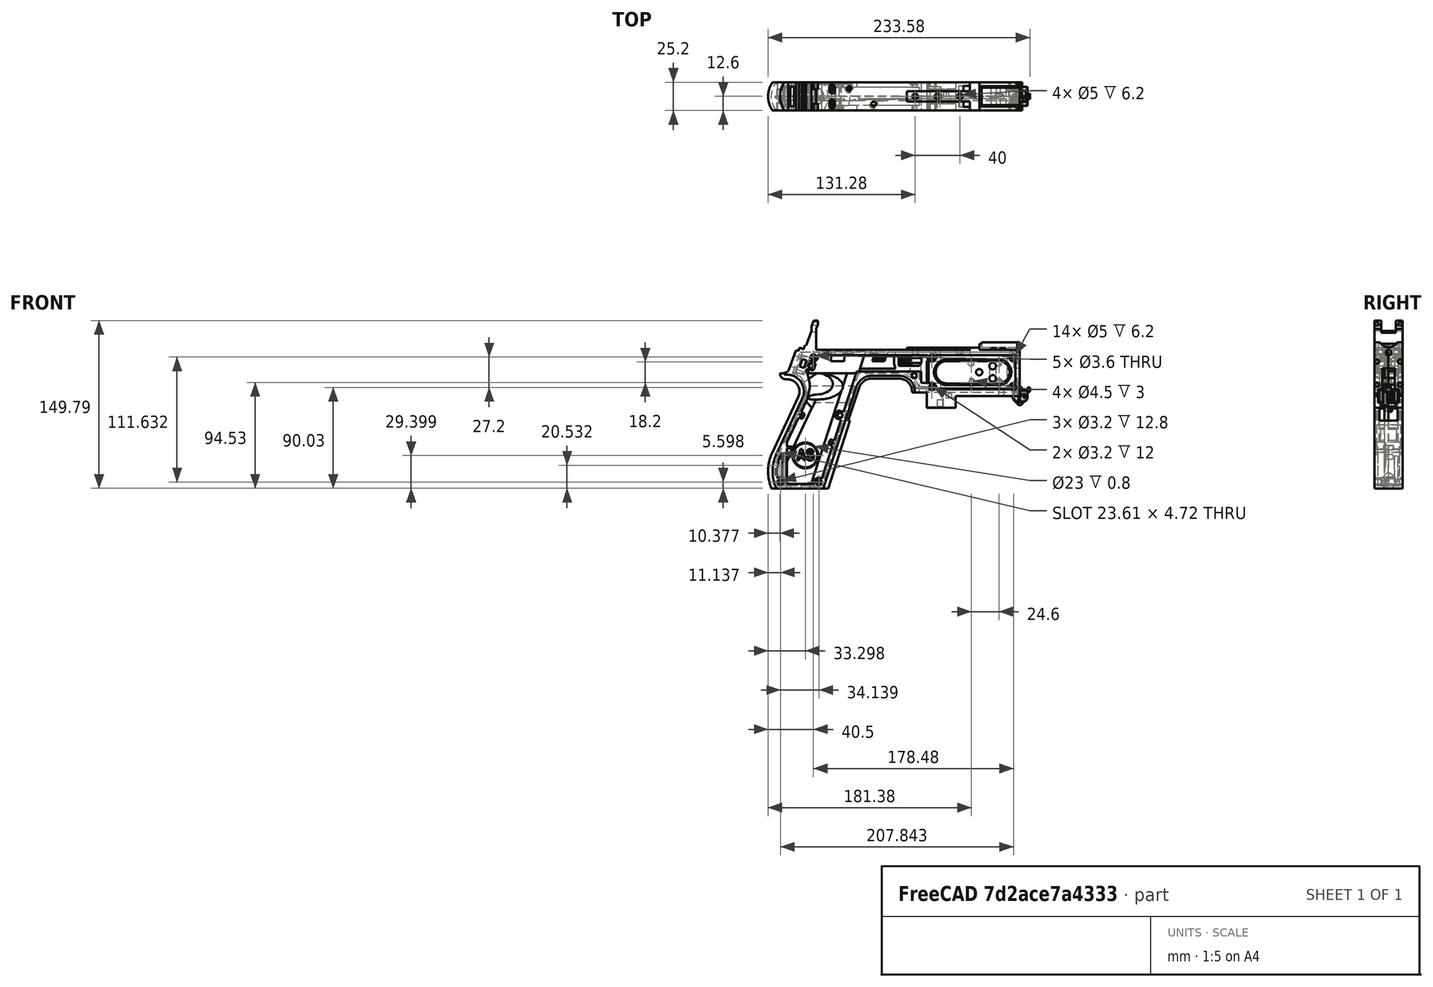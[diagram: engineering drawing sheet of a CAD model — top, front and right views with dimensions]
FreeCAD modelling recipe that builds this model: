
FCSTD DOCUMENT  (FreeCAD 1.0R39319 (Git))
Label: PICON-OF_ver_36
License: All rights reserved
LicenseURL: https://en.wikipedia.org/wiki/All_rights_reserved
objects: Sketcher::SketchObject×106, Part::Extrusion×50, Part::Cut×39, PartDesign::Pad×28, PartDesign::Pocket×18, PartDesign::Chamfer×15, PartDesign::Body×9, PartDesign::Fillet×6, PartDesign::SubtractivePipe×4, Part::Part2DObjectPython×4, PartDesign::SubtractiveLoft×4, PartDesign::Plane×2, PartDesign::SubShapeBinder×2, Part::Sweep×1, PartDesign::ShapeBinder×1, Part::MultiFuse×1, Mesh::Feature×1
note: 546 computed .brp shape members not serialized (recipe doc carries the construction recipe); baked Part::Feature solids carry a one-line shape summary decoded from their .brp

FEATURE [Sketcher::SketchObject] Sketch  label="corpo principale"
  ArcFitTolerance = 1e-06
  AttacherType = Attacher::AttachEngine3D
  AttachmentSupport = -> [XZ_Plane]
  FullyConstrained = true
  MakeInternals = false
  MapMode = 5
  Placement = pos=(0,0,0) rot=(1,0,0;1.5708rad)
  sketch-geometry (65):
    g0: LineSegment StartX=0 StartY=0 StartZ=0 EndX=-57.2 EndY=0 EndZ=0
    g1: LineSegment StartX=-57.2 StartY=0 StartZ=0 EndX=-57.2 EndY=-10.4 EndZ=0
    g2: LineSegment StartX=-57.2 StartY=-10.4 StartZ=0 EndX=-82.8 EndY=-10.4 EndZ=0
    g3: LineSegment StartX=-82.8 StartY=-10.4 StartZ=0 EndX=-82.8 EndY=3.2 EndZ=0
    g4: LineSegment StartX=-82.8 StartY=3.2 StartZ=0 EndX=-93.6 EndY=3.2 EndZ=0
    g5: LineSegment StartX=-93.6 StartY=3.2 StartZ=0 EndX=-93.6 EndY=4 EndZ=0
    g6: LineSegment StartX=-107.6 StartY=18 StartZ=0 EndX=-132.428 EndY=18 EndZ=0
    g7: LineSegment StartX=-145.743 StartY=8.32624 StartZ=0 EndX=-175.232 EndY=-82.4316 EndZ=0
    g8: LineSegment StartX=-175.232 StartY=-82.4316 StartZ=0 EndX=-217.232 EndY=-82.4316 EndZ=0
    g9: LineSegment StartX=-217.232 StartY=-52.1862 StartZ=0 EndX=-193.988 EndY=-2.33927 EndZ=0
    g10: LineSegment StartX=-206.196 StartY=23.0857 StartZ=0 EndX=-199.861 EndY=40.4914 EndZ=0
    g11: LineSegment StartX=-199.861 StartY=40.4914 StartZ=0 EndX=-197.061 EndY=40.4914 EndZ=0
    g12: LineSegment StartX=-197.061 StartY=40.4914 StartZ=0 EndX=-197.061 EndY=42.8914 EndZ=0
    g13: LineSegment StartX=-197.061 StartY=42.8914 StartZ=0 EndX=-194.261 EndY=42.8914 EndZ=0
    g14: LineSegment StartX=-194.261 StartY=42.8914 StartZ=0 EndX=-194.535 EndY=42.1397 EndZ=0
    g15: LineSegment StartX=-194.535 StartY=42.1397 StartZ=0 EndX=-193.031 EndY=41.5924 EndZ=0
    g16: LineSegment StartX=-193.031 StartY=41.5924 StartZ=0 EndX=-191.663 EndY=45.3512 EndZ=0
    g17: LineSegment StartX=-191.663 StartY=45.3512 StartZ=0 EndX=-190.536 EndY=44.9408 EndZ=0
    g18: LineSegment StartX=-190.536 StartY=44.9408 StartZ=0 EndX=-185.747 EndY=58.0965 EndZ=0
    g19: LineSegment StartX=-185.747 StartY=58.0965 StartZ=0 EndX=-185.747 EndY=62.0965 EndZ=0
    g20: LineSegment StartX=-185.747 StartY=62.0965 StartZ=0 EndX=-183.832 EndY=67.3588 EndZ=0
    g21: LineSegment StartX=-183.832 StartY=67.3588 StartZ=0 EndX=-180.232 EndY=67.3588 EndZ=0
    g22: LineSegment StartX=-180.232 StartY=67.3588 StartZ=0 EndX=-180.232 EndY=63.7588 EndZ=0
    g23: LineSegment StartX=-180.232 StartY=63.7588 StartZ=0 EndX=-181.6 EndY=60 EndZ=0
    g24: LineSegment StartX=-181.6 StartY=60 StartZ=0 EndX=-181.6 EndY=41.2 EndZ=0
    g25: LineSegment StartX=-181.6 StartY=41.2 StartZ=0 EndX=-100.8 EndY=41.2 EndZ=0
    g26: LineSegment StartX=-36 StartY=43.2 StartZ=0 EndX=-36 EndY=41.2 EndZ=0
    g27: LineSegment StartX=0 StartY=48 StartZ=0 EndX=0 EndY=0 EndZ=0
    g28: LineSegment StartX=-209.901 StartY=19.85 StartZ=0 EndX=-209.901 EndY=20.1 EndZ=0
    g29: LineSegment StartX=-208.001 StartY=22 StartZ=0 EndX=-207.747 EndY=22 EndZ=0
    g30: LineSegment StartX=-207.583 StartY=19 StartZ=0 EndX=-209.051 EndY=19 EndZ=0
    g31: ArcOfCircle CenterX=-208.001 CenterY=20.1 CenterZ=0 NormalX=0 NormalY=0 NormalZ=1 AngleXU=0 Radius=1.9 StartAngle=1.5708 EndAngle=3.14159
    g32: GeomPoint [constr] X=-209.901 Y=22 Z=0
    g33: ArcOfCircle CenterX=-209.051 CenterY=19.85 CenterZ=0 NormalX=0 NormalY=0 NormalZ=1 AngleXU=0 Radius=0.85 StartAngle=3.14159 EndAngle=4.71239
    g34: GeomPoint [constr] X=-209.901 Y=19 Z=0
    g35: ArcOfCircle CenterX=-207.747 CenterY=23.65 CenterZ=0 NormalX=0 NormalY=0 NormalZ=1 AngleXU=0 Radius=1.65 StartAngle=4.71239 EndAngle=5.93412
    g36: GeomPoint [constr] X=-206.591 Y=22 Z=0
    g37: LineSegment StartX=-4 StartY=6 StartZ=0 EndX=-4 EndY=36.4 EndZ=0
    g38: LineSegment StartX=-4 StartY=36.4 StartZ=0 EndX=-185.2 EndY=36.4 EndZ=0
    g39: LineSegment StartX=-185.2 StartY=36.4 StartZ=0 EndX=-190.441 EndY=22 EndZ=0
    g40: LineSegment StartX=-214.575 StartY=-78.4316 StartZ=0 EndX=-178.142 EndY=-78.4316 EndZ=0
    g41: LineSegment StartX=-178.142 StartY=-78.4316 StartZ=0 EndX=-145.51 EndY=22 EndZ=0
    g42: LineSegment StartX=-145.51 StartY=22 StartZ=0 EndX=-87.91 EndY=22 EndZ=0
    g43: LineSegment StartX=-87.91 StartY=22 StartZ=0 EndX=-87.91 EndY=11.6 EndZ=0
    g44: LineSegment StartX=-87.91 StartY=11.6 StartZ=0 EndX=-80.11 EndY=11.6 EndZ=0
    g45: LineSegment StartX=-80.11 StartY=11.6 StartZ=0 EndX=-80.11 EndY=6 EndZ=0
    g46: LineSegment StartX=-80.11 StartY=6 StartZ=0 EndX=-4 EndY=6 EndZ=0
    g47: LineSegment StartX=-190.363 StartY=-4.02975 StartZ=0 EndX=-213.607 EndY=-53.8767 EndZ=0
    g48: ArcOfCircle CenterX=-132.428 CenterY=4 CenterZ=0 NormalX=0 NormalY=0 NormalZ=1 AngleXU=0 Radius=14 StartAngle=1.5708 EndAngle=2.82743
    g49: GeomPoint [constr] X=-142.6 Y=18 Z=0
    g50: ArcOfCircle CenterX=-107.6 CenterY=4 CenterZ=0 NormalX=0 NormalY=0 NormalZ=1 AngleXU=0 Radius=14 StartAngle=0 EndAngle=1.5708
    g51: GeomPoint [constr] X=-93.6 Y=18 Z=0
    g52: ArcOfCircle CenterX=-184.801 CenterY=-67.3089 CenterZ=0 NormalX=0 NormalY=0 NormalZ=1 AngleXU=0 Radius=35.7833 StartAngle=2.70526 EndAngle=3.57792
    g53: ArcOfCircle CenterX=-207.583 CenterY=4 CenterZ=0 NormalX=0 NormalY=0 NormalZ=1 AngleXU=0 Radius=15 StartAngle=5.84685 EndAngle=7.85398
    g54: LineSegment [constr] StartX=-213.607 StartY=-53.8767 StartZ=0 EndX=-217.232 EndY=-52.1862 EndZ=0
    g55: ArcOfCircle CenterX=-184.801 CenterY=-67.3089 CenterZ=0 NormalX=0 NormalY=0 NormalZ=1 AngleXU=0 Radius=31.7833 StartAngle=2.70526 EndAngle=3.49911
    g56: ArcOfCircle CenterX=-218.095 CenterY=8.90192 CenterZ=0 NormalX=0 NormalY=0 NormalZ=1 AngleXU=0 Radius=30.5989 StartAngle=5.84685 EndAngle=6.72553
    g57: LineSegment StartX=-44.6 StartY=43.2 StartZ=0 EndX=-36 EndY=43.2 EndZ=0
    g58: LineSegment StartX=-100.8 StartY=41.2 StartZ=0 EndX=-44.6 EndY=41.2 EndZ=0
    g59: LineSegment StartX=-44.6 StartY=41.2 StartZ=0 EndX=-44.6 EndY=43.2 EndZ=0
    g60: LineSegment StartX=-2.4 StartY=48 StartZ=0 EndX=0 EndY=48 EndZ=0
    g61: LineSegment StartX=-36 StartY=41.2 StartZ=0 EndX=-2.4 EndY=41.2 EndZ=0
    g62: LineSegment StartX=-2.4 StartY=41.2 StartZ=0 EndX=-2.4 EndY=48 EndZ=0
    g63: LineSegment [constr] StartX=-181.6 StartY=36.4 StartZ=0 EndX=-152.209 EndY=36.4 EndZ=0
    g64: LineSegment [constr] StartX=-181.6 StartY=36.4 StartZ=0 EndX=-130.41 EndY=36.4 EndZ=0
  constraints (183):
    c: Coincident(g-1,g0)
    c: PointOnObject(g0,g-1)
    c: Coincident(g0,g1)
    c: Vertical(g1)
    c: Coincident(g1,g2)
    c: Horizontal(g2)
    c: Coincident(g2,g3)
    c: Vertical(g3)
    c: Coincident(g3,g4)
    c: Coincident(g4,g5)
    c: Vertical(g5)
    c: Horizontal(g6)
    c: Coincident(g7,g8)
    c: Horizontal(g8)
    c: Coincident(g10,g11)
    c: Horizontal(g11)
    c: Coincident(g11,g12)
    c: Vertical(g12)
    c: Coincident(g12,g13)
    c: Horizontal(g13)
    c: Coincident(g13,g14)
    c: Coincident(g14,g15)
    c: Coincident(g15,g16)
    c: Coincident(g16,g17)
    c: Coincident(g17,g18)
    c: Coincident(g18,g19)
    c: Vertical(g19)
    c: Coincident(g19,g20)
    c: Coincident(g20,g21)
    c: Horizontal(g21)
    c: Coincident(g21,g22)
    c: Vertical(g22)
    c: Coincident(g22,g23)
    c: Coincident(g23,g24)
    c: Vertical(g24)
    c: Coincident(g24,g25)
    c: Horizontal(g25)
    c: Coincident(g57,g26)
    c: Vertical(g26)
    c: Coincident(g26,g61)
    c: PointOnObject(g60,g-2)
    c: Coincident(g60,g27)
    c: Coincident(g27,g0)
    c: DistanceY(g27,g27) = 48
    c: DistanceY(g1,g1) = 10.4
    c: DistanceX(g0,g0) = 57.2
    c: DistanceX(g2,g2) = 25.6
    c: Horizontal(g4)
    c: DistanceY(g3,g3) = 13.6
    c: DistanceX(g4,g4) = 10.8
    c: DistanceY(g5,g51) = 14.8
    c: DistanceX(g49,g51) = 49
    c: Distance(g7,g49) = 105.6
    c: DistanceX(g61,g60) = 36
    c: DistanceX(g25,g25) = 80.8
    c: DistanceY(g24,g24) = 18.8
    c: DistanceY(g22,g22) = 3.6
    c: Distance(g23) = 4
    c: Angle(g-1,g23) = 1.22173
    c: DistanceX(g21,g21) = 3.6
    c: Distance(g20) = 5.6
    c: Angle(g-1,g20) = 1.22173
    c: DistanceY(g19,g19) = 4
    c: Distance(g18) = 14
    c: Angle(g-1,g18) = 1.22173
    c: Distance(g17) = 1.2
    c: Distance(g16) = 4
    c: Angle(g16) = 1.22173
    c: Perpendicular(g18,g17)
    c: Distance(g15) = 1.6
    c: Perpendicular(g16,g15)
    c: Distance(g14) = 0.8
    c: DistanceX(g13,g13) = 2.8
    c: Perpendicular(g15,g14)
    c: DistanceY(g12,g12) = 2.4
    c: DistanceX(g11,g11) = 2.8
    c: Distance(g9) = 55
    c: Angle(g9,g-1) = 2.00713
    c: Horizontal(g29)
    c: Vertical(g28)
    c: Horizontal(g30)
    c: PointOnObject(g32,g29)
    c: PointOnObject(g32,g28)
    c: Tangent(g29,g31) = 1.5708
    c: Tangent(g28,g31) = 1.5708
    c: PointOnObject(g34,g28)
    c: PointOnObject(g34,g30)
    c: Tangent(g28,g33) = 1.5708
    c: Tangent(g30,g33) = 1.5708
    c: PointOnObject(g36,g29)
    c: PointOnObject(g36,g10)
    c: Tangent(g29,g35) = -1.5708
    c: Tangent(g10,g35) = -1.5708
    c: Angle(g-1,g10) = 1.22173
    c: Radius(g35) = 1.65
    c: Vertical(g37)
    c: Coincident(g37,g38)
    c: Horizontal(g38)
    c: Coincident(g38,g39)
    c: Horizontal(g40)
    c: Coincident(g40,g41)
    c: Coincident(g41,g42)
    c: Horizontal(g42)
    c: Coincident(g42,g43)
    c: Vertical(g43)
    c: Coincident(g43,g44)
    c: Horizontal(g44)
    c: Coincident(g44,g45)
    c: Vertical(g45)
    c: Coincident(g45,g46)
    c: Coincident(g46,g37)
    c: Horizontal(g46)
    c: DistanceY(g0,g37) = 6
    c: DistanceX(g37,g0) = 4
    c: DistanceY(g37,g25) = 4.8
    c: DistanceX(g38,g38) = 181.2
    c: DistanceX(g42,g42) = 57.6
    c: DistanceY(g49,g41) = 4
    c: DistanceX(g41,g49) = 2.91
    c: DistanceY(g43,g43) = 10.4
    c: DistanceX(g44,g44) = 7.8
    c: DistanceY(g7,g40) = 4
    c: Distance(g47) = 55
    c: Angle(g-1,g39) = 1.22173
    c: PointOnObject(g49,g7)
    c: PointOnObject(g49,g6)
    c: Tangent(g7,g48) = -1.5708
    c: Tangent(g6,g48) = -1.5708
    c: PointOnObject(g51,g5)
    c: PointOnObject(g51,g6)
    c: Tangent(g5,g50) = -1.5708
    c: Tangent(g6,g50) = -1.5708
    c: Radius(g50) = 14
    c: Radius(g48) = 14
    c: DistanceX(g8,g8) = 42
    c: Angle(g7,g-1) = 1.88496
    c: Parallel(g41,g7)
    c: Parallel(g47,g9)
    c: Coincident(g52,g8)
    c: Tangent(g52,g9) = 1.5708
    c: DistanceX(g9,g8) = 0
    c: Tangent(g53,g9) = -1.5708
    c: Tangent(g53,g30) = -1.5708
    c: Diameter(g53) = 30
    c: DistanceY(g53,g0) = -4
    c: Coincident(g54,g47)
    c: Distance(g54) = 4
    c: Coincident(g54,g9)
    c: Coincident(g55,g40)
    c: Tangent(g55,g47) = -1.5708
    c: Coincident(g52,g55)
    c: Coincident(g56,g39)
    c: Tangent(g56,g47) = 1.5708
    c: Horizontal(g57)
    c: DistanceX(g57,g57) = 8.6
    c: Coincident(g58,g25)
    c: Horizontal(g58)
    c: Coincident(g59,g58)
    c: Vertical(g59)
    c: DistanceY(g58,g57) = 2
    c: DistanceX(g58,g58) = 56.2
    c: Coincident(g59,g57)
    c: DistanceY(g41,g36) = 0
    c: DistanceY(g36,g39) = 0
    c: DistanceY(g28,g28) = 0.25
    c: DistanceX(g30,g36) = 2.46
    c: DistanceX(g28,g29) = 1.9
    c: Coincident(g62,g60)
    c: Horizontal(g60)
    c: DistanceX(g62,g27) = 2.4
    c: Coincident(g61,g62)
    c: DistanceY(g26,g26) = 2
    c: Vertical(g62)
    c: DistanceY(g61,g60) = 6.8
    c: Horizontal(g61)
    c: Distance(g63) = 29.391
    c: PointOnObject(g63,g38)
    c: PointOnObject(g63,g38)
    c: Distance(g64) = 51.19
    c: PointOnObject(g64,g38)
    c: PointOnObject(g64,g38)
    c: DistanceX(g24,g63) = 0
    c: DistanceX(g24,g64) = 0
FEATURE [Part::Extrusion] Extrude  label="Extrude corpo principale"
  Base = -> Sketch
  Dir = (0,-1,2e-16)
  DirMode = 2
  FaceMakerClass = Part::FaceMakerBullseye
  FaceMakerMode = 3
  LengthFwd = 25.2
  LengthRev = 12.6
  Solid = true
  Symmetric = true
FEATURE [Sketcher::SketchObject] Sketch002  label="scavo grilletto"
  ArcFitTolerance = 1e-06
  AttachmentSupport = -> [XZ_Plane]
  ExternalGeometry = -> [Sketch]
  FullyConstrained = true
  MakeInternals = false
  MapMode = 5
  Placement = pos=(0,0,0) rot=(1,0,0;1.5708rad)
  sketch-geometry (4):
    g0: LineSegment StartX=-89.51 StartY=22 StartZ=0 EndX=-152.71 EndY=22 EndZ=0
    g1: LineSegment StartX=-152.71 StartY=22 StartZ=0 EndX=-167.006 EndY=-22 EndZ=0
    g2: LineSegment StartX=-167.006 StartY=-22 StartZ=0 EndX=-89.51 EndY=-22 EndZ=0
    g3: LineSegment StartX=-89.51 StartY=-22 StartZ=0 EndX=-89.51 EndY=22 EndZ=0
  constraints (12):
    c: Horizontal(g0)
    c: Coincident(g0,g1)
    c: Coincident(g1,g2)
    c: Horizontal(g2)
    c: Coincident(g2,g3)
    c: Coincident(g3,g0)
    c: Vertical(g3)
    c: Angle(g1,g0) = 1.88496
    c: DistanceY(g3,g3) = 44
    c: DistanceX(g0,g0) = 63.2
    c: DistanceX(g0,g-3) = 1.6
    c: DistanceY(g-3,g0) = 0
FEATURE [Sketcher::SketchObject] Sketch004  label="traiettoria arrotondamento impugnatura anteriore"
  ArcFitTolerance = 1e-06
  AttachmentSupport = -> [XZ_Plane]
  ExternalGeometry = -> [Sketch]
  FullyConstrained = true
  MakeInternals = false
  MapMode = 5
  Placement = pos=(0,0,0) rot=(1,0,0;1.5708rad)
  sketch-geometry (13):
    g0: LineSegment StartX=-175.232 StartY=-82.4316 StartZ=0 EndX=-145.743 EndY=8.32624 EndZ=0
    g1: LineSegment StartX=-93.6 StartY=3.2 StartZ=0 EndX=-93.6 EndY=4 EndZ=0
    g2: LineSegment StartX=-132.428 StartY=18 StartZ=0 EndX=-107.6 EndY=18 EndZ=0
    g3: ArcOfCircle CenterX=-132.428 CenterY=4 CenterZ=0 NormalX=0 NormalY=0 NormalZ=1 AngleXU=0 Radius=14 StartAngle=1.5708 EndAngle=2.82743
    g4: ArcOfCircle CenterX=-107.6 CenterY=4 CenterZ=0 NormalX=0 NormalY=0 NormalZ=1 AngleXU=0 Radius=14 StartAngle=0 EndAngle=1.5708
    g5: LineSegment StartX=-175.232 StartY=-82.4316 StartZ=0 EndX=-217.232 EndY=-82.4316 EndZ=0
    g6: LineSegment StartX=-217.232 StartY=-52.1862 StartZ=0 EndX=-193.988 EndY=-2.33927 EndZ=0
    g7: LineSegment StartX=-209.051 StartY=19 StartZ=0 EndX=-207.583 EndY=19 EndZ=0
    g8: LineSegment StartX=-209.901 StartY=20.1 StartZ=0 EndX=-209.901 EndY=19.85 EndZ=0
    g9: ArcOfCircle CenterX=-184.801 CenterY=-67.3089 CenterZ=0 NormalX=0 NormalY=0 NormalZ=1 AngleXU=0 Radius=35.7833 StartAngle=2.70526 EndAngle=3.57792
    g10: ArcOfCircle CenterX=-207.583 CenterY=4 CenterZ=0 NormalX=0 NormalY=0 NormalZ=1 AngleXU=0 Radius=15 StartAngle=5.84685 EndAngle=7.85398
    g11: ArcOfCircle CenterX=-209.051 CenterY=19.85 CenterZ=0 NormalX=0 NormalY=0 NormalZ=1 AngleXU=0 Radius=0.85 StartAngle=3.14159 EndAngle=4.71239
    g12: ArcOfCircle CenterX=-208.001 CenterY=20.1 CenterZ=0 NormalX=0 NormalY=0 NormalZ=1 AngleXU=0 Radius=1.9 StartAngle=1.5708 EndAngle=3.14159
  constraints (26):
    c: Coincident(g0,g-3)
    c: Coincident(g0,g-6)
    c: Coincident(g1,g-8)
    c: Coincident(g1,g-7)
    c: Coincident(g2,g-5)
    c: Coincident(g2,g-4)
    c: Coincident(g3,g2)
    c: Tangent(g3,g0) = 1.5708
    c: Coincident(g4,g1)
    c: Tangent(g4,g2) = 1.5708
    c: Coincident(g5,g0)
    c: Coincident(g5,g-9)
    c: Coincident(g6,g-12)
    c: Coincident(g6,g-11)
    c: Coincident(g7,g-15)
    c: Coincident(g7,g-14)
    c: Coincident(g8,g-16)
    c: Coincident(g8,g-17)
    c: Tangent(g9,g6) = 1.5708
    c: Coincident(g9,g5)
    c: Coincident(g10,g7)
    c: Tangent(g10,g6) = -1.5708
    c: Tangent(g11,g7) = -1.5708
    c: Coincident(g11,g8)
    c: Tangent(g12,g8) = -1.5708
    c: Coincident(g12,g-17)
FEATURE [PartDesign::Plane] DatumPlane  label="Piano per disegno arrotondamento impugnatura"
  AttachmentSupport = -> [Sketch]
  Length = 68.5841
  MapMode = 7
  Placement = pos=(-145.743,1.8e-15,8.32624) rot=(0.154555,0.154555,0.97582;1.59527rad)
  ResizeMode = 0
  Width = 191.269
FEATURE [Sketcher::SketchObject] Sketch005  label="forma arrotondamento impugnatura anteriore"
  ArcFitTolerance = 1e-06
  AttachmentSupport = -> [DatumPlane]
  FullyConstrained = true
  MakeInternals = false
  MapMode = 5
  Placement = pos=(-145.743,1.8e-15,8.32624) rot=(0.154555,0.154555,0.97582;1.59527rad)
  sketch-geometry (5):
    g0: GeomPoint [constr] X=0 Y=-4 Z=0
    g1: GeomPoint [constr] X=-12.6 Y=7.1e-15 Z=0
    g2: GeomPoint [constr] X=12.6 Y=4.97e-14 Z=0
    g3: LineSegment StartX=-12.6 StartY=7.1e-15 StartZ=0 EndX=12.6 EndY=4.97e-14 EndZ=0
    g4: ArcOfCircle CenterX=-3.88e-14 CenterY=17.845 CenterZ=0 NormalX=0 NormalY=0 NormalZ=1 AngleXU=0 Radius=21.845 StartAngle=4.09759 EndAngle=5.32718
  constraints (11):
    c: DistanceY(g0,g-1) = 4
    c: DistanceX(g-1,g0) = 0
    c: DistanceX(g1,g-1) = 12.6
    c: DistanceX(g-1,g2) = 12.6
    c: DistanceY(g-1,g2) = 0
    c: DistanceY(g-1,g1) = 0
    c: Coincident(g3,g1)
    c: Coincident(g3,g2)
    c: Coincident(g4,g1)
    c: Coincident(g4,g2)
    c: PointOnObject(g0,g4)
FEATURE [Part::Sweep] Sweep  label="Sweep impugnatura"
  Frenet = true
  Sections = -> [Sketch005]
  Solid = true
  Spine = -> Sketch [Edge32,Edge33,Edge34,Edge35,Edge36,Edge37,Edge38,Edge39,Edge40,Edge41,Edge42,Edge43,Edge44]
  Transition = 1
FEATURE [Sketcher::SketchObject] Sketch008  label="buchi e pulizie varie"
  ArcFitTolerance = 1e-06
  AttachmentSupport = -> [XZ_Plane]
  ExternalGeometry = -> [Sketch]
  FullyConstrained = true
  MakeInternals = false
  MapMode = 5
  Placement = pos=(0,0,0) rot=(1,0,0;1.5708rad)
  sketch-geometry (26):
    g0: LineSegment StartX=-96.278 StartY=20.155 StartZ=0 EndX=-92.278 EndY=20.155 EndZ=0
    g1: LineSegment StartX=-92.278 StartY=20.155 StartZ=0 EndX=-92.278 EndY=16.155 EndZ=0
    g2: LineSegment StartX=-92.278 StartY=16.155 StartZ=0 EndX=-96.278 EndY=16.155 EndZ=0
    g3: LineSegment StartX=-96.278 StartY=16.155 StartZ=0 EndX=-96.278 EndY=20.155 EndZ=0
    g4: LineSegment StartX=-222.232 StartY=-82.4316 StartZ=0 EndX=-170.232 EndY=-82.4316 EndZ=0
    g5: LineSegment StartX=-170.232 StartY=-82.4316 StartZ=0 EndX=-170.232 EndY=-86.4316 EndZ=0
    g6: LineSegment StartX=-170.232 StartY=-86.4316 StartZ=0 EndX=-222.232 EndY=-86.4316 EndZ=0
    g7: LineSegment StartX=-222.232 StartY=-86.4316 StartZ=0 EndX=-222.232 EndY=-82.4316 EndZ=0
    g8: LineSegment StartX=-213.901 StartY=20.1 StartZ=0 EndX=-213.901 EndY=26 EndZ=0
    g9: LineSegment StartX=-213.901 StartY=26 StartZ=0 EndX=-206.196 EndY=26 EndZ=0
    g10: LineSegment StartX=-17.4 StartY=42.8 StartZ=0 EndX=-12.4 EndY=42.8 EndZ=0
    g11: LineSegment StartX=-12.4 StartY=42.8 StartZ=0 EndX=-12.4 EndY=41.2 EndZ=0
    g12: LineSegment StartX=-12.4 StartY=41.2 StartZ=0 EndX=-17.4 EndY=41.2 EndZ=0
    g13: LineSegment StartX=-17.4 StartY=41.2 StartZ=0 EndX=-17.4 EndY=42.8 EndZ=0
    g14: LineSegment StartX=-25.9 StartY=42.8 StartZ=0 EndX=-20.9 EndY=42.8 EndZ=0
    g15: LineSegment StartX=-20.9 StartY=42.8 StartZ=0 EndX=-20.9 EndY=41.2 EndZ=0
    g16: LineSegment StartX=-20.9 StartY=41.2 StartZ=0 EndX=-25.9 EndY=41.2 EndZ=0
    g17: LineSegment StartX=-25.9 StartY=41.2 StartZ=0 EndX=-25.9 EndY=42.8 EndZ=0
    g18: GeomPoint [constr] X=-206.196 Y=23.0857 Z=0
    g19: GeomPoint [constr] X=-213.901 Y=20.1 Z=0
    g20: BSplineCurve PolesCount=4 KnotsCount=2 Degree=3 IsPeriodic=0
    g21-g24: Circle [constr] x4 (B-spline internal-alignment scaffolding for g20; pole/knot coordinates omitted)
    g25: LineSegment StartX=-206.196 StartY=26 StartZ=0 EndX=-206.196 EndY=23.0857 EndZ=0
  constraints (73):
    c: Horizontal(g0)
    c: Coincident(g1,g0)
    c: Vertical(g1)
    c: Coincident(g2,g1)
    c: Horizontal(g2)
    c: Coincident(g3,g2)
    c: Coincident(g3,g0)
    c: Vertical(g3)
    c: DistanceX(g0,g-4) = 4.368
    c: DistanceY(g0,g-4) = 1.845
    c: DistanceY(g1,g1) = 4
    c: DistanceX(g2,g2) = 4
    c: Horizontal(g4)
    c: Coincident(g5,g4)
    c: Vertical(g5)
    c: Coincident(g6,g5)
    c: Horizontal(g6)
    c: Coincident(g7,g6)
    c: Coincident(g7,g4)
    c: Vertical(g7)
    c: DistanceY(g7,g7) = 4
    c: DistanceX(g4,g-5) = 5
    c: DistanceX(g-5,g4) = 5
    c: DistanceY(g4,g-5) = 0
    c: Coincident(g9,g8)
    c: Parallel(g9,g-6)
    c: DistanceX(g8,g-8) = 4
    c: Horizontal(g10)
    c: Coincident(g11,g10)
    c: Vertical(g11)
    c: Coincident(g12,g11)
    c: Horizontal(g12)
    c: Coincident(g13,g12)
    c: Coincident(g13,g10)
    c: Vertical(g13)
    c: Horizontal(g14)
    c: Coincident(g15,g14)
    c: Vertical(g15)
    c: Coincident(g16,g15)
    c: Horizontal(g16)
    c: Coincident(g17,g16)
    c: Coincident(g17,g14)
    c: Vertical(g17)
    c: DistanceY(g11,g10) = 1.6
    c: DistanceX(g10,g10) = 5
    c: DistanceY(g15,g14) = 1.6
    c: DistanceX(g14,g14) = 5
    c: DistanceX(g15,g12) = 3.5
    c: DistanceX(g11,g-9) = 10
    c: DistanceY(g-9,g11) = 0
    c: DistanceY(g-9,g15) = 0
    c: Perpendicular(g8,g9)
    c: DistanceY(g-7,g9) = 4
    c: DistanceY(g8,g-8) = 0
    c: InternalAlignment(g18,g20)
    c: InternalAlignment(g19,g20)
    c: InternalAlignment(g21,g20)
    c: Weight(g21) = 1
    c: InternalAlignment(g22,g20)
    c: Equal(g22,g21)
    c: InternalAlignment(g23,g20)
    c: Equal(g23,g21)
    c: InternalAlignment(g24,g20)
    c: Equal(g24,g21)
    c: Coincident(g18,g-12)
    c: Coincident(g19,g8)
    c: Coincident(g25,g9)
    c: Coincident(g25,g20)
    c: Vertical(g25)
    c: DistanceY(g20,g23) = 0
    c: DistanceY(g22,g18) = 2.26
    c: DistanceX(g22,g18) = 0.93
    c: DistanceX(g20,g23) = 2.9
FEATURE [Part::Extrusion] Extrude004  label="Extrude Buchi e pulizie varie"
  Base = -> Sketch008
  Dir = (0,-1,2e-16)
  DirMode = 2
  FaceMakerClass = Part::FaceMakerBullseye
  FaceMakerMode = 3
  LengthFwd = 25.2
  LengthRev = 0
  Solid = true
  Symmetric = true
FEATURE [Sketcher::SketchObject] Sketch009  label="rinforzi"
  ArcFitTolerance = 1e-06
  AttachmentSupport = -> [XZ_Plane]
  ExternalGeometry = -> [Sketch]
  FullyConstrained = true
  MakeInternals = false
  MapMode = 5
  Placement = pos=(0,0,0) rot=(1,0,0;1.5708rad)
  sketch-geometry (9):
    g0: LineSegment StartX=-87.91 StartY=22 StartZ=0 EndX=-87.91 EndY=36.4 EndZ=0
    g1: LineSegment StartX=-87.91 StartY=36.4 StartZ=0 EndX=-97.91 EndY=36.4 EndZ=0
    g2: LineSegment StartX=-97.91 StartY=36.4 StartZ=0 EndX=-97.91 EndY=22 EndZ=0
    g3: LineSegment StartX=-97.91 StartY=22 StartZ=0 EndX=-87.91 EndY=22 EndZ=0
    g4: LineSegment StartX=-149.713 StartY=9.06563 StartZ=0 EndX=-154.586 EndY=-5.93437 EndZ=0
    g5: LineSegment StartX=-154.586 StartY=-5.93437 StartZ=0 EndX=-191.863 EndY=-5.93437 EndZ=0
    g6: LineSegment StartX=-191.863 StartY=-5.93437 StartZ=0 EndX=-191.863 EndY=9.06563 EndZ=0
    g7: LineSegment StartX=-191.863 StartY=9.06563 StartZ=0 EndX=-149.713 EndY=9.06563 EndZ=0
    g8: LineSegment [constr] StartX=-145.51 StartY=22 StartZ=0 EndX=-149.713 EndY=9.06563 EndZ=0
  constraints (25):
    c: Vertical(g0)
    c: Coincident(g1,g0)
    c: Horizontal(g1)
    c: Coincident(g2,g1)
    c: Vertical(g2)
    c: Coincident(g3,g2)
    c: Coincident(g3,g0)
    c: Horizontal(g3)
    c: Coincident(g0,g-4)
    c: DistanceX(g3,g3) = 10
    c: DistanceY(g0,g-3) = 0
    c: Coincident(g5,g4)
    c: Horizontal(g5)
    c: Coincident(g6,g5)
    c: Vertical(g6)
    c: Coincident(g7,g6)
    c: Coincident(g7,g4)
    c: Horizontal(g7)
    c: Distance(g8) = 13.6
    c: Parallel(g-6,g8)
    c: Coincident(g-6,g8)
    c: Parallel(g4,g-6)
    c: DistanceY(g4,g4) = 15
    c: Coincident(g4,g8)
    c: DistanceX(g-5,g5) = -1.5
FEATURE [Part::Extrusion] Extrude001  label="Extrude scavo grilletto"
  Base = -> Sketch002
  Dir = (0,-1,2e-16)
  DirMode = 2
  FaceMakerClass = Part::FaceMakerBullseye
  FaceMakerMode = 3
  LengthFwd = 16
  LengthRev = 0
  Solid = true
  Symmetric = true
FEATURE [Part::Extrusion] Extrude005  label="Extrude Rinforzi"
  Base = -> Sketch009
  Dir = (0,-1,2e-16)
  DirMode = 2
  FaceMakerClass = Part::FaceMakerBullseye
  FaceMakerMode = 3
  LengthFwd = 2
  LengthRev = 0
  Placement = pos=(0,12.6,0) rot=(0,0,1;0rad)
  Solid = true
  Symmetric = false
FEATURE [PartDesign::ShapeBinder] CopyCut
  TraceSupport = false
FEATURE [PartDesign::Plane] DatumPlane001
  AttachmentSupport = -> [CopyCut]
  Length = 60
  MapMode = 5
  Placement = pos=(0,12.6,0) rot=(0,0.707107,0.707107;3.14159rad)
  ResizeMode = 0
  Width = 60
FEATURE [Sketcher::SketchObject] Sketch010  label="buco neopixel"
  ArcFitTolerance = 1e-06
  AttachmentSupport = -> [XZ_Plane]
  ExternalGeometry = -> [Sketch]
  FullyConstrained = true
  MakeInternals = false
  MapMode = 5
  Placement = pos=(0,0,0) rot=(1,0,0;1.5708rad)
  sketch-geometry (5):
    g0: LineSegment [constr] StartX=-199.861 StartY=40.4914 StartZ=0 EndX=-201.368 EndY=36.3521 EndZ=0
    g1: LineSegment StartX=-201.368 StartY=36.3521 StartZ=0 EndX=-204.932 EndY=26.5605 EndZ=0
    g2: LineSegment StartX=-201.368 StartY=36.3521 StartZ=0 EndX=-180.2 EndY=28.6477 EndZ=0
    g3: LineSegment StartX=-180.2 StartY=28.6477 StartZ=0 EndX=-183.764 EndY=18.8561 EndZ=0
    g4: LineSegment StartX=-183.764 StartY=18.8561 StartZ=0 EndX=-204.932 EndY=26.5605 EndZ=0
  constraints (14):
    c: Parallel(g0,g-3)
    c: Distance(g0) = 4.405
    c: Coincident(g0,g-3)
    c: Coincident(g2,g1)
    c: Coincident(g3,g2)
    c: Coincident(g4,g3)
    c: Coincident(g4,g1)
    c: Parallel(g1,g-3)
    c: Distance(g1) = 10.42
    c: Coincident(g1,g0)
    c: Parallel(g2,g4)
    c: Perpendicular(g1,g2)
    c: DistanceX(g-4,g2) = 5
    c: Parallel(g3,g1)
FEATURE [Part::Extrusion] Extrude006  label="Extrude buco neopixel"
  Base = -> Sketch010
  Dir = (0,-1,2e-16)
  DirMode = 2
  FaceMakerClass = Part::FaceMakerBullseye
  FaceMakerMode = 3
  LengthFwd = 17.2
  LengthRev = 0
  Solid = true
  Symmetric = true
FEATURE [Sketcher::SketchObject] Sketch011  label="fermo grilletto"
  ArcFitTolerance = 1e-06
  AttachmentSupport = -> [XZ_Plane]
  ExternalGeometry = -> [Sketch]
  FullyConstrained = true
  MakeInternals = false
  MapMode = 5
  Placement = pos=(0,0,0) rot=(1,0,0;1.5708rad)
  sketch-geometry (18):
    g0: LineSegment [constr] StartX=-145.51 StartY=22 StartZ=0 EndX=-157.347 EndY=-14.4293 EndZ=0
    g1: LineSegment [constr] StartX=-157.347 StartY=-14.4293 StartZ=0 EndX=-157.841 EndY=-15.951 EndZ=0
    g2: LineSegment StartX=-161.151 StartY=-13.1932 StartZ=0 EndX=-155.825 EndY=-14.9237 EndZ=0
    g3: LineSegment StartX=-163.167 StartY=-14.2205 StartZ=0 EndX=-164.403 EndY=-18.0247 EndZ=0
    g4: LineSegment StartX=-163.376 StartY=-20.0408 StartZ=0 EndX=-158.05 EndY=-21.7713 EndZ=0
    g5: LineSegment StartX=-158.05 StartY=-21.7713 StartZ=0 EndX=-155.825 EndY=-14.9237 EndZ=0
    g6: LineSegment StartX=-161.645 StartY=-14.7149 StartZ=0 EndX=-157.841 EndY=-15.951 EndZ=0
    g7: LineSegment StartX=-157.841 StartY=-15.951 StartZ=0 EndX=-159.077 EndY=-19.7552 EndZ=0
    g8: LineSegment StartX=-159.077 StartY=-19.7552 StartZ=0 EndX=-162.881 EndY=-18.5191 EndZ=0
    g9: LineSegment StartX=-162.881 StartY=-18.5191 StartZ=0 EndX=-161.645 EndY=-14.7149 EndZ=0
    g10: LineSegment [constr] StartX=-161.645 StartY=-14.7149 StartZ=0 EndX=-161.151 EndY=-13.1932 EndZ=0
    g11: LineSegment [constr] StartX=-159.077 StartY=-19.7552 StartZ=0 EndX=-157.555 EndY=-20.2496 EndZ=0
    g12: LineSegment [constr] StartX=-159.077 StartY=-19.7552 StartZ=0 EndX=-159.572 EndY=-21.2769 EndZ=0
    g13: LineSegment [constr] StartX=-161.645 StartY=-14.7149 StartZ=0 EndX=-163.167 EndY=-14.2205 EndZ=0
    g14: ArcOfCircle CenterX=-161.645 CenterY=-14.7149 CenterZ=0 NormalX=0 NormalY=0 NormalZ=1 AngleXU=0 Radius=1.6 StartAngle=1.25664 EndAngle=2.82743
    g15: GeomPoint [constr] X=-162.673 Y=-12.6988 Z=0
    g16: ArcOfCircle CenterX=-162.881 CenterY=-18.5191 CenterZ=0 NormalX=0 NormalY=0 NormalZ=1 AngleXU=0 Radius=1.6 StartAngle=2.82743 EndAngle=4.39823
    g17: GeomPoint [constr] X=-164.897 Y=-19.5464 Z=0
  constraints (48):
    c: Parallel(g0,g-3)
    c: Distance(g0) = 38.304
    c: Coincident(g0,g-3)
    c: Parallel(g1,g-3)
    c: Distance(g1) = 1.6
    c: Coincident(g1,g0)
    c: Coincident(g5,g4)
    c: Coincident(g5,g2)
    c: Coincident(g7,g6)
    c: Coincident(g8,g7)
    c: Coincident(g9,g8)
    c: Coincident(g9,g6)
    c: Parallel(g7,g-3)
    c: Parallel(g9,g7)
    c: Perpendicular(g6,g7)
    c: Parallel(g6,g8)
    c: Distance(g6) = 4
    c: Distance(g9) = 4
    c: Parallel(g5,g7)
    c: Parallel(g9,g3)
    c: Parallel(g2,g6)
    c: Parallel(g4,g8)
    c: Parallel(g13,g6)
    c: Parallel(g10,g9)
    c: Parallel(g11,g8)
    c: Parallel(g12,g7)
    c: Distance(g10) = 1.6
    c: Distance(g13) = 1.6
    c: Distance(g12) = 1.6
    c: Distance(g11) = 1.6
    c: Coincident(g10,g6)
    c: Coincident(g13,g6)
    c: Coincident(g12,g7)
    c: Coincident(g11,g7)
    c: Distance(g10,g15) = 1.6
    c: Distance(g15,g13) = 1.6
    c: Distance(g4,g12) = 1.6
    c: Distance(g4,g11) = 1.6
    c: PointOnObject(g15,g2)
    c: Tangent(g3,g14) = -1.5708
    c: Tangent(g2,g14) = 1.5708
    c: PointOnObject(g17,g4)
    c: PointOnObject(g17,g3)
    c: Tangent(g4,g16) = -1.5708
    c: Tangent(g3,g16) = -1.5708
    c: Equal(g16,g14)
    c: Coincident(g16,g8)
    c: Coincident(g6,g1)
FEATURE [Part::Extrusion] Extrude007  label="Extrude fermo grilletto"
  Base = -> Sketch011
  Dir = (0,-1,2e-16)
  DirMode = 2
  FaceMakerClass = Part::FaceMakerBullseye
  FaceMakerMode = 3
  LengthFwd = 25.2
  LengthRev = 0
  Solid = true
  Symmetric = true
FEATURE [Sketcher::SketchObject] Sketch012  label="buco oled"
  ArcFitTolerance = 1e-06
  AttachmentSupport = -> [XZ_Plane]
  ExternalGeometry = -> [Sketch]
  FullyConstrained = true
  MakeInternals = false
  MapMode = 5
  Placement = pos=(0,0,0) rot=(1,0,0;1.5708rad)
  sketch-geometry (4):
    g0: LineSegment StartX=-185.747 StartY=58.0965 StartZ=0 EndX=-180.232 EndY=56.0891 EndZ=0
    g1: LineSegment StartX=-185.747 StartY=58.0965 StartZ=0 EndX=-185.747 EndY=67.3588 EndZ=0
    g2: LineSegment StartX=-185.747 StartY=67.3588 StartZ=0 EndX=-180.232 EndY=67.3588 EndZ=0
    g3: LineSegment StartX=-180.232 StartY=67.3588 StartZ=0 EndX=-180.232 EndY=56.0891 EndZ=0
  constraints (10):
    c: Coincident(g1,g0)
    c: Coincident(g2,g1)
    c: Coincident(g3,g2)
    c: Coincident(g3,g0)
    c: Parallel(g1,g-5)
    c: Perpendicular(g-3,g0)
    c: Parallel(g2,g-6)
    c: Parallel(g3,g-4)
    c: Coincident(g0,g-5)
    c: Coincident(g2,g-6)
FEATURE [Part::Extrusion] Extrude008  label="Extrude buco oled"
  Base = -> Sketch012
  Dir = (0,-1,2e-16)
  DirMode = 2
  FaceMakerClass = Part::FaceMakerBullseye
  FaceMakerMode = 3
  LengthFwd = 12.8
  LengthRev = 0
  Solid = true
  Symmetric = true
FEATURE [Sketcher::SketchObject] Sketch013  label="buco pompa"
  ArcFitTolerance = 1e-06
  AttachmentSupport = -> [XZ_Plane]
  ExternalGeometry = -> [Sketch]
  FullyConstrained = true
  MakeInternals = false
  MapMode = 5
  Placement = pos=(0,0,0) rot=(1,0,0;1.5708rad)
  sketch-geometry (8):
    g0: LineSegment StartX=-82.8 StartY=-10.4 StartZ=0 EndX=-82.8 EndY=-9.6 EndZ=0
    g1: LineSegment StartX=-82.8 StartY=-9.6 StartZ=0 EndX=-67.9 EndY=-9.6 EndZ=0
    g2: LineSegment StartX=-67.9 StartY=-9.6 StartZ=0 EndX=-67.9 EndY=6 EndZ=0
    g3: LineSegment StartX=-67.9 StartY=6 StartZ=0 EndX=-65.9 EndY=6 EndZ=0
    g4: LineSegment StartX=-65.9 StartY=6 StartZ=0 EndX=-65.9 EndY=-1.7 EndZ=0
    g5: LineSegment StartX=-65.9 StartY=-1.7 StartZ=0 EndX=-57.2 EndY=-1.7 EndZ=0
    g6: LineSegment StartX=-57.2 StartY=-1.7 StartZ=0 EndX=-57.2 EndY=-10.4 EndZ=0
    g7: LineSegment StartX=-57.2 StartY=-10.4 StartZ=0 EndX=-82.8 EndY=-10.4 EndZ=0
  constraints (22):
    c: Vertical(g0)
    c: Coincident(g1,g0)
    c: Horizontal(g1)
    c: Coincident(g2,g1)
    c: Vertical(g2)
    c: Coincident(g3,g2)
    c: Horizontal(g3)
    c: Coincident(g4,g3)
    c: Vertical(g4)
    c: Coincident(g5,g4)
    c: Horizontal(g5)
    c: Coincident(g6,g5)
    c: Vertical(g6)
    c: Coincident(g7,g6)
    c: Coincident(g7,g0)
    c: DistanceY(g0,g0) = 0.8
    c: DistanceY(g6,g6) = 8.7
    c: DistanceX(g1,g1) = 14.9
    c: DistanceX(g3,g3) = 2
    c: Coincident(g0,g-4)
    c: DistanceY(g2,g-6) = 0
    c: Coincident(g6,g-5)
FEATURE [Part::Extrusion] Extrude009  label="Extrude buco pompa"
  Base = -> Sketch013
  Dir = (0,-1,2e-16)
  DirMode = 2
  FaceMakerClass = Part::FaceMakerBullseye
  FaceMakerMode = 3
  LengthFwd = 13.2
  LengthRev = 0
  Solid = true
  Symmetric = true
FEATURE [Sketcher::SketchObject] Sketch014  label="buco frontale"
  ArcFitTolerance = 1e-06
  AttachmentSupport = -> [XZ_Plane]
  ExternalGeometry = -> [Sketch]
  FullyConstrained = true
  MakeInternals = false
  MapMode = 5
  Placement = pos=(0,0,0) rot=(1,0,0;1.5708rad)
  sketch-geometry (10):
    g0: LineSegment StartX=0 StartY=0 StartZ=0 EndX=0 EndY=24.671 EndZ=0
    g1: LineSegment StartX=0 StartY=24.671 StartZ=0 EndX=-4 EndY=24.671 EndZ=0
    g2: LineSegment StartX=-4 StartY=24.671 StartZ=0 EndX=-4 EndY=16 EndZ=0
    g3: LineSegment StartX=-4 StartY=16 StartZ=0 EndX=-2.4 EndY=16 EndZ=0
    g4: LineSegment StartX=-2.4 StartY=16 StartZ=0 EndX=-2.4 EndY=10 EndZ=0
    g5: LineSegment StartX=-2.4 StartY=10 StartZ=0 EndX=-12 EndY=10 EndZ=0
    g6: LineSegment StartX=-12 StartY=10 StartZ=0 EndX=-12 EndY=6 EndZ=0
    g7: LineSegment StartX=-12 StartY=6 StartZ=0 EndX=-2.4 EndY=6 EndZ=0
    g8: LineSegment StartX=-2.4 StartY=6 StartZ=0 EndX=-2.4 EndY=0 EndZ=0
    g9: LineSegment StartX=-2.4 StartY=0 StartZ=0 EndX=0 EndY=0 EndZ=0
  constraints (29):
    c: Vertical(g0)
    c: Coincident(g1,g0)
    c: Horizontal(g1)
    c: Coincident(g2,g1)
    c: Vertical(g2)
    c: Coincident(g3,g2)
    c: Horizontal(g3)
    c: Coincident(g4,g3)
    c: Vertical(g4)
    c: Coincident(g5,g4)
    c: Horizontal(g5)
    c: Coincident(g6,g5)
    c: Vertical(g6)
    c: Coincident(g7,g6)
    c: Coincident(g8,g7)
    c: Vertical(g8)
    c: Coincident(g9,g8)
    c: Coincident(g9,g0)
    c: Horizontal(g9)
    c: DistanceY(g0,g0) = 24.671
    c: Horizontal(g7)
    c: DistanceY(g6,g6) = 4
    c: DistanceY(g4,g4) = 6
    c: DistanceX(g9,g9) = 2.4
    c: Coincident(g0,g-1)
    c: DistanceY(g-3,g7) = 0
    c: DistanceX(g8,g4) = 0
    c: DistanceX(g-3,g1) = 0
    c: DistanceX(g6,g-3) = 8
FEATURE [Part::Extrusion] Extrude010  label="Extrude buco frontale"
  Base = -> Sketch014
  Dir = (0,-1,2e-16)
  DirMode = 2
  FaceMakerClass = Part::FaceMakerBullseye
  FaceMakerMode = 3
  LengthFwd = 11.2
  LengthRev = 0
  Solid = true
  Symmetric = true
FEATURE [Sketcher::SketchObject] Sketch015  label="guida rail"
  ArcFitTolerance = 1e-06
  AttachmentSupport = -> [XZ_Plane]
  ExternalGeometry = -> [Sketch]
  FullyConstrained = true
  MakeInternals = false
  MapMode = 5
  Placement = pos=(0,0,0) rot=(1,0,0;1.5708rad)
  sketch-geometry (4):
    g0: LineSegment StartX=-100.8 StartY=43.2 StartZ=0 EndX=-44.6 EndY=43.2 EndZ=0
    g1: LineSegment StartX=-44.6 StartY=43.2 StartZ=0 EndX=-44.6 EndY=41.2 EndZ=0
    g2: LineSegment StartX=-44.6 StartY=41.2 StartZ=0 EndX=-100.8 EndY=41.2 EndZ=0
    g3: LineSegment StartX=-100.8 StartY=41.2 StartZ=0 EndX=-100.8 EndY=43.2 EndZ=0
  constraints (9):
    c: Horizontal(g0)
    c: Coincident(g1,g0)
    c: Coincident(g2,g1)
    c: Coincident(g3,g2)
    c: Coincident(g3,g0)
    c: Vertical(g3)
    c: Coincident(g2,g-3)
    c: Coincident(g1,g-3)
    c: Coincident(g0,g-4)
FEATURE [Part::Extrusion] Extrude011  label="Extrude guida rail"
  Base = -> Sketch015
  Dir = (0,-1,2e-16)
  DirMode = 2
  FaceMakerClass = Part::FaceMakerBullseye
  FaceMakerMode = 3
  LengthFwd = 9
  LengthRev = 0
  Solid = true
  Symmetric = true
FEATURE [Sketcher::SketchObject] Sketch016  label="guide per coperture laterali"
  ArcFitTolerance = 1e-06
  AttachmentSupport = -> [XZ_Plane]
  ExternalGeometry = -> [Sketch]
  FullyConstrained = true
  MakeInternals = false
  MapMode = 5
  Placement = pos=(0,0,0) rot=(1,0,0;1.5708rad)
  sketch-geometry (14):
    g0: Circle CenterX=-5.6 CenterY=7.6 CenterZ=0 NormalX=0 NormalY=0 NormalZ=1 AngleXU=0 Radius=1.6
    g1: Circle CenterX=-5.6 CenterY=7.6 CenterZ=0 NormalX=0 NormalY=0 NormalZ=1 AngleXU=0 Radius=4
    g2: Circle CenterX=-5.6 CenterY=34.8 CenterZ=0 NormalX=0 NormalY=0 NormalZ=1 AngleXU=0 Radius=1.6
    g3: Circle CenterX=-5.6 CenterY=34.8 CenterZ=0 NormalX=0 NormalY=0 NormalZ=1 AngleXU=0 Radius=4
    g4: Circle CenterX=-184.08 CenterY=34.8 CenterZ=0 NormalX=0 NormalY=0 NormalZ=1 AngleXU=0 Radius=1.6
    g5: Circle CenterX=-184.08 CenterY=34.8 CenterZ=0 NormalX=0 NormalY=0 NormalZ=1 AngleXU=0 Radius=4
    g6: Circle CenterX=-179.305 CenterY=-76.8316 CenterZ=0 NormalX=0 NormalY=0 NormalZ=1 AngleXU=0 Radius=1.6
    g7: Circle CenterX=-179.305 CenterY=-76.8316 CenterZ=0 NormalX=0 NormalY=0 NormalZ=1 AngleXU=0 Radius=4
    g8: Circle CenterX=-213.443 CenterY=-76.8316 CenterZ=0 NormalX=0 NormalY=0 NormalZ=1 AngleXU=0 Radius=1.6
    g9: Circle CenterX=-213.443 CenterY=-76.8316 CenterZ=0 NormalX=0 NormalY=0 NormalZ=1 AngleXU=0 Radius=4
    g10: Circle CenterX=-78.51 CenterY=7.6 CenterZ=0 NormalX=0 NormalY=0 NormalZ=1 AngleXU=0 Radius=1.6
    g11: Circle CenterX=-78.51 CenterY=7.6 CenterZ=0 NormalX=0 NormalY=0 NormalZ=1 AngleXU=0 Radius=4
    g12: Circle CenterX=-78.51 CenterY=34.8 CenterZ=0 NormalX=0 NormalY=0 NormalZ=1 AngleXU=0 Radius=1.6
    g13: Circle CenterX=-78.51 CenterY=34.8 CenterZ=0 NormalX=0 NormalY=0 NormalZ=1 AngleXU=0 Radius=4
  constraints (35):
    c: Diameter(g0) = 3.2
    c: Diameter(g1) = 8
    c: Coincident(g0,g1)
    c: Diameter(g2) = 3.2
    c: Diameter(g3) = 8
    c: Coincident(g3,g2)
    c: Tangent(g2,g-7)
    c: Diameter(g4) = 3.2
    c: Diameter(g5) = 8
    c: Coincident(g5,g4)
    c: Tangent(g4,g-7)
    c: Tangent(g4,g-8)
    c: Diameter(g6) = 3.2
    c: Diameter(g7) = 8
    c: Coincident(g7,g6)
    c: Tangent(g6,g-9)
    c: Tangent(g6,g-10)
    c: Diameter(g8) = 3.2
    c: Diameter(g9) = 8
    c: Coincident(g9,g8)
    c: Tangent(g8,g-10)
    c: Tangent(g8,g-11)
    c: Diameter(g10) = 3.2
    c: Diameter(g11) = 8
    c: Diameter(g12) = 3.2
    c: Diameter(g13) = 8
    c: Coincident(g12,g13)
    c: Coincident(g10,g11)
    c: Tangent(g12,g-7)
    c: DistanceX(g12,g10) = 0
    c: Tangent(g2,g-6)
    c: Tangent(g0,g-6)
    c: Tangent(g0,g-3)
    c: Tangent(g10,g-3)
    c: Tangent(g10,g-4)
FEATURE [Part::Extrusion] Extrude012  label="extrude guide per coperture laterali"
  Base = -> Sketch016
  Dir = (0,-1,2e-16)
  DirMode = 2
  FaceMakerClass = Part::FaceMakerBullseye
  FaceMakerMode = 3
  LengthFwd = 25.2
  LengthRev = 0
  Solid = true
  Symmetric = true
FEATURE [Sketcher::SketchObject] Sketch017  label="supporto CAM"
  ArcFitTolerance = 1e-06
  AttachmentSupport = -> [XZ_Plane]
  ExternalGeometry = -> [Sketch]
  FullyConstrained = true
  MakeInternals = false
  MapMode = 5
  Placement = pos=(0,0,0) rot=(1,0,0;1.5708rad)
  sketch-geometry (6):
    g0: LineSegment StartX=-2.4 StartY=48 StartZ=0 EndX=-2.4 EndY=41.2 EndZ=0
    g1: LineSegment StartX=-2.4 StartY=48 StartZ=0 EndX=-34 EndY=48 EndZ=0
    g2: LineSegment StartX=-34 StartY=48 StartZ=0 EndX=-34 EndY=46.72 EndZ=0
    g3: LineSegment StartX=-34 StartY=46.72 StartZ=0 EndX=-36 EndY=46.72 EndZ=0
    g4: LineSegment StartX=-36 StartY=46.72 StartZ=0 EndX=-36 EndY=41.2 EndZ=0
    g5: LineSegment StartX=-36 StartY=41.2 StartZ=0 EndX=-2.4 EndY=41.2 EndZ=0
  constraints (15):
    c: Coincident(g1,g0)
    c: Horizontal(g1)
    c: Coincident(g2,g1)
    c: Vertical(g2)
    c: Coincident(g3,g2)
    c: Horizontal(g3)
    c: Coincident(g4,g3)
    c: Coincident(g5,g4)
    c: DistanceX(g1,g0) = 31.6
    c: Coincident(g5,g0)
    c: Vertical(g4)
    c: DistanceY(g2,g1) = 1.28
    c: Coincident(g0,g-3)
    c: Coincident(g0,g-3)
    c: Coincident(g4,g-4)
FEATURE [Part::Extrusion] Extrude013  label="Extrude supporto CAM"
  Base = -> Sketch017
  Dir = (0,-1,2e-16)
  DirMode = 2
  FaceMakerClass = Part::FaceMakerBullseye
  FaceMakerMode = 3
  LengthFwd = 17.8
  LengthRev = 0
  Solid = true
  Symmetric = true
FEATURE [Sketcher::SketchObject] Sketch018  label="Scavo CAM"
  ArcFitTolerance = 1e-06
  AttachmentSupport = -> [YZ_Plane]
  ExternalGeometry = -> [Sketch]
  FullyConstrained = true
  MakeInternals = false
  MapMode = 5
  Placement = pos=(0,0,0) rot=(0.57735,0.57735,0.57735;2.0944rad)
  sketch-geometry (4):
    g0: LineSegment StartX=-7.73 StartY=48 StartZ=0 EndX=7.73 EndY=48 EndZ=0
    g1: LineSegment [constr] StartX=1.07e-14 StartY=48 StartZ=0 EndX=0 EndY=43.5155 EndZ=0
    g2: ArcOfCircle CenterX=9e-15 CenterY=52.42 CenterZ=0 NormalX=0 NormalY=0 NormalZ=1 AngleXU=0 Radius=8.90445 StartAngle=3.66102 EndAngle=5.76376
    g3: Circle [constr] CenterX=9e-15 CenterY=52.42 CenterZ=0 NormalX=0 NormalY=0 NormalZ=1 AngleXU=0 Radius=8.9
  constraints (13):
    c: Horizontal(g0)
    c: DistanceY(g-3,g0) = 0
    c: DistanceX(g0,g0) = 15.46
    c: DistanceX(g0,g-3) = 7.73
    c: DistanceX(g-3) = 0
    c: Coincident(g1,g-3)
    c: PointOnObject(g1,g-2)
    c: Coincident(g2,g0)
    c: Coincident(g2,g0)
    c: PointOnObject(g1,g2)
    c: Diameter(g3) = 17.8
    c: DistanceY(g1,g3) = 4.42
    c: Coincident(g2,g3)
FEATURE [Part::Extrusion] Extrude014  label="Extrude Scavo CAM"
  Base = -> Sketch018
  Dir = (1,0,0)
  DirMode = 2
  FaceMakerClass = Part::FaceMakerBullseye
  FaceMakerMode = 3
  LengthFwd = -34
  LengthRev = 0
  Solid = true
  Symmetric = false
FEATURE [Sketcher::SketchObject] Sketch019  label="scavo rumble"
  ArcFitTolerance = 1e-06
  AttachmentSupport = -> [XZ_Plane]
  ExternalGeometry = -> [Sketch]
  FullyConstrained = true
  MakeInternals = false
  MapMode = 5
  Placement = pos=(0,0,0) rot=(1,0,0;1.5708rad)
  sketch-geometry (6):
    g0: LineSegment StartX=-164.575 StartY=-24.3786 StartZ=0 EndX=-159.439 EndY=-26.0473 EndZ=0
    g1: LineSegment StartX=-159.439 StartY=-26.0473 StartZ=0 EndX=-166.547 EndY=-47.9216 EndZ=0
    g2: LineSegment StartX=-166.547 StartY=-47.9216 StartZ=0 EndX=-171.682 EndY=-46.2529 EndZ=0
    g3: LineSegment StartX=-171.682 StartY=-46.2529 StartZ=0 EndX=-164.575 EndY=-24.3786 EndZ=0
    g4: LineSegment [constr] StartX=-145.51 StartY=22 StartZ=0 EndX=-160.961 EndY=-25.5528 EndZ=0
    g5: LineSegment [constr] StartX=-159.439 StartY=-26.0473 StartZ=0 EndX=-160.961 EndY=-25.5528 EndZ=0
  constraints (17):
    c: Coincident(g1,g0)
    c: Coincident(g2,g1)
    c: Coincident(g3,g2)
    c: Coincident(g3,g0)
    c: Parallel(g3,g-3)
    c: Parallel(g3,g1)
    c: Perpendicular(g3,g0)
    c: Perpendicular(g2,g3)
    c: Distance(g2,g0) = 23
    c: Parallel(g4,g-3)
    c: Distance(g4) = 50
    c: Coincident(g4,g-3)
    c: Parallel(g5,g0)
    c: Distance(g5) = 1.6
    c: Coincident(g5,g0)
    c: Distance(g5,g0) = 3.8
    c: Coincident(g5,g4)
FEATURE [Part::Extrusion] Extrude015  label="scavo rumble001"
  Base = -> Sketch019
  Dir = (0,-1,2e-16)
  DirMode = 2
  FaceMakerClass = Part::FaceMakerBullseye
  FaceMakerMode = 3
  LengthFwd = 21
  LengthRev = 0
  Solid = true
  Symmetric = true
FEATURE [Sketcher::SketchObject] Sketch020  label="fermo rumble"
  ArcFitTolerance = 1e-06
  AttachmentSupport = -> [XZ_Plane]
  ExternalGeometry = -> [Sketch019,Sketch]
  FullyConstrained = true
  MakeInternals = false
  MapMode = 5
  Placement = pos=(0,0,0) rot=(1,0,0;1.5708rad)
  sketch-geometry (16):
    g0: LineSegment [constr] StartX=-166.709 StartY=-43.2425 StartZ=0 EndX=-168.068 EndY=-47.4271 EndZ=0
    g1: LineSegment [constr] StartX=-168.068 StartY=-47.4271 StartZ=0 EndX=-166.547 EndY=-47.9216 EndZ=0
    g2: LineSegment StartX=-168.121 StartY=-40.4703 StartZ=0 EndX=-166.029 EndY=-41.1502 EndZ=0
    g3: LineSegment StartX=-166.029 StartY=-41.1502 StartZ=0 EndX=-166.709 EndY=-43.2425 EndZ=0
    g4: LineSegment StartX=-166.709 StartY=-43.2425 StartZ=0 EndX=-168.801 EndY=-42.5626 EndZ=0
    g5: LineSegment StartX=-168.801 StartY=-42.5626 StartZ=0 EndX=-168.121 EndY=-40.4703 EndZ=0
    g6: LineSegment StartX=-167.627 StartY=-38.9486 StartZ=0 EndX=-164.203 EndY=-40.0611 EndZ=0
    g7: LineSegment StartX=-164.203 StartY=-40.0611 StartZ=0 EndX=-165.81 EndY=-45.0066 EndZ=0
    g8: LineSegment StartX=-165.81 StartY=-45.0066 StartZ=0 EndX=-169.234 EndY=-43.8941 EndZ=0
    g9: LineSegment StartX=-170.261 StartY=-41.878 StartZ=0 EndX=-169.643 EndY=-39.9759 EndZ=0
    g10: LineSegment [constr] StartX=-169.643 StartY=-39.9759 StartZ=0 EndX=-169.148 EndY=-38.4542 EndZ=0
    g11: LineSegment [constr] StartX=-169.148 StartY=-38.4542 StartZ=0 EndX=-167.627 EndY=-38.9486 EndZ=0
    g12: ArcOfCircle CenterX=-168.739 CenterY=-42.3724 CenterZ=0 NormalX=0 NormalY=0 NormalZ=1 AngleXU=0 Radius=1.6 StartAngle=2.82743 EndAngle=4.39823
    g13: GeomPoint [constr] X=-170.755 Y=-43.3997 Z=0
    g14: ArcOfCircle CenterX=-168.121 CenterY=-40.4703 CenterZ=0 NormalX=0 NormalY=0 NormalZ=1 AngleXU=0 Radius=1.6 StartAngle=1.25664 EndAngle=2.82743
    g15: GeomPoint [constr] X=-169.148 Y=-38.4542 Z=0
  constraints (42):
    c: Parallel(g0,g-4)
    c: Distance(g0) = 4.4
    c: Coincident(g1,g0)
    c: Perpendicular(g0,g1)
    c: Distance(g1) = 1.6
    c: Coincident(g1,g-5)
    c: Coincident(g3,g2)
    c: Coincident(g4,g3)
    c: Coincident(g5,g4)
    c: Coincident(g5,g2)
    c: Parallel(g3,g-4)
    c: Parallel(g3,g5)
    c: Perpendicular(g2,g3)
    c: Parallel(g4,g2)
    c: Distance(g2) = 2.2
    c: Distance(g3) = 2.2
    c: Coincident(g7,g6)
    c: Coincident(g8,g7)
    c: Parallel(g7,g-4)
    c: Parallel(g7,g9)
    c: Perpendicular(g6,g7)
    c: Parallel(g6,g8)
    c: Distance(g6,g15) = 5.2
    c: Distance(g7) = 5.2
    c: Coincident(g11,g10)
    c: Parallel(g10,g9)
    c: Parallel(g11,g6)
    c: Distance(g10) = 1.6
    c: Distance(g11) = 1.6
    c: Coincident(g10,g15)
    c: Distance(g11,g2) = 1.6
    c: Distance(g2,g10) = 1.6
    c: PointOnObject(g13,g8)
    c: PointOnObject(g13,g9)
    c: Tangent(g8,g12) = 1.5708
    c: Tangent(g9,g12) = 1.5708
    c: PointOnObject(g15,g9)
    c: Tangent(g6,g14) = 1.5708
    c: Tangent(g9,g14) = 1.5708
    c: Equal(g12,g14)
    c: Coincident(g6,g11)
    c: Coincident(g3,g0)
FEATURE [Part::Extrusion] Extrude016  label="Extrude fermo rumble"
  Base = -> Sketch020
  Dir = (0,-1,2e-16)
  DirMode = 2
  FaceMakerClass = Part::FaceMakerBullseye
  FaceMakerMode = 3
  LengthFwd = 25.2
  LengthRev = 0
  Solid = true
  Symmetric = true
FEATURE [Sketcher::SketchObject] Sketch021  label="perno fermo rumble001"
  ArcFitTolerance = 1e-06
  AttachmentSupport = -> [XZ_Plane001]
  FullyConstrained = true
  MakeInternals = false
  MapMode = 5
  Placement = pos=(0,0,0) rot=(1,0,0;1.5708rad)
  sketch-geometry (16):
    g0: LineSegment StartX=0 StartY=0.45 StartZ=0 EndX=0 EndY=1.55 EndZ=0
    g1: LineSegment StartX=0.45 StartY=2 StartZ=0 EndX=1.55 EndY=2 EndZ=0
    g2: LineSegment StartX=2 StartY=1.55 StartZ=0 EndX=2 EndY=0.45 EndZ=0
    g3: LineSegment StartX=1.55 StartY=0 StartZ=0 EndX=0.45 EndY=0 EndZ=0
    g4: ArcOfCircle [constr] CenterX=0.45 CenterY=1.55 CenterZ=0 NormalX=0 NormalY=0 NormalZ=1 AngleXU=0 Radius=0.45 StartAngle=1.5708 EndAngle=3.14159
    g5: GeomPoint [constr] X=0 Y=2 Z=0
    g6: LineSegment StartX=0.45 StartY=2 StartZ=0 EndX=0 EndY=1.55 EndZ=0
    g7: ArcOfCircle [constr] CenterX=1.55 CenterY=1.55 CenterZ=0 NormalX=0 NormalY=0 NormalZ=1 AngleXU=0 Radius=0.45 StartAngle=0 EndAngle=1.5708
    g8: GeomPoint [constr] X=2 Y=2 Z=0
    g9: LineSegment StartX=2 StartY=1.55 StartZ=0 EndX=1.55 EndY=2 EndZ=0
    g10: ArcOfCircle [constr] CenterX=1.55 CenterY=0.45 CenterZ=0 NormalX=0 NormalY=0 NormalZ=1 AngleXU=0 Radius=0.45 StartAngle=4.71239 EndAngle=6.28319
    g11: GeomPoint [constr] X=2 Y=0 Z=0
    g12: LineSegment StartX=1.55 StartY=0 StartZ=0 EndX=2 EndY=0.45 EndZ=0
    g13: ArcOfCircle [constr] CenterX=0.45 CenterY=0.45 CenterZ=0 NormalX=0 NormalY=0 NormalZ=1 AngleXU=0 Radius=0.45 StartAngle=3.14159 EndAngle=4.71239
    g14: GeomPoint [constr] X=0 Y=0 Z=0
    g15: LineSegment StartX=0 StartY=0.45 StartZ=0 EndX=0.45 EndY=0 EndZ=0
  constraints (35):
    c: Coincident(g14,g-1)
    c: PointOnObject(g5,g-2)
    c: Horizontal(g1)
    c: Vertical(g2)
    c: Horizontal(g3)
    c: DistanceX(g5,g8) = 2
    c: DistanceY(g11,g8) = 2
    c: PointOnObject(g5,g0)
    c: PointOnObject(g5,g1)
    c: Tangent(g0,g4) = 1.5708
    c: Tangent(g1,g4) = 1.5708
    c: Coincident(g6,g0)
    c: Coincident(g6,g1)
    c: PointOnObject(g8,g2)
    c: PointOnObject(g8,g1)
    c: Tangent(g2,g7) = 1.5708
    c: Tangent(g1,g7) = 1.5708
    c: Coincident(g9,g2)
    c: Coincident(g9,g1)
    c: PointOnObject(g11,g2)
    c: PointOnObject(g11,g3)
    c: Tangent(g2,g10) = 1.5708
    c: Tangent(g3,g10) = 1.5708
    c: Coincident(g12,g2)
    c: Coincident(g12,g3)
    c: PointOnObject(g14,g0)
    c: PointOnObject(g14,g3)
    c: Tangent(g0,g13) = 1.5708
    c: Tangent(g3,g13) = 1.5708
    c: Coincident(g15,g0)
    c: Coincident(g15,g3)
    c: Equal(g6,g9)
    c: Equal(g9,g12)
    c: Equal(g12,g15)
    c: DistanceX(g14,g3) = 0.45
FEATURE [Sketcher::SketchObject] Sketch022  label="fori per M3x5(OD)x6(L)"
  ArcFitTolerance = 1e-06
  AttachmentSupport = -> [XZ_Plane]
  ExternalGeometry = -> [Sketch016]
  FullyConstrained = true
  MakeInternals = false
  MapMode = 5
  Placement = pos=(0,0,0) rot=(1,0,0;1.5708rad)
  sketch-geometry (7):
    g0: Circle CenterX=-5.6 CenterY=34.8 CenterZ=0 NormalX=0 NormalY=0 NormalZ=1 AngleXU=0 Radius=2.5
    g1: Circle CenterX=-5.6 CenterY=7.6 CenterZ=0 NormalX=0 NormalY=0 NormalZ=1 AngleXU=0 Radius=2.5
    g2: Circle CenterX=-78.51 CenterY=34.8 CenterZ=0 NormalX=0 NormalY=0 NormalZ=1 AngleXU=0 Radius=2.5
    g3: Circle CenterX=-78.51 CenterY=7.6 CenterZ=0 NormalX=0 NormalY=0 NormalZ=1 AngleXU=0 Radius=2.5
    g4: Circle CenterX=-184.08 CenterY=34.8 CenterZ=0 NormalX=0 NormalY=0 NormalZ=1 AngleXU=0 Radius=2.5
    g5: Circle CenterX=-179.305 CenterY=-76.8316 CenterZ=0 NormalX=0 NormalY=0 NormalZ=1 AngleXU=0 Radius=2.5
    g6: Circle CenterX=-213.443 CenterY=-76.8316 CenterZ=0 NormalX=0 NormalY=0 NormalZ=1 AngleXU=0 Radius=2.5
  constraints (14):
    c: Diameter(g0) = 5
    c: Diameter(g1) = 5
    c: Diameter(g2) = 5
    c: Diameter(g3) = 5
    c: Diameter(g4) = 5
    c: Diameter(g5) = 5
    c: Diameter(g6) = 5
    c: Coincident(g0,g-8)
    c: Coincident(g1,g-9)
    c: Coincident(g2,g-6)
    c: Coincident(g3,g-7)
    c: Coincident(g4,g-5)
    c: Coincident(g5,g-4)
    c: Coincident(g6,g-3)
FEATURE [Part::Extrusion] Extrude018  label="Extrude fori M3x5x6 - dx"
  Base = -> Sketch022
  Dir = (0,-1,2e-16)
  DirMode = 2
  FaceMakerClass = Part::FaceMakerBullseye
  FaceMakerMode = 3
  LengthFwd = 6.2
  LengthRev = 0
  Placement = pos=(0,-9.5,0) rot=(0,0,1;0rad)
  Solid = true
  Symmetric = true
FEATURE [Part::Extrusion] Extrude019  label="Extrude fori M3x5x6 - sx"
  Base = -> Sketch022
  Dir = (0,-1,2e-16)
  DirMode = 2
  FaceMakerClass = Part::FaceMakerBullseye
  FaceMakerMode = 3
  LengthFwd = 6.2
  LengthRev = 0
  Placement = pos=(0,9.5,0) rot=(0,0,1;0rad)
  Solid = true
  Symmetric = true
FEATURE [Sketcher::SketchObject] Sketch023  label="foro anteriore M3x5x6"
  ArcFitTolerance = 1e-06
  AttachmentSupport = -> [YZ_Plane]
  FullyConstrained = true
  MakeInternals = false
  MapMode = 5
  Placement = pos=(0,0,0) rot=(0.57735,0.57735,0.57735;2.0944rad)
  sketch-geometry (2):
    g0: LineSegment [constr] StartX=0 StartY=0 StartZ=0 EndX=0 EndY=38.6 EndZ=0
    g1: Circle CenterX=0 CenterY=38.6 CenterZ=0 NormalX=0 NormalY=0 NormalZ=1 AngleXU=0 Radius=2.5
  constraints (5):
    c: Coincident(g0,g-1)
    c: PointOnObject(g0,g-2)
    c: DistanceY(g0,g0) = 38.6
    c: Diameter(g1) = 5
    c: Coincident(g1,g0)
FEATURE [Part::Extrusion] Extrude020  label="Extrude foro anteriore M3x5x6"
  Base = -> Sketch023
  Dir = (1,0,0)
  DirMode = 2
  FaceMakerClass = Part::FaceMakerBullseye
  FaceMakerMode = 3
  LengthFwd = -6.2
  LengthRev = 0
  Solid = true
  Symmetric = false
FEATURE [Sketcher::SketchObject] Sketch024  label="fori per viti frontale"
  ArcFitTolerance = 1e-06
  AttachmentSupport = -> [YZ_Plane]
  FullyConstrained = true
  MakeInternals = false
  MapMode = 5
  Placement = pos=(0,0,0) rot=(0.57735,0.57735,0.57735;2.0944rad)
  sketch-geometry (9):
    g0: LineSegment [constr] StartX=-10.3 StartY=30.721 StartZ=0 EndX=10.3 EndY=30.721 EndZ=0
    g1: LineSegment [constr] StartX=10.3 StartY=30.721 StartZ=0 EndX=10.3 EndY=10.121 EndZ=0
    g2: LineSegment [constr] StartX=10.3 StartY=10.121 StartZ=0 EndX=-10.3 EndY=10.121 EndZ=0
    g3: LineSegment [constr] StartX=-10.3 StartY=10.121 StartZ=0 EndX=-10.3 EndY=30.721 EndZ=0
    g4: LineSegment [constr] StartX=0 StartY=0 StartZ=0 EndX=0 EndY=10.121 EndZ=0
    g5: Circle CenterX=-10.3 CenterY=30.721 CenterZ=0 NormalX=0 NormalY=0 NormalZ=1 AngleXU=0 Radius=2
    g6: Circle CenterX=10.3 CenterY=30.721 CenterZ=0 NormalX=0 NormalY=0 NormalZ=1 AngleXU=0 Radius=2
    g7: Circle CenterX=-10.3 CenterY=10.121 CenterZ=0 NormalX=0 NormalY=0 NormalZ=1 AngleXU=0 Radius=2
    g8: Circle CenterX=10.3 CenterY=10.121 CenterZ=0 NormalX=0 NormalY=0 NormalZ=1 AngleXU=0 Radius=2
  constraints (22):
    c: Horizontal(g0)
    c: Coincident(g1,g0)
    c: Vertical(g1)
    c: Coincident(g2,g1)
    c: Horizontal(g2)
    c: Coincident(g3,g2)
    c: Coincident(g3,g0)
    c: Vertical(g3)
    c: DistanceX(g0,g0) = 20.6
    c: DistanceY(g3,g3) = 20.6
    c: Coincident(g4,g-1)
    c: PointOnObject(g4,g-2)
    c: DistanceY(g4,g4) = 10.121
    c: Symmetric(g2,g2,g4)
    c: Diameter(g5) = 4
    c: Diameter(g6) = 4
    c: Diameter(g7) = 4
    c: Diameter(g8) = 4
    c: Coincident(g5,g0)
    c: Coincident(g6,g0)
    c: Coincident(g7,g2)
    c: Coincident(g8,g1)
FEATURE [Part::Extrusion] Extrude021  label="Extrude fori per viti frontale"
  Base = -> Sketch024
  Dir = (1,0,0)
  DirMode = 2
  FaceMakerClass = Part::FaceMakerBullseye
  FaceMakerMode = 3
  LengthFwd = -2.4
  LengthRev = 0
  Solid = true
  Symmetric = false
FEATURE [Sketcher::SketchObject] Sketch025  label="foro per filo CAM"
  ArcFitTolerance = 1e-06
  AttachmentSupport = -> [XZ_Plane]
  ExternalGeometry = -> [Sketch]
  FullyConstrained = true
  MakeInternals = false
  MapMode = 5
  Placement = pos=(0,0,0) rot=(1,0,0;1.5708rad)
  sketch-geometry (4):
    g0: LineSegment StartX=-44.6 StartY=41.2 StartZ=0 EndX=-44.6 EndY=36.4 EndZ=0
    g1: LineSegment StartX=-44.6 StartY=36.4 StartZ=0 EndX=-54.6 EndY=36.4 EndZ=0
    g2: LineSegment StartX=-54.6 StartY=36.4 StartZ=0 EndX=-50.4 EndY=41.2 EndZ=0
    g3: LineSegment StartX=-50.4 StartY=41.2 StartZ=0 EndX=-44.6 EndY=41.2 EndZ=0
  constraints (11):
    c: Vertical(g0)
    c: Coincident(g1,g0)
    c: Horizontal(g1)
    c: Coincident(g2,g1)
    c: Coincident(g3,g2)
    c: Coincident(g3,g0)
    c: Horizontal(g3)
    c: Coincident(g0,g-3)
    c: DistanceY(g0,g-4) = 0
    c: DistanceX(g3,g3) = 5.8
    c: DistanceX(g1,g1) = 10
FEATURE [Part::Extrusion] Extrude022  label="Extrude foro per filo CAM dx"
  Base = -> Sketch025
  Dir = (0,-1,2e-16)
  DirMode = 2
  FaceMakerClass = Part::FaceMakerBullseye
  FaceMakerMode = 3
  LengthFwd = 4.9
  LengthRev = 0
  Placement = pos=(0,6.95,0) rot=(0,0,1;0rad)
  Solid = true
  Symmetric = true
FEATURE [Part::Extrusion] Extrude023  label="Extrude foro per filo CAM sx"
  Base = -> Sketch025
  Dir = (0,-1,2e-16)
  DirMode = 2
  FaceMakerClass = Part::FaceMakerBullseye
  FaceMakerMode = 3
  LengthFwd = 4.9
  LengthRev = 0
  Placement = pos=(0,-6.95,0) rot=(0,0,1;0rad)
  Solid = true
  Symmetric = true
FEATURE [Sketcher::SketchObject] Sketch026  label="foro sotto anteriore M3x5x6"
  ArcFitTolerance = 1e-06
  AttachmentSupport = -> [XY_Plane]
  FullyConstrained = true
  MakeInternals = false
  MapMode = 5
  sketch-geometry (2):
    g0: LineSegment [constr] StartX=0 StartY=0 StartZ=0 EndX=-16.5 EndY=0 EndZ=0
    g1: Circle CenterX=-16.5 CenterY=0 CenterZ=0 NormalX=0 NormalY=0 NormalZ=1 AngleXU=0 Radius=2.5
  constraints (5):
    c: Distance(g0) = 16.5
    c: Coincident(g0,g-1)
    c: PointOnObject(g0,g-1)
    c: Diameter(g1) = 5
    c: Coincident(g0,g1)
FEATURE [Sketcher::SketchObject] Sketch027  label="foro sotto posteriore M3x5x6"
  ArcFitTolerance = 1e-06
  AttachmentSupport = -> [XY_Plane]
  ExternalGeometry = -> [Sketch]
  FullyConstrained = true
  MakeInternals = false
  MapMode = 5
  sketch-geometry (2):
    g0: LineSegment [constr] StartX=-82.8 StartY=2e-16 StartZ=0 EndX=-71.3 EndY=2e-16 EndZ=0
    g1: Circle CenterX=-71.3 CenterY=2e-16 CenterZ=0 NormalX=0 NormalY=0 NormalZ=1 AngleXU=0 Radius=2.5
  constraints (5):
    c: Distance(g0) = 11.5
    c: Coincident(g0,g-3)
    c: PointOnObject(g0,g-3)
    c: Diameter(g1) = 5
    c: Coincident(g1,g0)
FEATURE [Sketcher::SketchObject] Sketch029  label="fori sotto impugnatura"
  ArcFitTolerance = 1e-06
  AttachmentSupport = -> [XY_Plane]
  ExternalGeometry = -> [Sketch]
  FullyConstrained = true
  MakeInternals = false
  MapMode = 5
  sketch-geometry (15):
    g0: LineSegment [constr] StartX=-175.232 StartY=-1.83e-14 StartZ=0 EndX=-191.232 EndY=0 EndZ=0
    g1: Circle CenterX=-191.232 CenterY=0 CenterZ=0 NormalX=0 NormalY=0 NormalZ=1 AngleXU=0 Radius=3.95
    g2: LineSegment [constr] StartX=-175.232 StartY=-1.83e-14 StartZ=0 EndX=-204.275 EndY=0 EndZ=0
    g3: LineSegment StartX=-204.275 StartY=3.525 StartZ=0 EndX=-204.275 EndY=-3.525 EndZ=0
    g4: LineSegment StartX=-205.4 StartY=-4.65 StartZ=0 EndX=-206.65 EndY=-4.65 EndZ=0
    g5: LineSegment StartX=-207.775 StartY=-3.525 StartZ=0 EndX=-207.775 EndY=3.525 EndZ=0
    g6: LineSegment StartX=-206.65 StartY=4.65 StartZ=0 EndX=-205.4 EndY=4.65 EndZ=0
    g7: ArcOfCircle CenterX=-206.65 CenterY=3.525 CenterZ=0 NormalX=0 NormalY=0 NormalZ=1 AngleXU=0 Radius=1.125 StartAngle=1.5708 EndAngle=3.14159
    g8: GeomPoint [constr] X=-207.775 Y=4.65 Z=0
    g9: ArcOfCircle CenterX=-205.4 CenterY=3.525 CenterZ=0 NormalX=0 NormalY=0 NormalZ=1 AngleXU=0 Radius=1.125 StartAngle=0 EndAngle=1.5708
    g10: GeomPoint [constr] X=-204.275 Y=4.65 Z=0
    g11: ArcOfCircle CenterX=-205.4 CenterY=-3.525 CenterZ=0 NormalX=0 NormalY=0 NormalZ=1 AngleXU=0 Radius=1.125 StartAngle=4.71239 EndAngle=6.28319
    g12: GeomPoint [constr] X=-204.275 Y=-4.65 Z=0
    g13: ArcOfCircle CenterX=-206.65 CenterY=-3.525 CenterZ=0 NormalX=0 NormalY=0 NormalZ=1 AngleXU=0 Radius=1.125 StartAngle=3.14159 EndAngle=4.71239
    g14: GeomPoint [constr] X=-207.775 Y=-4.65 Z=0
  constraints (35):
    c: Distance(g0) = 16
    c: Coincident(g0,g-3)
    c: PointOnObject(g0,g-1)
    c: Diameter(g1) = 7.9
    c: Coincident(g1,g0)
    c: Coincident(g2,g0)
    c: PointOnObject(g2,g-1)
    c: Vertical(g3)
    c: Horizontal(g4)
    c: Vertical(g5)
    c: Horizontal(g6)
    c: DistanceY(g12,g10) = 9.3
    c: DistanceX(g8,g10) = 3.5
    c: Symmetric(g10,g12,g2)
    c: PointOnObject(g8,g5)
    c: PointOnObject(g8,g6)
    c: Tangent(g5,g7) = 1.5708
    c: Tangent(g6,g7) = 1.5708
    c: PointOnObject(g10,g3)
    c: PointOnObject(g10,g6)
    c: Tangent(g3,g9) = 1.5708
    c: Tangent(g6,g9) = 1.5708
    c: PointOnObject(g12,g3)
    c: PointOnObject(g12,g4)
    c: Tangent(g3,g11) = 1.5708
    c: Tangent(g4,g11) = 1.5708
    c: PointOnObject(g14,g4)
    c: PointOnObject(g14,g5)
    c: Tangent(g4,g13) = 1.5708
    c: Tangent(g5,g13) = 1.5708
    c: Equal(g7,g9)
    c: Equal(g9,g11)
    c: Equal(g11,g13)
    c: DistanceX(g6,g6) = 1.25
    c: DistanceX(g-5,g5) = 6.8
FEATURE [Sketcher::SketchObject] Sketch030  label="fori superiori per solenoide e oled"
  ArcFitTolerance = 1e-06
  AttachmentSupport = -> [XY_Plane]
  ExternalGeometry = -> [Sketch]
  FullyConstrained = true
  MakeInternals = false
  MapMode = 5
  sketch-geometry (33):
    g0: LineSegment [constr] StartX=-181.6 StartY=1.12e-14 StartZ=0 EndX=-169.91 EndY=0 EndZ=0
    g1: LineSegment [constr] StartX=-169.91 StartY=0 StartZ=0 EndX=-169.91 EndY=-2.6 EndZ=0
    g2: LineSegment [constr] StartX=-169.91 StartY=0 StartZ=0 EndX=-169.91 EndY=2.6 EndZ=0
    g3: LineSegment StartX=-169.91 StartY=4.975 StartZ=0 EndX=-169.91 EndY=8.225 EndZ=0
    g4: LineSegment StartX=-167.535 StartY=10.6 StartZ=0 EndX=-167.285 EndY=10.6 EndZ=0
    g5: LineSegment StartX=-164.91 StartY=8.225 StartZ=0 EndX=-164.91 EndY=4.975 EndZ=0
    g6: LineSegment StartX=-167.285 StartY=2.6 StartZ=0 EndX=-167.535 EndY=2.6 EndZ=0
    g7: LineSegment StartX=-169.91 StartY=-4.975 StartZ=0 EndX=-169.91 EndY=-8.225 EndZ=0
    g8: LineSegment StartX=-167.535 StartY=-10.6 StartZ=0 EndX=-167.285 EndY=-10.6 EndZ=0
    g9: LineSegment StartX=-164.91 StartY=-8.225 StartZ=0 EndX=-164.91 EndY=-4.975 EndZ=0
    g10: LineSegment StartX=-167.285 StartY=-2.6 StartZ=0 EndX=-167.535 EndY=-2.6 EndZ=0
    g11: ArcOfCircle CenterX=-167.535 CenterY=8.225 CenterZ=0 NormalX=0 NormalY=0 NormalZ=1 AngleXU=0 Radius=2.375 StartAngle=1.5708 EndAngle=3.14159
    g12: GeomPoint [constr] X=-169.91 Y=10.6 Z=0
    g13: ArcOfCircle CenterX=-167.285 CenterY=8.225 CenterZ=0 NormalX=0 NormalY=0 NormalZ=1 AngleXU=0 Radius=2.375 StartAngle=0 EndAngle=1.5708
    g14: GeomPoint [constr] X=-164.91 Y=10.6 Z=0
    g15: ArcOfCircle CenterX=-167.285 CenterY=4.975 CenterZ=0 NormalX=0 NormalY=0 NormalZ=1 AngleXU=0 Radius=2.375 StartAngle=4.71239 EndAngle=6.28319
    g16: GeomPoint [constr] X=-164.91 Y=2.6 Z=0
    g17: ArcOfCircle CenterX=-167.535 CenterY=4.975 CenterZ=0 NormalX=0 NormalY=0 NormalZ=1 AngleXU=0 Radius=2.375 StartAngle=3.14159 EndAngle=4.71239
    g18: GeomPoint [constr] X=-169.91 Y=2.6 Z=0
    g19: ArcOfCircle CenterX=-167.535 CenterY=-4.975 CenterZ=0 NormalX=0 NormalY=0 NormalZ=1 AngleXU=0 Radius=2.375 StartAngle=1.5708 EndAngle=3.14159
    g20: GeomPoint [constr] X=-169.91 Y=-2.6 Z=0
    g21: ArcOfCircle CenterX=-167.285 CenterY=-4.975 CenterZ=0 NormalX=0 NormalY=0 NormalZ=1 AngleXU=0 Radius=2.375 StartAngle=0 EndAngle=1.5708
    g22: GeomPoint [constr] X=-164.91 Y=-2.6 Z=0
    g23: ArcOfCircle CenterX=-167.285 CenterY=-8.225 CenterZ=0 NormalX=0 NormalY=0 NormalZ=1 AngleXU=0 Radius=2.375 StartAngle=4.71239 EndAngle=6.28319
    g24: GeomPoint [constr] X=-164.91 Y=-10.6 Z=0
    g25: ArcOfCircle CenterX=-167.535 CenterY=-8.225 CenterZ=0 NormalX=0 NormalY=0 NormalZ=1 AngleXU=0 Radius=2.375 StartAngle=3.14159 EndAngle=4.71239
    g26: GeomPoint [constr] X=-169.91 Y=-10.6 Z=0
    g27: LineSegment [constr] StartX=-181.6 StartY=1.12e-14 StartZ=0 EndX=-152.209 EndY=0 EndZ=0
    g28: LineSegment [constr] StartX=-181.6 StartY=1.12e-14 StartZ=0 EndX=-130.41 EndY=0 EndZ=0
    g29: LineSegment [constr] StartX=-152.209 StartY=0 StartZ=0 EndX=-152.209 EndY=6.95 EndZ=0
    g30: LineSegment [constr] StartX=-130.41 StartY=0 StartZ=0 EndX=-130.41 EndY=-6.95 EndZ=0
    g31: Circle CenterX=-152.209 CenterY=6.95 CenterZ=0 NormalX=0 NormalY=0 NormalZ=1 AngleXU=0 Radius=2.1
    g32: Circle CenterX=-130.41 CenterY=-6.95 CenterZ=0 NormalX=0 NormalY=0 NormalZ=1 AngleXU=0 Radius=2.1
  constraints (79):
    c: Distance(g0) = 11.69
    c: PointOnObject(g0,g-1)
    c: Coincident(g-4,g0)
    c: Distance(g1) = 2.6
    c: Coincident(g1,g0)
    c: Vertical(g1)
    c: Distance(g2) = 2.6
    c: Coincident(g2,g0)
    c: Vertical(g2)
    c: Distance(g18,g12) = 8
    c: Coincident(g18,g2)
    c: Vertical(g3)
    c: Distance(g14,g12) = 5
    c: Horizontal(g4)
    c: Distance(g16,g14) = 8
    c: Vertical(g5)
    c: Distance(g26,g20) = 8
    c: Coincident(g20,g1)
    c: Vertical(g7)
    c: Distance(g26,g24) = 5
    c: Horizontal(g8)
    c: Distance(g24,g22) = 8
    c: Vertical(g9)
    c: PointOnObject(g12,g3)
    c: PointOnObject(g12,g4)
    c: Tangent(g3,g11) = 1.5708
    c: Tangent(g4,g11) = 1.5708
    c: PointOnObject(g14,g5)
    c: PointOnObject(g14,g4)
    c: Tangent(g5,g13) = 1.5708
    c: Tangent(g4,g13) = 1.5708
    c: PointOnObject(g16,g5)
    c: PointOnObject(g16,g6)
    c: Tangent(g5,g15) = 1.5708
    c: Tangent(g6,g15) = 1.5708
    c: PointOnObject(g18,g3)
    c: PointOnObject(g18,g6)
    c: Tangent(g3,g17) = 1.5708
    c: Tangent(g6,g17) = 1.5708
    c: Equal(g11,g13)
    c: Equal(g13,g15)
    c: Equal(g15,g17)
    c: DistanceX(g4,g4) = 0.25
    c: PointOnObject(g20,g7)
    c: PointOnObject(g20,g10)
    c: Tangent(g7,g19) = -1.5708
    c: Tangent(g10,g19) = -1.5708
    c: PointOnObject(g22,g9)
    c: PointOnObject(g22,g10)
    c: Tangent(g9,g21) = -1.5708
    c: Tangent(g10,g21) = -1.5708
    c: PointOnObject(g24,g9)
    c: PointOnObject(g24,g8)
    c: Tangent(g9,g23) = -1.5708
    c: Tangent(g8,g23) = -1.5708
    c: PointOnObject(g26,g8)
    c: PointOnObject(g26,g7)
    c: Tangent(g8,g25) = -1.5708
    c: Tangent(g7,g25) = -1.5708
    c: Equal(g19,g21)
    c: Equal(g21,g23)
    c: Equal(g23,g25)
    c: DistanceX(g10,g10) = 0.25
    c: Distance(g27) = 29.391
    c: Coincident(g27,g0)
    c: PointOnObject(g27,g-1)
    c: Distance(g28) = 51.19
    c: Coincident(g28,g0)
    c: PointOnObject(g28,g-1)
    c: Distance(g29) = 6.95
    c: Coincident(g29,g27)
    c: Vertical(g29)
    c: Distance(g30) = 6.95
    c: Coincident(g30,g28)
    c: Vertical(g30)
    c: Diameter(g31) = 4.2
    c: Diameter(g32) = 4.2
    c: Coincident(g32,g30)
    c: Coincident(g31,g29)
FEATURE [Sketcher::SketchObject] Sketch031  label="fori inferiori switch pompa"
  ArcFitTolerance = 1e-06
  AttachmentSupport = -> [XY_Plane]
  ExternalGeometry = -> [Sketch]
  FullyConstrained = true
  MakeInternals = false
  MapMode = 5
  sketch-geometry (4):
    g0: LineSegment [constr] StartX=-57.2 StartY=1.9e-15 StartZ=0 EndX=-62.45 EndY=1.9e-15 EndZ=0
    g1: LineSegment [constr] StartX=-62.45 StartY=3.25 StartZ=0 EndX=-62.45 EndY=-3.25 EndZ=0
    g2: Circle CenterX=-62.45 CenterY=3.25 CenterZ=0 NormalX=0 NormalY=0 NormalZ=1 AngleXU=0 Radius=1.6
    g3: Circle CenterX=-62.45 CenterY=-3.25 CenterZ=0 NormalX=0 NormalY=0 NormalZ=1 AngleXU=0 Radius=1.6
  constraints (10):
    c: Distance(g0) = 5.25
    c: Coincident(g0,g-3)
    c: PointOnObject(g0,g-3)
    c: Vertical(g1)
    c: DistanceY(g1,g1) = 6.5
    c: Symmetric(g1,g1,g0)
    c: Diameter(g2) = 3.2
    c: Diameter(g3) = 3.2
    c: Coincident(g2,g1)
    c: Coincident(g3,g1)
FEATURE [Sketcher::SketchObject] Sketch032  label="spazio per PILA 18650"
  ArcFitTolerance = 1e-06
  AttachmentSupport = -> [XY_Plane]
  ExternalGeometry = -> [Sketch]
  FullyConstrained = true
  MakeInternals = false
  MapMode = 5
  sketch-geometry (2):
    g0: LineSegment [constr] StartX=-178.142 StartY=-1.74e-14 StartZ=0 EndX=-190.142 EndY=-1.83e-14 EndZ=0
    g1: Circle CenterX=-190.142 CenterY=-1.83e-14 CenterZ=0 NormalX=0 NormalY=0 NormalZ=1 AngleXU=0 Radius=9.25
  constraints (5):
    c: Distance(g0) = 12
    c: Coincident(g0,g-3)
    c: PointOnObject(g0,g-4)
    c: Diameter(g1) = 18.5
    c: Coincident(g1,g0)
FEATURE [Part::Extrusion] Extrude030  label="Extrude spazio per PILA 18650"
  Base = -> Sketch032
  Dir = (0,0,1)
  DirLink = -> Sketch [Edge45]
  DirMode = 2
  FaceMakerClass = Part::FaceMakerBullseye
  FaceMakerMode = 3
  LengthFwd = 68
  LengthRev = 0
  Placement = pos=(6,0,-72.7) rot=(0,0,1;0rad)
  Solid = true
  Symmetric = false
FEATURE [Sketcher::SketchObject] Sketch033  label="fermo per scheda micro"
  ArcFitTolerance = 1e-06
  AttachmentSupport = -> [XZ_Plane]
  ExternalGeometry = -> [Sketch]
  FullyConstrained = true
  MakeInternals = false
  MapMode = 5
  Placement = pos=(0,0,0) rot=(1,0,0;1.5708rad)
  sketch-geometry (12):
    g0: LineSegment StartX=-11.6 StartY=6 StartZ=0 EndX=-4 EndY=6 EndZ=0
    g1: LineSegment StartX=-4 StartY=6 StartZ=0 EndX=-4 EndY=36.4 EndZ=0
    g2: LineSegment StartX=-4 StartY=36.4 StartZ=0 EndX=-11.6 EndY=36.4 EndZ=0
    g3: LineSegment StartX=-11.6 StartY=36.4 StartZ=0 EndX=-11.6 EndY=6 EndZ=0
    g4: LineSegment StartX=-80.11 StartY=11.6 StartZ=0 EndX=-70.51 EndY=11.6 EndZ=0
    g5: LineSegment StartX=-70.51 StartY=11.6 StartZ=0 EndX=-70.51 EndY=6 EndZ=0
    g6: LineSegment StartX=-70.51 StartY=6 StartZ=0 EndX=-80.11 EndY=6 EndZ=0
    g7: LineSegment StartX=-80.11 StartY=6 StartZ=0 EndX=-80.11 EndY=11.6 EndZ=0
    g8: LineSegment StartX=-78.51 StartY=36.4 StartZ=0 EndX=-70.51 EndY=36.4 EndZ=0
    g9: LineSegment StartX=-70.51 StartY=36.4 StartZ=0 EndX=-70.51 EndY=30.8 EndZ=0
    g10: LineSegment StartX=-70.51 StartY=30.8 StartZ=0 EndX=-78.51 EndY=30.8 EndZ=0
    g11: LineSegment StartX=-78.51 StartY=30.8 StartZ=0 EndX=-78.51 EndY=36.4 EndZ=0
  constraints (33):
    c: Horizontal(g0)
    c: Coincident(g1,g0)
    c: Coincident(g2,g1)
    c: Horizontal(g2)
    c: Coincident(g3,g2)
    c: Coincident(g3,g0)
    c: Vertical(g3)
    c: DistanceX(g2,g2) = 7.6
    c: Coincident(g1,g-3)
    c: Coincident(g0,g-3)
    c: Horizontal(g4)
    c: Coincident(g5,g4)
    c: Vertical(g5)
    c: Coincident(g6,g5)
    c: Horizontal(g6)
    c: Coincident(g7,g6)
    c: Coincident(g7,g4)
    c: Vertical(g7)
    c: DistanceY(g5,g5) = 5.6
    c: DistanceX(g4,g4) = 9.6
    c: Coincident(g9,g8)
    c: Vertical(g9)
    c: Coincident(g10,g9)
    c: Horizontal(g10)
    c: Coincident(g11,g10)
    c: Coincident(g11,g8)
    c: Vertical(g11)
    c: DistanceY(g9,g9) = 5.6
    c: DistanceX(g10,g10) = 8
    c: Coincident(g4,g-4)
    c: DistanceX(g4,g10) = 1.6
    c: Horizontal(g8)
    c: DistanceY(g8,g1) = 0
FEATURE [Sketcher::SketchObject] Sketch034  label="buchi guida rail"
  ArcFitTolerance = 1e-06
  AttachmentSupport = -> [XY_Plane]
  ExternalGeometry = -> [Sketch]
  FullyConstrained = true
  MakeInternals = false
  MapMode = 5
  sketch-geometry (6):
    g0: LineSegment [constr] StartX=-100.8 StartY=9.1e-15 StartZ=0 EndX=-93.3 EndY=0 EndZ=0
    g1: LineSegment [constr] StartX=-93.3 StartY=0 StartZ=0 EndX=-73.3 EndY=0 EndZ=0
    g2: LineSegment [constr] StartX=-73.3 StartY=0 StartZ=0 EndX=-53.3 EndY=0 EndZ=0
    g3: Circle CenterX=-93.3 CenterY=0 CenterZ=0 NormalX=0 NormalY=0 NormalZ=1 AngleXU=0 Radius=2.5
    g4: Circle CenterX=-73.3 CenterY=0 CenterZ=0 NormalX=0 NormalY=0 NormalZ=1 AngleXU=0 Radius=2.5
    g5: Circle CenterX=-53.3 CenterY=0 CenterZ=0 NormalX=0 NormalY=0 NormalZ=1 AngleXU=0 Radius=2.5
  constraints (15):
    c: Distance(g0) = 7.5
    c: Coincident(g0,g-3)
    c: PointOnObject(g0,g-1)
    c: Distance(g1) = 20
    c: Coincident(g1,g0)
    c: PointOnObject(g1,g-1)
    c: Distance(g2) = 20
    c: Coincident(g2,g1)
    c: PointOnObject(g2,g-1)
    c: Diameter(g3) = 5
    c: Diameter(g4) = 5
    c: Diameter(g5) = 5
    c: Coincident(g3,g0)
    c: Coincident(g4,g1)
    c: Coincident(g5,g2)
FEATURE [Part::Extrusion] Extrude032  label="Extrude buchi guida rail"
  Base = -> Sketch034
  Dir = (0,0,1)
  DirMode = 2
  FaceMakerClass = Part::FaceMakerBullseye
  FaceMakerMode = 3
  LengthFwd = -6.2
  LengthRev = 0
  Placement = pos=(0,0,43.2) rot=(0,0,1;0rad)
  Solid = true
  Symmetric = false
FEATURE [Part::Extrusion] Extrude033  label="Extrude fori superiori per solenoide e oled001"
  Base = -> Sketch030
  Dir = (0,0,1)
  DirMode = 2
  FaceMakerClass = Part::FaceMakerBullseye
  FaceMakerMode = 3
  LengthFwd = -4.8
  LengthRev = 0
  Placement = pos=(0,0,41.2) rot=(0,0,1;0rad)
  Solid = true
  Symmetric = false
FEATURE [Part::Extrusion] Extrude034  label="Extrude fori sotto impugnatura001"
  Base = -> Sketch029
  Dir = (0,0,1)
  DirMode = 2
  FaceMakerClass = Part::FaceMakerBullseye
  FaceMakerMode = 3
  LengthFwd = 5
  LengthRev = 0
  Placement = pos=(0,0,-83) rot=(0,0,1;0rad)
  Solid = true
  Symmetric = false
FEATURE [Part::Extrusion] Extrude035  label="Extrude fori inferiori switch pompa001"
  Base = -> Sketch031
  Dir = (0,0,1)
  DirMode = 2
  FaceMakerClass = Part::FaceMakerBullseye
  FaceMakerMode = 3
  LengthFwd = 4
  LengthRev = 0
  Placement = pos=(0,0,-1.7) rot=(0,0,1;0rad)
  Solid = true
  Symmetric = false
FEATURE [Part::Extrusion] Extrude036  label="Extrude foro sotto posteriore M3x5x007"
  Base = -> Sketch027
  Dir = (0,0,1)
  DirMode = 2
  FaceMakerClass = Part::FaceMakerBullseye
  FaceMakerMode = 3
  LengthFwd = 6.2
  LengthRev = 0
  Placement = pos=(0,0,-9.6) rot=(0,0,1;0rad)
  Solid = true
  Symmetric = false
FEATURE [Part::Extrusion] Extrude037  label="Extrude foro sotto anteriore M3x5x007"
  Base = -> Sketch026
  Dir = (0,0,1)
  DirMode = 2
  FaceMakerClass = Part::FaceMakerBullseye
  FaceMakerMode = 3
  LengthFwd = 6.2
  LengthRev = 0
  Solid = true
  Symmetric = false
FEATURE [Sketcher::SketchObject] Sketch035  label="foro per fissaggio micro"
  ArcFitTolerance = 1e-06
  AttachmentSupport = -> [XZ_Plane]
  ExternalGeometry = -> [Sketch,Sketch033]
  FullyConstrained = true
  MakeInternals = false
  MapMode = 5
  Placement = pos=(0,0,0) rot=(1,0,0;1.5708rad)
  sketch-geometry (3):
    g0: Circle CenterX=-7.8 CenterY=21.2 CenterZ=0 NormalX=0 NormalY=0 NormalZ=1 AngleXU=0 Radius=1.6
    g1: GeomPoint [constr] X=-4 Y=21.2 Z=0
    g2: LineSegment [constr] StartX=-4 StartY=21.2 StartZ=0 EndX=-11.6 EndY=21.2 EndZ=0
  constraints (6):
    c: Diameter(g0) = 3.2
    c: Symmetric(g-3,g-3,g1)
    c: Coincident(g2,g1)
    c: Horizontal(g2)
    c: DistanceX(g-4,g2) = 0
    c: Symmetric(g2,g1,g0)
FEATURE [Part::Extrusion] Extrude038  label="Extrude foro per fissaggio micro"
  Base = -> Sketch035
  Dir = (0,-1,2e-16)
  DirMode = 2
  FaceMakerClass = Part::FaceMakerBullseye
  FaceMakerMode = 3
  LengthFwd = 3
  LengthRev = 0
  Placement = pos=(0,8.6,0) rot=(0,0,1;0rad)
  Solid = true
  Symmetric = false
FEATURE [Sketcher::SketchObject] Sketch036  label="supporto per alimentatore"
  ArcFitTolerance = 1e-06
  AttachmentSupport = -> [XZ_Plane]
  ExternalGeometry = -> [Sketch,Sketch016,Sketch022]
  FullyConstrained = true
  MakeInternals = false
  MapMode = 5
  Placement = pos=(0,0,0) rot=(1,0,0;1.5708rad)
  sketch-geometry (5):
    g0: LineSegment StartX=-211.843 StartY=-50.0944 StartZ=0 EndX=-211.843 EndY=-80.4316 EndZ=0
    g1: LineSegment StartX=-211.843 StartY=-50.0944 StartZ=0 EndX=-207.775 EndY=-41.3701 EndZ=0
    g2: LineSegment [constr] StartX=-209.443 StartY=-50.0944 StartZ=0 EndX=-209.443 EndY=-80.4316 EndZ=0
    g3: LineSegment StartX=-207.775 StartY=-41.3701 StartZ=0 EndX=-207.775 EndY=-80.4316 EndZ=0
    g4: LineSegment StartX=-211.843 StartY=-80.4316 StartZ=0 EndX=-207.775 EndY=-80.4316 EndZ=0
  constraints (15):
    c: Vertical(g0)
    c: Coincident(g1,g0)
    c: Vertical(g2)
    c: Tangent(g2,g-5)
    c: Coincident(g3,g1)
    c: Vertical(g3)
    c: DistanceY(g-3,g3) = -2
    c: Tangent(g1,g-8)
    c: DistanceY(g-3,g0) = -2
    c: Coincident(g4,g0)
    c: Coincident(g4,g3)
    c: Tangent(g0,g-6)
    c: DistanceY(g-3,g2) = -2
    c: DistanceY(g2,g0) = 0
    c: DistanceX(g-3,g3) = 6.8
FEATURE [Part::Extrusion] Extrude039  label="Extrude039 supporto alimentatore"
  Base = -> Sketch036
  Dir = (0,-1,2e-16)
  DirMode = 2
  FaceMakerClass = Part::FaceMakerBullseye
  FaceMakerMode = 3
  LengthFwd = 25.2
  LengthRev = 0
  Solid = true
  Symmetric = true
FEATURE [Sketcher::SketchObject] Sketch037  label="scavo per alimentatore"
  ArcFitTolerance = 1e-06
  AttachmentSupport = -> [XZ_Plane]
  ExternalGeometry = -> [Sketch036]
  FullyConstrained = true
  MakeInternals = false
  MapMode = 5
  Placement = pos=(0,0,0) rot=(1,0,0;1.5708rad)
  sketch-geometry (4):
    g0: LineSegment StartX=-209.575 StartY=-50.4316 StartZ=0 EndX=-209.575 EndY=-80.4316 EndZ=0
    g1: LineSegment StartX=-209.575 StartY=-50.4316 StartZ=0 EndX=-207.775 EndY=-50.4316 EndZ=0
    g2: LineSegment StartX=-207.775 StartY=-50.4316 StartZ=0 EndX=-207.775 EndY=-80.4316 EndZ=0
    g3: LineSegment StartX=-207.775 StartY=-80.4316 StartZ=0 EndX=-209.575 EndY=-80.4316 EndZ=0
  constraints (11):
    c: Vertical(g0)
    c: Coincident(g1,g0)
    c: Horizontal(g1)
    c: Coincident(g2,g1)
    c: Vertical(g2)
    c: Coincident(g3,g2)
    c: Coincident(g3,g0)
    c: Horizontal(g3)
    c: DistanceX(g1,g1) = 1.8
    c: Coincident(g2,g-3)
    c: DistanceY(g2,g2) = 30
FEATURE [Part::Extrusion] Extrude040  label="Extrude040 scavo alimentatore"
  Base = -> Sketch037
  Dir = (0,-1,2e-16)
  DirMode = 2
  FaceMakerClass = Part::FaceMakerBullseye
  FaceMakerMode = 3
  LengthFwd = 19.5
  LengthRev = 0
  Solid = true
  Symmetric = true
FEATURE [Part::Extrusion] Extrude031  label="Extrude fermo per scheda micro"
  Base = -> Sketch033
  Dir = (0,-1,2e-16)
  DirMode = 2
  FaceMakerClass = Part::FaceMakerBullseye
  FaceMakerMode = 3
  LengthFwd = 3
  LengthRev = 0
  Placement = pos=(0,8.6,0) rot=(0,0,1;0rad)
  Solid = true
  Symmetric = false
FEATURE [Sketcher::SketchObject] Sketch038  label="scavo driver solenoide"
  ArcFitTolerance = 1e-06
  AttachmentSupport = -> [XZ_Plane]
  ExternalGeometry = -> [Sketch,Sketch036]
  FullyConstrained = true
  MakeInternals = false
  MapMode = 5
  Placement = pos=(0,0,0) rot=(1,0,0;1.5708rad)
  sketch-geometry (7):
    g0: LineSegment StartX=-193.66 StartY=-11.0994 StartZ=0 EndX=-195.11 EndY=-10.4232 EndZ=0
    g1: LineSegment StartX=-195.11 StartY=-10.4232 StartZ=0 EndX=-209.225 EndY=-40.6939 EndZ=0
    g2: LineSegment StartX=-193.66 StartY=-11.0994 StartZ=0 EndX=-190.216 EndY=-12.7054 EndZ=0
    g3: LineSegment StartX=-190.216 StartY=-12.7054 StartZ=0 EndX=-204.331 EndY=-42.9761 EndZ=0
    g4: LineSegment StartX=-204.331 StartY=-42.9761 StartZ=0 EndX=-207.775 EndY=-41.3701 EndZ=0
    g5: LineSegment [constr] StartX=-209.225 StartY=-40.6939 StartZ=0 EndX=-207.775 EndY=-41.3701 EndZ=0
    g6: LineSegment StartX=-209.225 StartY=-40.6939 StartZ=0 EndX=-207.775 EndY=-41.3701 EndZ=0
  constraints (19):
    c: Coincident(g1,g0)
    c: Coincident(g3,g2)
    c: Coincident(g4,g3)
    c: Distance(g2) = 3.8
    c: Distance(g1) = 33.4
    c: Coincident(g5,g1)
    c: Distance(g5) = 1.6
    c: Coincident(g-4,g5)
    c: Perpendicular(g5,g-3)
    c: Parallel(g1,g-3)
    c: Perpendicular(g1,g0)
    c: Distance(g0) = 1.6
    c: Coincident(g6,g1)
    c: Coincident(g6,g5)
    c: Parallel(g3,g-3)
    c: Perpendicular(g3,g4)
    c: Perpendicular(g2,g3)
    c: Coincident(g2,g0)
    c: Coincident(g4,g5)
FEATURE [Part::Extrusion] Extrude041  label="Extrude scavo driver solenoide"
  Base = -> Sketch038
  Dir = (0,-1,2e-16)
  DirMode = 2
  FaceMakerClass = Part::FaceMakerBullseye
  FaceMakerMode = 3
  LengthFwd = 17
  LengthRev = 0
  Solid = true
  Symmetric = true
FEATURE [Sketcher::SketchObject] Sketch039  label="scavo per cavo usb per micro"
  ArcFitTolerance = 1e-06
  AttachmentSupport = -> [XZ_Plane]
  ExternalGeometry = -> [Sketch,Sketch016]
  FullyConstrained = true
  MakeInternals = false
  MapMode = 5
  Placement = pos=(0,0,0) rot=(1,0,0;1.5708rad)
  sketch-geometry (4):
    g0: LineSegment StartX=-82.51 StartY=36.4 StartZ=0 EndX=-74.51 EndY=36.4 EndZ=0
    g1: LineSegment StartX=-74.51 StartY=36.4 StartZ=0 EndX=-74.51 EndY=30.8 EndZ=0
    g2: LineSegment StartX=-74.51 StartY=30.8 StartZ=0 EndX=-82.51 EndY=30.8 EndZ=0
    g3: LineSegment StartX=-82.51 StartY=30.8 StartZ=0 EndX=-82.51 EndY=36.4 EndZ=0
  constraints (11):
    c: Coincident(g1,g0)
    c: Vertical(g1)
    c: Coincident(g2,g1)
    c: Horizontal(g2)
    c: Coincident(g3,g2)
    c: Coincident(g3,g0)
    c: Vertical(g3)
    c: Tangent(g0,g-3)
    c: Tangent(g2,g-4)
    c: Tangent(g3,g-4)
    c: Tangent(g1,g-4)
FEATURE [Part::Extrusion] Extrude042  label="Extrude scavo per cavo usb per micro"
  Base = -> Sketch039
  Dir = (0,-1,2e-16)
  DirMode = 2
  FaceMakerClass = Part::FaceMakerBullseye
  FaceMakerMode = 3
  LengthFwd = 11.2
  LengthRev = 0
  Solid = true
  Symmetric = true
FEATURE [Sketcher::SketchObject] Sketch040  label="scavo saldature alimentatore connettore 5v"
  ArcFitTolerance = 1e-06
  AttachmentSupport = -> [XZ_Plane]
  ExternalGeometry = -> [Sketch037]
  FullyConstrained = true
  MakeInternals = false
  MapMode = 5
  Placement = pos=(0,0,0) rot=(1,0,0;1.5708rad)
  sketch-geometry (4):
    g0: LineSegment StartX=-211.175 StartY=-52.4316 StartZ=0 EndX=-211.175 EndY=-56.4316 EndZ=0
    g1: LineSegment StartX=-211.175 StartY=-52.4316 StartZ=0 EndX=-209.575 EndY=-52.4316 EndZ=0
    g2: LineSegment StartX=-209.575 StartY=-52.4316 StartZ=0 EndX=-209.575 EndY=-56.4316 EndZ=0
    g3: LineSegment StartX=-209.575 StartY=-56.4316 StartZ=0 EndX=-211.175 EndY=-56.4316 EndZ=0
  constraints (11):
    c: Vertical(g0)
    c: Coincident(g1,g0)
    c: Horizontal(g1)
    c: Coincident(g2,g1)
    c: Coincident(g3,g2)
    c: Coincident(g3,g0)
    c: Horizontal(g3)
    c: DistanceX(g1,g1) = 1.6
    c: DistanceY(g2,g2) = 4
    c: Tangent(g2,g-3)
    c: DistanceY(g1,g-3) = 2
FEATURE [Part::Extrusion] Extrude043  label="Extrude scavo saldature alimentatore connettore 5v"
  Base = -> Sketch040
  Dir = (0,-1,2e-16)
  DirMode = 2
  FaceMakerClass = Part::FaceMakerBullseye
  FaceMakerMode = 3
  LengthFwd = 8
  LengthRev = 0
  Solid = true
  Symmetric = true
FEATURE [Sketcher::SketchObject] Sketch041  label="scavo saldature alimentatore connettore 5v verticali"
  ArcFitTolerance = 1e-06
  AttachmentSupport = -> [XZ_Plane]
  ExternalGeometry = -> [Sketch037]
  FullyConstrained = true
  MakeInternals = false
  MapMode = 5
  Placement = pos=(0,0,0) rot=(1,0,0;1.5708rad)
  sketch-geometry (4):
    g0: LineSegment StartX=-211.175 StartY=-53.6316 StartZ=0 EndX=-209.575 EndY=-53.6316 EndZ=0
    g1: LineSegment StartX=-209.575 StartY=-53.6316 StartZ=0 EndX=-209.575 EndY=-76.6316 EndZ=0
    g2: LineSegment StartX=-209.575 StartY=-76.6316 StartZ=0 EndX=-211.175 EndY=-76.6316 EndZ=0
    g3: LineSegment StartX=-211.175 StartY=-76.6316 StartZ=0 EndX=-211.175 EndY=-53.6316 EndZ=0
  constraints (11):
    c: Horizontal(g0)
    c: Coincident(g1,g0)
    c: Coincident(g2,g1)
    c: Horizontal(g2)
    c: Coincident(g3,g2)
    c: Coincident(g3,g0)
    c: Vertical(g3)
    c: DistanceY(g3,g3) = 23
    c: DistanceX(g0,g0) = 1.6
    c: Tangent(g1,g-3)
    c: DistanceY(g0,g-3) = 3.2
FEATURE [Part::Extrusion] Extrude044  label="Extrude scavo saldature alimentatore connettore 5v verticali"
  Base = -> Sketch041
  Dir = (0,-1,2e-16)
  DirMode = 2
  FaceMakerClass = Part::FaceMakerBullseye
  FaceMakerMode = 3
  LengthFwd = 3.2
  LengthRev = 0
  Placement = pos=(0,8.3,0) rot=(0,0,1;0rad)
  Solid = true
  Symmetric = false
FEATURE [Sketcher::SketchObject] Sketch042  label="fermi per driver solenoide e alimentatore"
  ArcFitTolerance = 1e-06
  AttachmentSupport = -> [XZ_Plane]
  ExternalGeometry = -> [Sketch036,Sketch037,Sketch,Sketch038]
  FullyConstrained = true
  MakeInternals = false
  MapMode = 5
  Placement = pos=(0,0,0) rot=(1,0,0;1.5708rad)
  sketch-geometry (27):
    g0: LineSegment StartX=-195.773 StartY=-15.631 StartZ=0 EndX=-196.702 EndY=-17.6249 EndZ=0
    g1: LineSegment StartX=-196.702 StartY=-17.6249 StartZ=0 EndX=-194.709 EndY=-18.5546 EndZ=0
    g2: LineSegment StartX=-194.709 StartY=-18.5546 StartZ=0 EndX=-193.779 EndY=-16.5607 EndZ=0
    g3: LineSegment StartX=-193.779 StartY=-16.5607 StartZ=0 EndX=-195.773 EndY=-15.631 EndZ=0
    g4: LineSegment StartX=-196.547 StartY=-13.5047 StartZ=0 EndX=-198.829 EndY=-18.3988 EndZ=0
    g5: LineSegment StartX=-198.829 StartY=-18.3988 StartZ=0 EndX=-195.385 EndY=-20.0047 EndZ=0
    g6: LineSegment StartX=-193.258 StartY=-19.2308 StartZ=0 EndX=-192.329 EndY=-17.2369 EndZ=0
    g7: LineSegment StartX=-193.103 StartY=-15.1106 StartZ=0 EndX=-196.547 EndY=-13.5047 EndZ=0
    g8: LineSegment [constr] StartX=-193.935 StartY=-20.6809 StartZ=0 EndX=-193.258 EndY=-19.2308 EndZ=0
    g9: LineSegment [constr] StartX=-193.935 StartY=-20.6809 StartZ=0 EndX=-195.385 EndY=-20.0047 EndZ=0
    g10: ArcOfCircle CenterX=-193.779 CenterY=-16.5607 CenterZ=0 NormalX=0 NormalY=0 NormalZ=1 AngleXU=0 Radius=1.6 StartAngle=5.84685 EndAngle=7.41765
    g11: GeomPoint [constr] X=-191.653 Y=-15.7868 Z=0
    g12: ArcOfCircle CenterX=-194.709 CenterY=-18.5546 CenterZ=0 NormalX=0 NormalY=0 NormalZ=1 AngleXU=0 Radius=1.6 StartAngle=4.27606 EndAngle=5.84685
    g13: GeomPoint [constr] X=-193.935 Y=-20.6809 Z=0
    g14: LineSegment StartX=-207.775 StartY=-46.8316 StartZ=0 EndX=-207.775 EndY=-50.8316 EndZ=0
    g15: LineSegment StartX=-207.775 StartY=-46.8316 StartZ=0 EndX=-203.775 EndY=-46.8316 EndZ=0
    g16: LineSegment StartX=-203.775 StartY=-46.8316 StartZ=0 EndX=-203.775 EndY=-50.8316 EndZ=0
    g17: LineSegment StartX=-207.775 StartY=-50.8316 StartZ=0 EndX=-203.775 EndY=-50.8316 EndZ=0
    g18: LineSegment StartX=-209.375 StartY=-52.4316 StartZ=0 EndX=-203.775 EndY=-52.4316 EndZ=0
    g19: LineSegment StartX=-202.175 StartY=-50.8316 StartZ=0 EndX=-202.175 EndY=-46.8316 EndZ=0
    g20: LineSegment StartX=-203.775 StartY=-45.2316 StartZ=0 EndX=-209.375 EndY=-45.2316 EndZ=0
    g21: LineSegment StartX=-209.375 StartY=-45.2316 StartZ=0 EndX=-209.375 EndY=-52.4316 EndZ=0
    g22: ArcOfCircle CenterX=-203.775 CenterY=-46.8316 CenterZ=0 NormalX=0 NormalY=0 NormalZ=1 AngleXU=0 Radius=1.6 StartAngle=1.8e-15 EndAngle=1.5708
    g23: GeomPoint [constr] X=-202.175 Y=-45.2316 Z=0
    g24: ArcOfCircle CenterX=-203.775 CenterY=-50.8316 CenterZ=0 NormalX=0 NormalY=0 NormalZ=1 AngleXU=0 Radius=1.6 StartAngle=4.71239 EndAngle=6.28319
    g25: GeomPoint [constr] X=-202.175 Y=-52.4316 Z=0
    g26: LineSegment [constr] StartX=-207.775 StartY=-50.4316 StartZ=0 EndX=-207.775 EndY=-50.8316 EndZ=0
  constraints (69):
    c: Coincident(g1,g0)
    c: Coincident(g2,g1)
    c: Coincident(g3,g2)
    c: Coincident(g3,g0)
    c: Parallel(g0,g2)
    c: Perpendicular(g3,g0)
    c: Perpendicular(g1,g0)
    c: Coincident(g5,g4)
    c: Coincident(g7,g4)
    c: Distance(g3) = 2.2
    c: Distance(g2) = 2.2
    c: Parallel(g6,g2)
    c: Parallel(g6,g4)
    c: Perpendicular(g5,g6)
    c: Perpendicular(g7,g6)
    c: Distance(g13,g11) = 5.4
    c: Distance(g5,g13) = 5.4
    c: Coincident(g9,g8)
    c: Distance(g8) = 1.6
    c: Distance(g9) = 1.6
    c: Perpendicular(g9,g8)
    c: Parallel(g8,g6)
    c: Coincident(g8,g13)
    c: Distance(g8,g1) = 1.6
    c: Distance(g9,g1) = 1.6
    c: Tangent(g0,g-5)
    c: Distance(g0,g-6) = 26.2
    c: PointOnObject(g11,g7)
    c: PointOnObject(g11,g6)
    c: Tangent(g7,g10) = -1.5708
    c: Tangent(g6,g10) = -1.5708
    c: PointOnObject(g13,g5)
    c: Tangent(g5,g12) = -1.5708
    c: Tangent(g6,g12) = -1.5708
    c: Equal(g10,g12)
    c: Coincident(g10,g2)
    c: Vertical(g14)
    c: Coincident(g15,g14)
    c: Horizontal(g15)
    c: Coincident(g16,g15)
    c: Vertical(g16)
    c: Coincident(g17,g14)
    c: Coincident(g17,g16)
    c: Horizontal(g17)
    c: Distance(g16) = 4
    c: Distance(g15) = 4
    c: Horizontal(g18)
    c: Vertical(g19)
    c: Horizontal(g20)
    c: Coincident(g21,g20)
    c: Coincident(g21,g18)
    c: Vertical(g21)
    c: Distance(g20,g23) = 7.2
    c: Distance(g25,g23) = 7.2
    c: DistanceY(g18,g14) = 1.6
    c: DistanceX(g18,g14) = 1.6
    c: PointOnObject(g23,g20)
    c: PointOnObject(g23,g19)
    c: Tangent(g20,g22) = -1.5708
    c: Tangent(g19,g22) = -1.5708
    c: PointOnObject(g25,g19)
    c: Tangent(g18,g24) = -1.5708
    c: Tangent(g19,g24) = -1.5708
    c: Equal(g22,g24)
    c: Coincident(g22,g15)
    c: Vertical(g26)
    c: Distance(g26) = 0.4
    c: Coincident(g26,g-4)
    c: Coincident(g14,g26)
FEATURE [Part::Extrusion] Extrude045  label="Extrude fermi per driver solenoide e alimentatore"
  Base = -> Sketch042
  Dir = (0,-1,2e-16)
  DirMode = 2
  FaceMakerClass = Part::FaceMakerBullseye
  FaceMakerMode = 3
  LengthFwd = 25.2
  LengthRev = 0
  Solid = true
  Symmetric = true
FEATURE [Sketcher::SketchObject] Sketch043  label="scavo pulizia fermo alimentatore"
  ArcFitTolerance = 1e-06
  AttachmentSupport = -> [XZ_Plane]
  ExternalGeometry = -> [Sketch042,Sketch036,Sketch037]
  FullyConstrained = true
  MakeInternals = false
  MapMode = 5
  Placement = pos=(0,0,0) rot=(1,0,0;1.5708rad)
  sketch-geometry (6):
    g0: LineSegment StartX=-209.375 StartY=-52.4316 StartZ=0 EndX=-209.375 EndY=-50.4316 EndZ=0
    g1: LineSegment StartX=-209.375 StartY=-50.4316 StartZ=0 EndX=-207.775 EndY=-50.4316 EndZ=0
    g2: LineSegment StartX=-207.775 StartY=-50.4316 StartZ=0 EndX=-207.775 EndY=-45.2316 EndZ=0
    g3: LineSegment StartX=-207.775 StartY=-45.2316 StartZ=0 EndX=-202.175 EndY=-45.2316 EndZ=0
    g4: LineSegment StartX=-202.175 StartY=-45.2316 StartZ=0 EndX=-202.175 EndY=-52.4316 EndZ=0
    g5: LineSegment StartX=-202.175 StartY=-52.4316 StartZ=0 EndX=-209.375 EndY=-52.4316 EndZ=0
  constraints (13):
    c: Vertical(g0)
    c: Coincident(g1,g0)
    c: Coincident(g2,g1)
    c: Coincident(g3,g2)
    c: Coincident(g4,g3)
    c: Coincident(g5,g4)
    c: Coincident(g5,g0)
    c: Horizontal(g5)
    c: Coincident(g0,g-6)
    c: Tangent(g1,g-8)
    c: Tangent(g2,g-4)
    c: Tangent(g3,g-7)
    c: Tangent(g4,g-3)
FEATURE [Part::Extrusion] Extrude046  label="Extrude scavo pulizia fermo alimentatore"
  Base = -> Sketch043
  Dir = (0,-1,2e-16)
  DirMode = 2
  FaceMakerClass = Part::FaceMakerBullseye
  FaceMakerMode = 3
  LengthFwd = 19.5
  LengthRev = 0
  Solid = true
  Symmetric = true
FEATURE [Sketcher::SketchObject] Sketch044  label="buchini per fissaggio oled"
  ArcFitTolerance = 1e-06
  AttachmentSupport = -> [YZ_Plane]
  ExternalGeometry = -> [Sketch]
  FullyConstrained = true
  MakeInternals = false
  MapMode = 5
  Placement = pos=(0,0,0) rot=(0.57735,0.57735,0.57735;2.0944rad)
  sketch-geometry (5):
    g0: LineSegment [constr] StartX=1.5e-14 StartY=67.3588 StartZ=0 EndX=0 EndY=64.3588 EndZ=0
    g1: LineSegment [constr] StartX=0 StartY=64.3588 StartZ=0 EndX=10.4 EndY=64.3588 EndZ=0
    g2: LineSegment [constr] StartX=0 StartY=64.3588 StartZ=0 EndX=-10.4 EndY=64.3588 EndZ=0
    g3: Circle CenterX=10.4 CenterY=64.3588 CenterZ=0 NormalX=0 NormalY=0 NormalZ=1 AngleXU=0 Radius=1.5
    g4: Circle CenterX=-10.4 CenterY=64.3588 CenterZ=0 NormalX=0 NormalY=0 NormalZ=1 AngleXU=0 Radius=1.5
  constraints (13):
    c: Distance(g0) = 3
    c: PointOnObject(g0,g-2)
    c: Coincident(g1,g0)
    c: Horizontal(g1)
    c: Coincident(g2,g0)
    c: Horizontal(g2)
    c: DistanceX(g1,g1) = 10.4
    c: Coincident(g3,g1)
    c: Diameter(g4) = 3
    c: Coincident(g4,g2)
    c: Coincident(g0,g-7)
    c: Equal(g1,g2)
    c: Equal(g4,g3)
FEATURE [Part::Extrusion] Extrude047  label="Extrude buchini per fissaggio oled"
  Base = -> Sketch044
  Dir = (1,0,0)
  DirMode = 2
  FaceMakerClass = Part::FaceMakerBullseye
  FaceMakerMode = 3
  LengthFwd = 10
  LengthRev = 0
  Placement = pos=(-186,0,0) rot=(0,0,1;0rad)
  Solid = true
  Symmetric = false
FEATURE [Sketcher::SketchObject] Sketch046  label="scavo 5x5 neopixel"
  ArcFitTolerance = 1e-06
  AttachmentSupport = -> [YZ_Plane002]
  FullyConstrained = true
  MakeInternals = false
  MapMode = 5
  Placement = pos=(0,0,0) rot=(0.57735,0.57735,0.57735;2.0944rad)
  sketch-geometry (4):
    g0: LineSegment StartX=-2.7 StartY=2.7 StartZ=0 EndX=2.7 EndY=2.7 EndZ=0
    g1: LineSegment StartX=2.7 StartY=2.7 StartZ=0 EndX=2.7 EndY=-2.7 EndZ=0
    g2: LineSegment StartX=2.7 StartY=-2.7 StartZ=0 EndX=-2.7 EndY=-2.7 EndZ=0
    g3: LineSegment StartX=-2.7 StartY=-2.7 StartZ=0 EndX=-2.7 EndY=2.7 EndZ=0
  constraints (11):
    c: Horizontal(g0)
    c: Coincident(g1,g0)
    c: Vertical(g1)
    c: Coincident(g2,g1)
    c: Horizontal(g2)
    c: Coincident(g3,g2)
    c: Coincident(g3,g0)
    c: Vertical(g3)
    c: DistanceX(g0,g0) = 5.4
    c: DistanceY(g1,g1) = 5.4
    c: Symmetric(g0,g1,g-1)
FEATURE [Sketcher::SketchObject] Sketch047  label="scavo 10x10 neopixel corpo"
  ArcFitTolerance = 1e-06
  AttachmentOffset = pos=(0,0,1) rot=(0,0,1;0rad)
  AttachmentSupport = -> [YZ_Plane002]
  FullyConstrained = true
  MakeInternals = false
  MapMode = 5
  Placement = pos=(1,0,0) rot=(0.57735,0.57735,0.57735;2.0944rad)
  sketch-geometry (4):
    g0: LineSegment StartX=-5 StartY=5.1 StartZ=0 EndX=5 EndY=5.1 EndZ=0
    g1: LineSegment StartX=5 StartY=5.1 StartZ=0 EndX=5 EndY=-5.1 EndZ=0
    g2: LineSegment StartX=5 StartY=-5.1 StartZ=0 EndX=-5 EndY=-5.1 EndZ=0
    g3: LineSegment StartX=-5 StartY=-5.1 StartZ=0 EndX=-5 EndY=5.1 EndZ=0
  constraints (11):
    c: Horizontal(g0)
    c: Coincident(g1,g0)
    c: Vertical(g1)
    c: Coincident(g2,g1)
    c: Horizontal(g2)
    c: Coincident(g3,g2)
    c: Coincident(g3,g0)
    c: Vertical(g3)
    c: DistanceX(g0,g0) = 10
    c: DistanceY(g1,g1) = 10.2
    c: Symmetric(g0,g2,g-1)
FEATURE [Sketcher::SketchObject] Sketch048  label="buco per perno blocco neopixel"
  ArcFitTolerance = 1e-06
  AttachmentSupport = -> [XZ_Plane002]
  FullyConstrained = true
  MakeInternals = false
  MapMode = 5
  Placement = pos=(0,0,0) rot=(1,0,0;1.5708rad)
  sketch-geometry (4):
    g0: LineSegment StartX=3 StartY=1.2 StartZ=0 EndX=3 EndY=-1.2 EndZ=0
    g1: LineSegment StartX=3 StartY=-1.2 StartZ=0 EndX=5.4 EndY=-1.2 EndZ=0
    g2: LineSegment StartX=5.4 StartY=-1.2 StartZ=0 EndX=5.4 EndY=1.2 EndZ=0
    g3: LineSegment StartX=5.4 StartY=1.2 StartZ=0 EndX=3 EndY=1.2 EndZ=0
  constraints (11):
    c: Coincident(g1,g0)
    c: Horizontal(g1)
    c: Coincident(g2,g1)
    c: Vertical(g2)
    c: Coincident(g3,g2)
    c: Coincident(g3,g0)
    c: Horizontal(g3)
    c: DistanceX(g1,g1) = 2.4
    c: DistanceY(g2,g2) = 2.4
    c: Symmetric(g0,g0,g-1)
    c: DistanceX(g-1,g0) = 3
FEATURE [Sketcher::SketchObject] Sketch045  label="blocco principale per neopixel"
  ArcFitTolerance = 1e-06
  AttachmentSupport = -> [XZ_Plane002]
  ExternalGeometry = -> [Sketch048]
  FullyConstrained = true
  MakeInternals = false
  MapMode = 5
  Placement = pos=(0,0,0) rot=(1,0,0;1.5708rad)
  sketch-geometry (6):
    g0: LineSegment StartX=0 StartY=5.1 StartZ=0 EndX=0 EndY=-5.1 EndZ=0
    g1: LineSegment StartX=0 StartY=-5.1 StartZ=0 EndX=3 EndY=-5.1 EndZ=0
    g2: LineSegment StartX=7 StartY=-1.1 StartZ=0 EndX=7 EndY=5.1 EndZ=0
    g3: LineSegment StartX=7 StartY=5.1 StartZ=0 EndX=0 EndY=5.1 EndZ=0
    g4: ArcOfCircle CenterX=3 CenterY=-1.1 CenterZ=0 NormalX=0 NormalY=0 NormalZ=1 AngleXU=0 Radius=4 StartAngle=4.71239 EndAngle=6.28319
    g5: GeomPoint [constr] X=7 Y=-5.1 Z=0
  constraints (15):
    c: Vertical(g0)
    c: Coincident(g1,g0)
    c: Horizontal(g1)
    c: Vertical(g2)
    c: Coincident(g3,g2)
    c: Coincident(g3,g0)
    c: Horizontal(g3)
    c: DistanceY(g0,g0) = 10.2
    c: Symmetric(g0,g0,g-1)
    c: DistanceX(g3,g3) = 7
    c: PointOnObject(g5,g2)
    c: PointOnObject(g5,g1)
    c: Tangent(g2,g4) = -1.5708
    c: Tangent(g1,g4) = -1.5708
    c: DistanceX(g-3,g1) = 0
FEATURE [Sketcher::SketchObject] Sketch049  label="rinforzi esterni per corpo neopoixel"
  ArcFitTolerance = 1e-06
  AttachmentSupport = -> [XZ_Plane002]
  ExternalGeometry = -> [Sketch045]
  FullyConstrained = true
  MakeInternals = false
  MapMode = 5
  Placement = pos=(0,0,0) rot=(1,0,0;1.5708rad)
  sketch-geometry (8):
    g0: LineSegment StartX=1 StartY=-4.1 StartZ=0 EndX=2 EndY=-4.1 EndZ=0
    g1: LineSegment StartX=2 StartY=-4.1 StartZ=0 EndX=2 EndY=-5.1 EndZ=0
    g2: LineSegment StartX=2 StartY=-5.1 StartZ=0 EndX=1 EndY=-5.1 EndZ=0
    g3: LineSegment StartX=1 StartY=-5.1 StartZ=0 EndX=1 EndY=-4.1 EndZ=0
    g4: LineSegment StartX=1 StartY=5.1 StartZ=0 EndX=2 EndY=5.1 EndZ=0
    g5: LineSegment StartX=2 StartY=5.1 StartZ=0 EndX=2 EndY=4.1 EndZ=0
    g6: LineSegment StartX=2 StartY=4.1 StartZ=0 EndX=1 EndY=4.1 EndZ=0
    g7: LineSegment StartX=1 StartY=4.1 StartZ=0 EndX=1 EndY=5.1 EndZ=0
  constraints (24):
    c: Horizontal(g0)
    c: Coincident(g1,g0)
    c: Vertical(g1)
    c: Coincident(g2,g1)
    c: Horizontal(g2)
    c: Coincident(g3,g2)
    c: Coincident(g3,g0)
    c: Vertical(g3)
    c: Horizontal(g4)
    c: Coincident(g5,g4)
    c: Vertical(g5)
    c: Coincident(g6,g5)
    c: Horizontal(g6)
    c: Coincident(g7,g6)
    c: Coincident(g7,g4)
    c: Vertical(g7)
    c: DistanceX(g4,g4) = 1
    c: DistanceY(g5,g5) = 1
    c: DistanceX(g0,g0) = 1
    c: DistanceY(g1,g1) = 1
    c: DistanceX(g-3,g4) = 1
    c: DistanceY(g-3,g4) = 0
    c: DistanceX(g-4,g2) = 1
    c: DistanceY(g2,g-4) = 0
FEATURE [Sketcher::SketchObject] Sketch052  label="scavo saldature driver solenoide"
  ArcFitTolerance = 1e-06
  AttachmentSupport = -> [XZ_Plane]
  ExternalGeometry = -> [Sketch038]
  FullyConstrained = true
  MakeInternals = false
  MapMode = 5
  Placement = pos=(0,0,0) rot=(1,0,0;1.5708rad)
  sketch-geometry (4):
    g0: LineSegment StartX=-196.56 StartY=-9.74706 StartZ=0 EndX=-198.25 EndY=-13.3723 EndZ=0
    g1: LineSegment StartX=-198.25 StartY=-13.3723 StartZ=0 EndX=-196.8 EndY=-14.0485 EndZ=0
    g2: LineSegment StartX=-196.8 StartY=-14.0485 StartZ=0 EndX=-195.11 EndY=-10.4232 EndZ=0
    g3: LineSegment StartX=-195.11 StartY=-10.4232 StartZ=0 EndX=-196.56 EndY=-9.74706 EndZ=0
  constraints (11):
    c: Coincident(g1,g0)
    c: Coincident(g2,g1)
    c: Coincident(g3,g2)
    c: Coincident(g3,g0)
    c: Parallel(g2,g0)
    c: Perpendicular(g2,g3)
    c: Perpendicular(g1,g2,g1) = 1.5708
    c: Parallel(g2,g-3)
    c: Distance(g2) = 4
    c: Distance(g3) = 1.6
    c: Coincident(g2,g-3)
FEATURE [Part::Extrusion] Extrude055  label="Extrude scavo saldature driver solenoide"
  Base = -> Sketch052
  Dir = (0,-1,2e-16)
  DirMode = 2
  FaceMakerClass = Part::FaceMakerBullseye
  FaceMakerMode = 3
  LengthFwd = 6
  LengthRev = 0
  Solid = true
  Symmetric = true
FEATURE [Sketcher::SketchObject] Sketch053  label="scavo saldature rumble"
  ArcFitTolerance = 1e-06
  AttachmentSupport = -> [XZ_Plane]
  ExternalGeometry = -> [Sketch019]
  FullyConstrained = true
  MakeInternals = false
  MapMode = 5
  Placement = pos=(0,0,0) rot=(1,0,0;1.5708rad)
  sketch-geometry (4):
    g0: LineSegment StartX=-165.31 StartY=-44.1173 StartZ=0 EndX=-166.547 EndY=-47.9216 EndZ=0
    g1: LineSegment StartX=-166.547 StartY=-47.9216 StartZ=0 EndX=-165.405 EndY=-48.2924 EndZ=0
    g2: LineSegment StartX=-165.405 StartY=-48.2924 StartZ=0 EndX=-164.169 EndY=-44.4881 EndZ=0
    g3: LineSegment StartX=-164.169 StartY=-44.4881 StartZ=0 EndX=-165.31 EndY=-44.1173 EndZ=0
  constraints (11):
    c: Coincident(g1,g0)
    c: Coincident(g2,g1)
    c: Coincident(g3,g2)
    c: Coincident(g3,g0)
    c: Parallel(g0,g2)
    c: Perpendicular(g3,g0)
    c: Perpendicular(g1,g0)
    c: Parallel(g0,g-3)
    c: Distance(g0) = 4
    c: Distance(g1) = 1.2
    c: Coincident(g0,g-3)
FEATURE [Part::Extrusion] Extrude056  label="Extrude scavo saldature rumble"
  Base = -> Sketch053
  Dir = (0,-1,2e-16)
  DirMode = 2
  FaceMakerClass = Part::FaceMakerBullseye
  FaceMakerMode = 3
  LengthFwd = 8.4
  LengthRev = 0
  Solid = true
  Symmetric = true
FEATURE [Sketcher::SketchObject] Sketch054  label="scavo saldature alimentatore connettore USB"
  ArcFitTolerance = 1e-06
  AttachmentSupport = -> [XZ_Plane]
  ExternalGeometry = -> [Sketch037]
  FullyConstrained = true
  MakeInternals = false
  MapMode = 5
  Placement = pos=(0,0,0) rot=(1,0,0;1.5708rad)
  sketch-geometry (4):
    g0: LineSegment StartX=-209.575 StartY=-80.4316 StartZ=0 EndX=-210.375 EndY=-80.4316 EndZ=0
    g1: LineSegment StartX=-210.375 StartY=-80.4316 StartZ=0 EndX=-210.375 EndY=-72.4316 EndZ=0
    g2: LineSegment StartX=-210.375 StartY=-72.4316 StartZ=0 EndX=-209.575 EndY=-72.4316 EndZ=0
    g3: LineSegment StartX=-209.575 StartY=-72.4316 StartZ=0 EndX=-209.575 EndY=-80.4316 EndZ=0
  constraints (11):
    c: Horizontal(g0)
    c: Coincident(g1,g0)
    c: Vertical(g1)
    c: Coincident(g2,g1)
    c: Horizontal(g2)
    c: Coincident(g3,g2)
    c: Coincident(g3,g0)
    c: Vertical(g3)
    c: DistanceX(g0,g0) = 0.8
    c: DistanceY(g3,g3) = 8
    c: Coincident(g0,g-4)
FEATURE [Part::Extrusion] Extrude057  label="Extrude scavo saldature alimentatore connettore USB"
  Base = -> Sketch054
  Dir = (0,-1,2e-16)
  DirMode = 2
  FaceMakerClass = Part::FaceMakerBullseye
  FaceMakerMode = 3
  LengthFwd = 11
  LengthRev = 0
  Solid = true
  Symmetric = true
FEATURE [Sketcher::SketchObject] Sketch055  label="buco interno per micro switch"
  ArcFitTolerance = 1e-06
  AttachmentSupport = -> [XZ_Plane]
  ExternalGeometry = -> [Sketch]
  FullyConstrained = true
  MakeInternals = false
  MapMode = 5
  Placement = pos=(0,0,0) rot=(1,0,0;1.5708rad)
  sketch-geometry (11):
    g0: LineSegment [constr] StartX=-194.483 StartY=34.2854 StartZ=0 EndX=-196.022 EndY=30.0568 EndZ=0
    g1: LineSegment [constr] StartX=-196.022 StartY=30.0568 StartZ=0 EndX=-197.561 EndY=25.8282 EndZ=0
    g2: LineSegment [constr] StartX=-196.022 StartY=30.0568 StartZ=0 EndX=-194.143 EndY=29.3727 EndZ=0
    g3: LineSegment [constr] StartX=-196.022 StartY=30.0568 StartZ=0 EndX=-197.902 EndY=30.7408 EndZ=0
    g4: LineSegment StartX=-196.362 StartY=34.9694 StartZ=0 EndX=-192.604 EndY=33.6014 EndZ=0
    g5: LineSegment StartX=-199.441 StartY=26.5122 StartZ=0 EndX=-195.682 EndY=25.1441 EndZ=0
    g6: LineSegment StartX=-192.604 StartY=33.6014 StartZ=0 EndX=-195.682 EndY=25.1441 EndZ=0
    g7: LineSegment StartX=-196.362 StartY=34.9694 StartZ=0 EndX=-199.441 EndY=26.5122 EndZ=0
    g8: GeomPoint [constr] X=-187.821 Y=29.2 Z=0
    g9: LineSegment [constr] StartX=-188.505 StartY=27.3206 StartZ=0 EndX=-196.022 EndY=30.0568 EndZ=0
    g10: LineSegment [constr] StartX=-187.821 StartY=29.2 StartZ=0 EndX=-188.505 EndY=27.3206 EndZ=0
  constraints (27):
    c: Coincident(g2,g0)
    c: Parallel(g0,g-3)
    c: Tangent(g1,g0) = -1.5708
    c: Perpendicular(g0,g2)
    c: Tangent(g2,g3)
    c: Distance(g0,g1) = 9
    c: Equal(g0,g1)
    c: Distance(g3,g2) = 4
    c: Equal(g2,g3)
    c: Parallel(g3,g4)
    c: Symmetric(g4,g4,g0)
    c: Parallel(g6,g1)
    c: Parallel(g7,g1)
    c: Symmetric(g6,g6,g2)
    c: Symmetric(g5,g5,g1)
    c: Symmetric(g7,g7,g3)
    c: Coincident(g7,g4)
    c: Coincident(g6,g4)
    c: Coincident(g5,g6)
    c: Symmetric(g-3,g-3,g8)
    c: Perpendicular(g-3,g9)
    c: Distance(g9) = 8
    c: Coincident(g3,g9)
    c: Coincident(g10,g8)
    c: Parallel(g10,g-3)
    c: Distance(g10) = 2
    c: Coincident(g10,g9)
FEATURE [Sketcher::SketchObject] Sketch056  label="buco esterno per micro switch"
  ArcFitTolerance = 1e-06
  AttachmentSupport = -> [XZ_Plane]
  ExternalGeometry = -> [Sketch055]
  FullyConstrained = true
  MakeInternals = false
  MapMode = 5
  Placement = pos=(0,0,0) rot=(1,0,0;1.5708rad)
  sketch-geometry (17):
    g0: GeomPoint [constr] X=-194.143 Y=29.3727 Z=0
    g1: GeomPoint [constr] X=-194.483 Y=34.2854 Z=0
    g2: GeomPoint [constr] X=-197.902 Y=30.7408 Z=0
    g3: GeomPoint [constr] X=-197.561 Y=25.8282 Z=0
    g4: GeomPoint [constr] X=-196.022 Y=30.0568 Z=0
    g5: LineSegment [constr] StartX=-194.483 StartY=34.2854 StartZ=0 EndX=-196.022 EndY=30.0568 EndZ=0
    g6: LineSegment [constr] StartX=-196.022 StartY=30.0568 StartZ=0 EndX=-197.561 EndY=25.8282 EndZ=0
    g7: LineSegment [constr] StartX=-197.902 StartY=30.7408 StartZ=0 EndX=-196.022 EndY=30.0568 EndZ=0
    g8: LineSegment [constr] StartX=-196.022 StartY=30.0568 StartZ=0 EndX=-194.143 EndY=29.3727 EndZ=0
    g9: LineSegment [constr] StartX=-195.338 StartY=31.9362 StartZ=0 EndX=-196.022 EndY=30.0568 EndZ=0
    g10: LineSegment [constr] StartX=-196.022 StartY=30.0568 StartZ=0 EndX=-196.706 EndY=28.1774 EndZ=0
    g11: LineSegment [constr] StartX=-196.022 StartY=30.0568 StartZ=0 EndX=-196.821 EndY=30.3475 EndZ=0
    g12: LineSegment [constr] StartX=-196.022 StartY=30.0568 StartZ=0 EndX=-195.223 EndY=29.7661 EndZ=0
    g13: LineSegment StartX=-194.539 StartY=31.6454 StartZ=0 EndX=-195.907 EndY=27.8867 EndZ=0
    g14: LineSegment StartX=-196.137 StartY=32.2269 StartZ=0 EndX=-197.505 EndY=28.4681 EndZ=0
    g15: LineSegment StartX=-196.137 StartY=32.2269 StartZ=0 EndX=-194.539 EndY=31.6454 EndZ=0
    g16: LineSegment StartX=-197.505 StartY=28.4681 StartZ=0 EndX=-195.907 EndY=27.8867 EndZ=0
  constraints (34):
    c: Symmetric(g-5,g-5,g1)
    c: Symmetric(g-5,g-6,g0)
    c: Symmetric(g-6,g-6,g3)
    c: Symmetric(g-5,g-6,g2)
    c: Coincident(g5,g1)
    c: Coincident(g5,g4)
    c: Coincident(g6,g4)
    c: Coincident(g6,g3)
    c: Equal(g5,g6)
    c: Coincident(g7,g2)
    c: Coincident(g7,g4)
    c: Coincident(g8,g4)
    c: Coincident(g8,g0)
    c: Equal(g7,g8)
    c: Coincident(g11,g9)
    c: Coincident(g12,g9)
    c: Tangent(g10,g9) = -1.5708
    c: Perpendicular(g11,g9)
    c: Parallel(g9,g-4)
    c: Equal(g9,g10)
    c: Parallel(g12,g11)
    c: Equal(g11,g12)
    c: Distance(g11,g12) = 1.7
    c: Distance(g9,g10) = 4
    c: Symmetric(g13,g13,g12)
    c: Parallel(g13,g9)
    c: Symmetric(g14,g14,g11)
    c: Symmetric(g15,g15,g9)
    c: Parallel(g15,g11)
    c: Symmetric(g16,g16,g10)
    c: Coincident(g16,g14)
    c: Coincident(g15,g14)
    c: Coincident(g13,g15)
    c: Coincident(g9,g4)
FEATURE [Sketcher::SketchObject] Sketch057  label="buco interno per SWITCH"
  ArcFitTolerance = 1e-06
  AttachmentSupport = -> [XZ_Plane]
  ExternalGeometry = -> [Sketch]
  FullyConstrained = true
  MakeInternals = false
  MapMode = 5
  Placement = pos=(0,0,0) rot=(1,0,0;1.5708rad)
  sketch-geometry (10):
    g0: GeomPoint [constr] X=-187.821 Y=29.2 Z=0
    g1: LineSegment [constr] StartX=-188.505 StartY=27.3206 StartZ=0 EndX=-193.203 EndY=29.0307 EndZ=0
    g2: LineSegment [constr] StartX=-190.809 StartY=35.6086 StartZ=0 EndX=-195.597 EndY=22.4529 EndZ=0
    g3: GeomPoint [constr] X=-193.203 Y=29.0307 Z=0
    g4: LineSegment [constr] StartX=-196.492 StartY=30.2278 StartZ=0 EndX=-189.914 EndY=27.8336 EndZ=0
    g5: LineSegment StartX=-194.098 StartY=36.8056 StartZ=0 EndX=-187.52 EndY=34.4115 EndZ=0
    g6: LineSegment StartX=-194.098 StartY=36.8056 StartZ=0 EndX=-198.886 EndY=23.6499 EndZ=0
    g7: LineSegment StartX=-187.52 StartY=34.4115 StartZ=0 EndX=-192.308 EndY=21.2558 EndZ=0
    g8: LineSegment StartX=-198.886 StartY=23.6499 StartZ=0 EndX=-192.308 EndY=21.2558 EndZ=0
    g9: LineSegment [constr] StartX=-187.821 StartY=29.2 StartZ=0 EndX=-188.505 EndY=27.3206 EndZ=0
  constraints (23):
    c: Symmetric(g-3,g-3,g0)
    c: Perpendicular(g1,g-3)
    c: Parallel(g2,g-3)
    c: Symmetric(g2,g2,g3)
    c: Perpendicular(g2,g4)
    c: Symmetric(g4,g4,g3)
    c: Distance(g2) = 14
    c: Distance(g4) = 7
    c: Distance(g1) = 5
    c: Parallel(g5,g4)
    c: Parallel(g7,g2)
    c: Symmetric(g5,g5,g2)
    c: Symmetric(g6,g6,g4)
    c: Symmetric(g7,g7,g4)
    c: Symmetric(g8,g8,g2)
    c: Coincident(g6,g5)
    c: Coincident(g7,g5)
    c: Coincident(g8,g7)
    c: Coincident(g3,g1)
    c: Coincident(g9,g0)
    c: Parallel(g9,g-3)
    c: Distance(g9) = 2
    c: Coincident(g1,g9)
FEATURE [Sketcher::SketchObject] Sketch058  label="buco esterno per SWITCH"
  ArcFitTolerance = 1e-06
  AttachmentSupport = -> [XZ_Plane]
  ExternalGeometry = -> [Sketch057]
  FullyConstrained = true
  MakeInternals = false
  MapMode = 5
  Placement = pos=(0,0,0) rot=(1,0,0;1.5708rad)
  sketch-geometry (12):
    g0: GeomPoint [constr] X=-190.809 Y=35.6086 Z=0
    g1: GeomPoint [constr] X=-196.492 Y=30.2278 Z=0
    g2: GeomPoint [constr] X=-189.914 Y=27.8336 Z=0
    g3: GeomPoint [constr] X=-195.597 Y=22.4529 Z=0
    g4: GeomPoint [constr] X=-193.203 Y=29.0307 Z=0
    g5: LineSegment [constr] StartX=-192.006 StartY=32.3196 StartZ=0 EndX=-194.4 EndY=25.7418 EndZ=0
    g6: GeomPoint [constr] X=-193.203 Y=29.0307 Z=0
    g7: LineSegment [constr] StartX=-195.082 StartY=29.7148 StartZ=0 EndX=-191.324 EndY=28.3467 EndZ=0
    g8: LineSegment StartX=-193.885 StartY=33.0037 StartZ=0 EndX=-190.127 EndY=31.6356 EndZ=0
    g9: LineSegment StartX=-190.127 StartY=31.6356 StartZ=0 EndX=-192.521 EndY=25.0578 EndZ=0
    g10: LineSegment StartX=-196.28 StartY=26.4258 StartZ=0 EndX=-192.521 EndY=25.0578 EndZ=0
    g11: LineSegment StartX=-193.885 StartY=33.0037 StartZ=0 EndX=-196.28 EndY=26.4258 EndZ=0
  constraints (21):
    c: Symmetric(g-6,g-6,g3)
    c: Symmetric(g-4,g-6,g2)
    c: Symmetric(g-5,g-4,g0)
    c: Symmetric(g-5,g-6,g1)
    c: Symmetric(g1,g2,g4)
    c: Parallel(g5,g-4)
    c: Symmetric(g5,g5,g6)
    c: Perpendicular(g7,g5)
    c: Symmetric(g7,g7,g6)
    c: Distance(g5) = 7
    c: Distance(g7) = 4
    c: Parallel(g8,g7)
    c: Parallel(g11,g5)
    c: Symmetric(g8,g8,g5)
    c: Symmetric(g9,g9,g7)
    c: Symmetric(g10,g10,g5)
    c: Symmetric(g11,g11,g7)
    c: Coincident(g11,g8)
    c: Coincident(g9,g8)
    c: Coincident(g9,g10)
    c: Coincident(g6,g4)
FEATURE [Part::Extrusion] Extrude060  label="Extrude buco interno per SWITCH destro"
  Base = -> Sketch057
  Dir = (0,-1,2e-16)
  DirMode = 2
  FaceMakerClass = Part::FaceMakerBullseye
  FaceMakerMode = 3
  LengthFwd = 13.2
  LengthRev = 0
  Placement = pos=(0,2.6,0) rot=(0,0,1;0rad)
  Solid = true
  Symmetric = false
FEATURE [Part::Extrusion] Extrude061  label="Extrude buco esterno per SWITCH destro"
  Base = -> Sketch058
  Dir = (0,-1,2e-16)
  DirMode = 2
  FaceMakerClass = Part::FaceMakerBullseye
  FaceMakerMode = 3
  LengthFwd = 2
  LengthRev = 0
  Placement = pos=(0,-10.6,0) rot=(0,0,1;0rad)
  Solid = true
  Symmetric = false
FEATURE [Sketcher::SketchObject] Sketch059  label="buco per spazio introduzione SWITCH"
  ArcFitTolerance = 1e-06
  AttachmentSupport = -> [XZ_Plane]
  ExternalGeometry = -> [Sketch057,Sketch010]
  FullyConstrained = true
  MakeInternals = false
  MapMode = 5
  Placement = pos=(0,0,0) rot=(1,0,0;1.5708rad)
  sketch-geometry (8):
    g0: LineSegment [constr] StartX=-201.368 StartY=36.3521 StartZ=0 EndX=-195.094 EndY=34.0687 EndZ=0
    g1: LineSegment [constr] StartX=-194.098 StartY=36.8056 StartZ=0 EndX=-195.094 EndY=34.0687 EndZ=0
    g2: LineSegment StartX=-198.658 StartY=24.2771 StartZ=0 EndX=-199.654 EndY=21.5401 EndZ=0
    g3: LineSegment StartX=-199.654 StartY=21.5401 StartZ=0 EndX=-181.196 EndY=14.822 EndZ=0
    g4: LineSegment StartX=-181.196 StartY=14.822 StartZ=0 EndX=-180.2 EndY=17.559 EndZ=0
    g5: LineSegment StartX=-180.2 StartY=17.559 StartZ=0 EndX=-198.658 EndY=24.2771 EndZ=0
    g6: LineSegment [constr] StartX=-204.932 StartY=26.5605 StartZ=0 EndX=-198.658 EndY=24.2771 EndZ=0
    g7: LineSegment [constr] StartX=-198.658 StartY=24.2771 StartZ=0 EndX=-199.654 EndY=21.5401 EndZ=0
  constraints (20):
    c: Parallel(g1,g-3)
    c: Parallel(g0,g-4)
    c: Coincident(g0,g-4)
    c: Coincident(g1,g-3)
    c: Coincident(g0,g1)
    c: Coincident(g3,g2)
    c: Coincident(g4,g3)
    c: Coincident(g5,g4)
    c: Coincident(g5,g2)
    c: Parallel(g5,g-5)
    c: Parallel(g3,g-5)
    c: Parallel(g4,g-6)
    c: DistanceX(g-6,g4) = 0
    c: Coincident(g6,g-5)
    c: Equal(g6,g0)
    c: Coincident(g7,g6)
    c: Equal(g7,g1)
    c: Tangent(g7,g-3)
    c: Coincident(g2,g6)
    c: Coincident(g2,g7)
FEATURE [Part::Extrusion] Extrude062  label="Extrude buco per spazio introduzione SWITCH"
  Base = -> Sketch059
  Dir = (0,-1,2e-16)
  DirMode = 2
  FaceMakerClass = Part::FaceMakerBullseye
  FaceMakerMode = 3
  LengthFwd = 13.2
  LengthRev = 0
  Solid = true
  Symmetric = true
FEATURE [Part::Extrusion] Extrude063  label="Extrude buco interno per SWITCH sinistro"
  Base = -> Sketch057
  Dir = (0,-1,2e-16)
  DirMode = 2
  FaceMakerClass = Part::FaceMakerBullseye
  FaceMakerMode = 3
  LengthFwd = 13.2
  LengthRev = 0
  Placement = pos=(0,10.6,0) rot=(0,0,1;0rad)
  Solid = true
  Symmetric = false
FEATURE [Part::Extrusion] Extrude064  label="Extrude buco esterno per SWITCH sinistro"
  Base = -> Sketch058
  Dir = (0,-1,2e-16)
  DirMode = 2
  FaceMakerClass = Part::FaceMakerBullseye
  FaceMakerMode = 3
  LengthFwd = 2
  LengthRev = 0
  Placement = pos=(0,12.6,0) rot=(0,0,1;0rad)
  Solid = true
  Symmetric = false
FEATURE [Sketcher::SketchObject] Sketch061  label="struttura esterna blocco switch"
  ArcFitTolerance = 1e-06
  AttachmentSupport = -> [XZ_Plane003]
  FullyConstrained = true
  MakeInternals = false
  MapMode = 5
  Placement = pos=(0,0,0) rot=(1,0,0;1.5708rad)
  sketch-geometry (5):
    g0: LineSegment StartX=-1 StartY=-5.1 StartZ=0 EndX=1 EndY=-5.1 EndZ=0
    g1: LineSegment StartX=1 StartY=-5.1 StartZ=0 EndX=1 EndY=5.1 EndZ=0
    g2: LineSegment StartX=1 StartY=5.1 StartZ=0 EndX=-1 EndY=5.1 EndZ=0
    g3: LineSegment StartX=-1 StartY=5.1 StartZ=0 EndX=-1 EndY=-5.1 EndZ=0
    g4: GeomPoint [constr] X=0 Y=0 Z=0
  constraints (12):
    c: Coincident(g0,g1)
    c: Coincident(g1,g2)
    c: Coincident(g2,g3)
    c: Coincident(g3,g0)
    c: Horizontal(g0)
    c: Horizontal(g2)
    c: Vertical(g1)
    c: Vertical(g3)
    c: Symmetric(g2,g0,g4)
    c: Distance(g1,g3) = 2
    c: Distance(g0,g2) = 10.2
    c: Coincident(g4,g-1)
FEATURE [Sketcher::SketchObject] Sketch062  label="struttura interna blocco switch"
  ArcFitTolerance = 1e-06
  AttachmentSupport = -> [XZ_Plane003]
  ExternalGeometry = -> [Sketch061]
  FullyConstrained = true
  MakeInternals = false
  MapMode = 5
  Placement = pos=(0,0,0) rot=(1,0,0;1.5708rad)
  sketch-geometry (5):
    g0: LineSegment StartX=-1 StartY=3.1 StartZ=0 EndX=-1 EndY=-3.1 EndZ=0
    g1: LineSegment StartX=-1 StartY=-3.1 StartZ=0 EndX=1 EndY=-3.1 EndZ=0
    g2: LineSegment StartX=1 StartY=-3.1 StartZ=0 EndX=1 EndY=3.1 EndZ=0
    g3: LineSegment StartX=1 StartY=3.1 StartZ=0 EndX=-1 EndY=3.1 EndZ=0
    g4: GeomPoint [constr] X=0 Y=0 Z=0
  constraints (12):
    c: Coincident(g0,g1)
    c: Coincident(g1,g2)
    c: Coincident(g2,g3)
    c: Coincident(g3,g0)
    c: Vertical(g0)
    c: Vertical(g2)
    c: Horizontal(g1)
    c: Horizontal(g3)
    c: Symmetric(g2,g0,g4)
    c: Coincident(g4,g-1)
    c: Distance(g0) = 6.2
    c: Equal(g3,g-3)
FEATURE [Sketcher::SketchObject] Sketch063  label="blocchi tra switch"
  ArcFitTolerance = 1e-06
  AttachmentSupport = -> [XZ_Plane003]
  ExternalGeometry = -> [Sketch061,Sketch062]
  FullyConstrained = true
  MakeInternals = false
  MapMode = 5
  Placement = pos=(0,0,0) rot=(1,0,0;1.5708rad)
  sketch-geometry (8):
    g0: LineSegment StartX=-3 StartY=5.1 StartZ=0 EndX=-1 EndY=5.1 EndZ=0
    g1: LineSegment StartX=-1 StartY=5.1 StartZ=0 EndX=-1 EndY=3.1 EndZ=0
    g2: LineSegment StartX=-1 StartY=3.1 StartZ=0 EndX=-3 EndY=3.1 EndZ=0
    g3: LineSegment StartX=-3 StartY=3.1 StartZ=0 EndX=-3 EndY=5.1 EndZ=0
    g4: LineSegment StartX=-3 StartY=-3.1 StartZ=0 EndX=-1 EndY=-3.1 EndZ=0
    g5: LineSegment StartX=-1 StartY=-3.1 StartZ=0 EndX=-1 EndY=-5.1 EndZ=0
    g6: LineSegment StartX=-1 StartY=-5.1 StartZ=0 EndX=-3 EndY=-5.1 EndZ=0
    g7: LineSegment StartX=-3 StartY=-5.1 StartZ=0 EndX=-3 EndY=-3.1 EndZ=0
  constraints (20):
    c: Horizontal(g0)
    c: Coincident(g1,g0)
    c: Coincident(g2,g1)
    c: Horizontal(g2)
    c: Coincident(g3,g2)
    c: Coincident(g3,g0)
    c: Vertical(g3)
    c: Horizontal(g4)
    c: Coincident(g5,g4)
    c: Coincident(g6,g5)
    c: Horizontal(g6)
    c: Coincident(g7,g6)
    c: Coincident(g7,g4)
    c: Vertical(g7)
    c: Coincident(g0,g-4)
    c: Coincident(g1,g-5)
    c: Coincident(g4,g-6)
    c: Coincident(g5,g-7)
    c: Distance(g0) = 2
    c: Distance(g4) = 2
FEATURE [Sketcher::SketchObject] Sketch066  label="piano per rampino"
  ArcFitTolerance = 1e-06
  AttachmentSupport = -> [XZ_Plane002]
  ExternalGeometry = -> [Sketch045]
  FullyConstrained = true
  MakeInternals = false
  MapMode = 5
  Placement = pos=(0,0,0) rot=(1,0,0;1.5708rad)
  sketch-geometry (4):
    g0: LineSegment StartX=5.4 StartY=5.1 StartZ=0 EndX=5.4 EndY=3.9 EndZ=0
    g1: LineSegment StartX=5.4 StartY=3.9 StartZ=0 EndX=7 EndY=3.9 EndZ=0
    g2: LineSegment StartX=7 StartY=3.9 StartZ=0 EndX=7 EndY=5.1 EndZ=0
    g3: LineSegment StartX=7 StartY=5.1 StartZ=0 EndX=5.4 EndY=5.1 EndZ=0
  constraints (11):
    c: Coincident(g0,g1)
    c: Coincident(g1,g2)
    c: Coincident(g2,g3)
    c: Coincident(g3,g0)
    c: Vertical(g0)
    c: Vertical(g2)
    c: Horizontal(g1)
    c: Horizontal(g3)
    c: Distance(g0,g2) = 1.6
    c: Distance(g1,g3) = 1.2
    c: Coincident(g2,g-3)
FEATURE [Sketcher::SketchObject] Sketch064  label="rampini_per_serraggio_struttura"
  ArcFitTolerance = 1e-06
  AttachmentSupport = -> [XZ_Plane002]
  ExternalGeometry = -> [Sketch066,Sketch045]
  FullyConstrained = true
  MakeInternals = false
  MapMode = 5
  Placement = pos=(0,0,0) rot=(1,0,0;1.5708rad)
  sketch-geometry (7):
    g0: LineSegment StartX=7 StartY=5.1 StartZ=0 EndX=7 EndY=3.9 EndZ=0
    g1: LineSegment StartX=7 StartY=3.9 StartZ=0 EndX=9 EndY=3.9 EndZ=0
    g2: LineSegment StartX=7 StartY=5.1 StartZ=0 EndX=7 EndY=5.1 EndZ=0
    g3: LineSegment StartX=7 StartY=5.1 StartZ=0 EndX=7 EndY=7.5 EndZ=0
    g4: LineSegment StartX=9 StartY=5.1 StartZ=0 EndX=9 EndY=3.9 EndZ=0
    g5: LineSegment StartX=7 StartY=7.5 StartZ=0 EndX=9 EndY=7.5 EndZ=0
    g6: LineSegment StartX=9 StartY=7.5 StartZ=0 EndX=9 EndY=5.1 EndZ=0
  constraints (20):
    c: Vertical(g0)
    c: Coincident(g1,g0)
    c: Horizontal(g1)
    c: Coincident(g2,g0)
    c: Horizontal(g2)
    c: Coincident(g3,g2)
    c: Vertical(g3)
    c: Coincident(g5,g3)
    c: Coincident(g4,g6)
    c: Coincident(g4,g1)
    c: Vertical(g4)
    c: Coincident(g0,g-3)
    c: DistanceY(g-4,g3) = 2.4
    c: DistanceX(g1,g1) = 2
    c: DistanceY(g2,g6) = 0
    c: DistanceX(g2,g2) = 0
    c: DistanceY(g0,g0) = 1.2
    c: Coincident(g5,g6)
    c: Horizontal(g5)
    c: Vertical(g6)
FEATURE [Sketcher::SketchObject] Sketch067  label="perno per blocco switch"
  ArcFitTolerance = 1e-06
  AttachmentSupport = -> [XZ_Plane]
  ExternalGeometry = -> [Sketch,Sketch010]
  FullyConstrained = true
  MakeInternals = false
  MapMode = 5
  Placement = pos=(0,0,0) rot=(1,0,0;1.5708rad)
  sketch-geometry (14):
    g0: LineSegment StartX=-191.073 StartY=24.9429 StartZ=0 EndX=-185.81 EndY=23.0276 EndZ=0
    g1: LineSegment StartX=-183.76 StartY=23.9839 StartZ=0 EndX=-182.392 EndY=27.7427 EndZ=0
    g2: LineSegment StartX=-183.348 StartY=29.7934 StartZ=0 EndX=-188.61 EndY=31.7087 EndZ=0
    g3: LineSegment StartX=-188.61 StartY=31.7087 StartZ=0 EndX=-191.073 EndY=24.9429 EndZ=0
    g4: GeomPoint [constr] X=-186.459 Y=27.0946 Z=0
    g5: LineSegment StartX=-189.022 StartY=25.8992 StartZ=0 EndX=-185.263 EndY=24.5311 EndZ=0
    g6: LineSegment StartX=-185.263 StartY=24.5311 StartZ=0 EndX=-183.895 EndY=28.2899 EndZ=0
    g7: LineSegment StartX=-183.895 StartY=28.2899 StartZ=0 EndX=-187.654 EndY=29.658 EndZ=0
    g8: LineSegment StartX=-187.654 StartY=29.658 StartZ=0 EndX=-189.022 EndY=25.8992 EndZ=0
    g9: GeomPoint [constr] X=-186.459 Y=27.0946 Z=0
    g10: ArcOfCircle CenterX=-185.263 CenterY=24.5311 CenterZ=0 NormalX=0 NormalY=0 NormalZ=1 AngleXU=0 Radius=1.6 StartAngle=4.36332 EndAngle=5.93412
    g11: GeomPoint [constr] X=-184.307 Y=22.4804 Z=0
    g12: ArcOfCircle CenterX=-183.895 CenterY=28.2899 CenterZ=0 NormalX=0 NormalY=0 NormalZ=1 AngleXU=0 Radius=1.6 StartAngle=5.93412 EndAngle=7.50492
    g13: GeomPoint [constr] X=-181.844 Y=29.2462 Z=0
  constraints (30):
    c: Coincident(g2,g3)
    c: Coincident(g3,g0)
    c: Symmetric(g13,g0,g4)
    c: Distance(g11,g3) = 7.2
    c: Distance(g0,g2) = 7.2
    c: Parallel(g3,g1)
    c: Parallel(g2,g0)
    c: Perpendicular(g2,g3)
    c: Coincident(g5,g6)
    c: Coincident(g6,g7)
    c: Coincident(g7,g8)
    c: Coincident(g8,g5)
    c: Symmetric(g7,g5,g9)
    c: Distance(g6,g8) = 4
    c: Distance(g5,g7) = 4
    c: Coincident(g9,g4)
    c: Parallel(g8,g6)
    c: Parallel(g7,g5)
    c: Perpendicular(g7,g8)
    c: Tangent(g8,g-3)
    c: Tangent(g2,g-4)
    c: PointOnObject(g11,g1)
    c: PointOnObject(g11,g0)
    c: Tangent(g1,g10) = -1.5708
    c: Tangent(g0,g10) = -1.5708
    c: PointOnObject(g13,g1)
    c: Tangent(g1,g12) = -1.5708
    c: Tangent(g2,g12) = -1.5708
    c: Equal(g10,g12)
    c: Coincident(g10,g5)
FEATURE [Part::Extrusion] Extrude072  label="Extrude perno per blocco switch"
  Base = -> Sketch067
  Dir = (0,-1,2e-16)
  DirMode = 2
  FaceMakerClass = Part::FaceMakerBullseye
  FaceMakerMode = 3
  LengthFwd = 25.2
  LengthRev = 0
  Solid = true
  Symmetric = true
FEATURE [Part::MultiFuse] Fusion
  Refine = true
  Shapes = -> [Extrude,Sweep,Extrude007,Extrude011,Extrude005,Extrude012,Extrude013,Extrude016,Extrude031,Extrude039,Extrude045,Extrude072]
FEATURE [Part::Cut] Cut
  Base = -> Fusion
  Refine = true
  Tool = -> Extrude001
FEATURE [Part::Cut] Cut001
  Base = -> Cut
  Refine = true
  Tool = -> Extrude004
FEATURE [Part::Cut] Cut002
  Base = -> Cut001
  Refine = true
  Tool = -> Extrude006
FEATURE [Part::Cut] Cut003
  Base = -> Cut002
  Refine = true
  Tool = -> Extrude008
FEATURE [Part::Cut] Cut004
  Base = -> Cut003
  Refine = true
  Tool = -> Extrude009
FEATURE [Part::Cut] Cut005
  Base = -> Cut004
  Refine = true
  Tool = -> Extrude010
FEATURE [Part::Cut] Cut006
  Base = -> Cut005
  Refine = true
  Tool = -> Extrude014
FEATURE [Part::Cut] Cut007
  Base = -> Cut006
  Refine = true
  Tool = -> Extrude015
FEATURE [Part::Cut] Cut008
  Base = -> Cut007
  Refine = true
  Tool = -> Extrude018
FEATURE [Part::Cut] Cut009
  Base = -> Cut008
  Refine = true
  Tool = -> Extrude019
FEATURE [Part::Cut] Cut010
  Base = -> Cut009
  Refine = true
  Tool = -> Extrude020
FEATURE [Part::Cut] Cut011
  Base = -> Cut010
  Refine = true
  Tool = -> Extrude021
FEATURE [Part::Cut] Cut012
  Base = -> Cut011
  Refine = true
  Tool = -> Extrude022
FEATURE [Part::Cut] Cut013
  Base = -> Cut012
  Refine = true
  Tool = -> Extrude023
FEATURE [Part::Cut] Cut014
  Base = -> Cut013
  Refine = true
  Tool = -> Extrude032
FEATURE [Part::Cut] Cut015
  Base = -> Cut014
  Refine = true
  Tool = -> Extrude033
FEATURE [Part::Cut] Cut016
  Base = -> Cut015
  Refine = true
  Tool = -> Extrude034
FEATURE [Part::Cut] Cut017
  Base = -> Cut016
  Refine = true
  Tool = -> Extrude035
FEATURE [Part::Cut] Cut018
  Base = -> Cut017
  Refine = true
  Tool = -> Extrude036
FEATURE [Part::Cut] Cut019
  Base = -> Cut018
  Refine = true
  Tool = -> Extrude037
FEATURE [Part::Cut] Cut020
  Base = -> Cut019
  Refine = true
  Tool = -> Extrude030
FEATURE [Part::Cut] Cut022
  Base = -> Cut020
  Refine = true
  Tool = -> Extrude038
FEATURE [Part::Cut] Cut023
  Base = -> Cut022
  Refine = true
  Tool = -> Extrude041
FEATURE [Part::Cut] Cut024
  Base = -> Cut023
  Refine = true
  Tool = -> Extrude040
FEATURE [Part::Cut] Cut025
  Base = -> Cut024
  Refine = true
  Tool = -> Extrude042
FEATURE [Part::Cut] Cut026
  Base = -> Cut025
  Refine = true
  Tool = -> Extrude043
FEATURE [Part::Cut] Cut027
  Base = -> Cut026
  Refine = true
  Tool = -> Extrude044
FEATURE [Part::Cut] Cut028
  Base = -> Cut027
  Refine = true
  Tool = -> Extrude046
FEATURE [Part::Cut] Cut029
  Base = -> Cut028
  Refine = true
  Tool = -> Extrude047
FEATURE [Part::Cut] Cut033
  Base = -> Cut029
  Refine = true
  Tool = -> Extrude055
FEATURE [Part::Cut] Cut034
  Base = -> Cut033
  Refine = true
  Tool = -> Extrude056
FEATURE [Part::Cut] Cut035
  Base = -> Cut034
  Refine = true
  Tool = -> Extrude057
FEATURE [Part::Cut] Cut037
  Base = -> Cut035
  Refine = true
  Tool = -> Extrude060
FEATURE [Part::Cut] Cut038
  Base = -> Cut037
  Refine = true
  Tool = -> Extrude061
FEATURE [Part::Cut] Cut039
  Base = -> Cut038
  Refine = true
  Tool = -> Extrude063
FEATURE [Part::Cut] Cut040
  Base = -> Cut039
  Refine = true
  Tool = -> Extrude064
FEATURE [Part::Cut] Cut041
  Base = -> Cut040
  Refine = true
  Tool = -> Extrude062
FEATURE [Sketcher::SketchObject] Sketch068  label="base con smusso sopra neopixel"
  ArcFitTolerance = 1e-06
  AttachmentSupport = -> [YZ_Plane002]
  FullyConstrained = true
  MakeInternals = false
  MapMode = 5
  Placement = pos=(0,0,0) rot=(0.57735,0.57735,0.57735;2.0944rad)
  sketch-geometry (5):
    g0: LineSegment StartX=-9.5 StartY=-6.1 StartZ=0 EndX=9.5 EndY=-6.1 EndZ=0
    g1: LineSegment StartX=9.5 StartY=-6.1 StartZ=0 EndX=9.5 EndY=6.1 EndZ=0
    g2: LineSegment StartX=9.5 StartY=6.1 StartZ=0 EndX=-9.5 EndY=6.1 EndZ=0
    g3: LineSegment StartX=-9.5 StartY=6.1 StartZ=0 EndX=-9.5 EndY=-6.1 EndZ=0
    g4: GeomPoint [constr] X=0 Y=0 Z=0
  constraints (12):
    c: Coincident(g0,g1)
    c: Coincident(g1,g2)
    c: Coincident(g2,g3)
    c: Coincident(g3,g0)
    c: Horizontal(g0)
    c: Horizontal(g2)
    c: Vertical(g1)
    c: Vertical(g3)
    c: Symmetric(g2,g0,g4)
    c: Distance(g1,g3) = 19
    c: Distance(g0,g2) = 12.2
    c: Coincident(g4,g-1)
FEATURE [Sketcher::SketchObject] Sketch069  label="cilindro minore"
  ArcFitTolerance = 1e-06
  AttachmentSupport = -> [XZ_Plane004]
  FullyConstrained = true
  MakeInternals = false
  MapMode = 5
  Placement = pos=(0,0,0) rot=(1,0,0;1.5708rad)
  sketch-geometry (1):
    g0: Circle CenterX=0 CenterY=0 CenterZ=0 NormalX=0 NormalY=0 NormalZ=1 AngleXU=0 Radius=5.8
  constraints (2):
    c: Diameter(g0) = 11.6
    c: Coincident(g0,g-1)
FEATURE [Sketcher::SketchObject] Sketch070  label="cilindro maggiore"
  ArcFitTolerance = 1e-06
  AttachmentSupport = -> [XZ_Plane004]
  ExternalGeometry = -> [Sketch069]
  FullyConstrained = true
  MakeInternals = false
  MapMode = 5
  Placement = pos=(0,0,0) rot=(1,0,0;1.5708rad)
  sketch-geometry (1):
    g0: Circle CenterX=0 CenterY=0 CenterZ=0 NormalX=0 NormalY=0 NormalZ=1 AngleXU=0 Radius=6.5
  constraints (2):
    c: Coincident(g0,g-1)
    c: Diameter(g0) = 13
FEATURE [Sketcher::SketchObject] Sketch071  label="buco interno"
  ArcFitTolerance = 1e-06
  AttachmentSupport = -> [XZ_Plane004]
  ExternalGeometry = -> [Sketch069]
  FullyConstrained = true
  MakeInternals = false
  MapMode = 5
  Placement = pos=(0,0,0) rot=(1,0,0;1.5708rad)
  sketch-geometry (1):
    g0: Circle CenterX=0 CenterY=0 CenterZ=0 NormalX=0 NormalY=0 NormalZ=1 AngleXU=0 Radius=5
  constraints (2):
    c: Coincident(g0,g-1)
    c: Diameter(g0) = 10
FEATURE [PartDesign::Pad] Pad
  Direction = (0,-1,2e-16)
  Length = 1.2
  Length2 = 10
  Placement = pos=(0,0,0) rot=(1,0,0;1.5708rad)
  Profile = -> Sketch070
  ReferenceAxis = -> Sketch070 [N_Axis]
  Refine = true
  Suppressed = false
  Type = 0
FEATURE [PartDesign::Pad] Pad001
  BaseFeature = -> Pad
  Direction = (0,-1,2e-16)
  Length = 5.6
  Length2 = 10
  Placement = pos=(0,0,0) rot=(1,0,0;1.5708rad)
  Profile = -> Sketch069
  ReferenceAxis = -> Sketch069 [N_Axis]
  Refine = true
  Suppressed = false
  Type = 0
FEATURE [PartDesign::Pocket] Pocket
  BaseFeature = -> Pad001
  Direction = (0,1,-2e-16)
  Length = 7
  Length2 = 5
  Midplane = true
  Placement = pos=(0,0,0) rot=(1,0,0;1.5708rad)
  Profile = -> Sketch071
  ReferenceAxis = -> Sketch071 [N_Axis]
  Refine = true
  Suppressed = false
  Type = 0
FEATURE [PartDesign::Fillet] Fillet
  Base = -> Pocket [Face7]
  BaseFeature = -> Pocket
  Placement = pos=(0,0,0) rot=(1,0,0;1.5708rad)
  Radius = 1
  Refine = true
  SupportTransform = false
  Suppressed = false
  UseAllEdges = false
FEATURE [PartDesign::Body] Body004  label="pulsanti lato sinistro"
  AllowCompound = false
  Group = -> [Sketch069,Sketch070,Sketch071,Pad,Pad001,Pocket,Fillet]
  Origin = -> Origin004
  Tip = -> Fillet
FEATURE [Sketcher::SketchObject] Sketch072  label="buco per saldature e diodo driver solenoide"
  ArcFitTolerance = 1e-06
  AttachmentSupport = -> [XZ_Plane]
  ExternalGeometry = -> [Sketch038]
  FullyConstrained = true
  MakeInternals = false
  MapMode = 5
  Placement = pos=(0,0,0) rot=(1,0,0;1.5708rad)
  sketch-geometry (4):
    g0: LineSegment StartX=-209.225 StartY=-40.6939 StartZ=0 EndX=-204.154 EndY=-29.8182 EndZ=0
    g1: LineSegment StartX=-204.154 StartY=-29.8182 StartZ=0 EndX=-206.51 EndY=-28.7194 EndZ=0
    g2: LineSegment StartX=-206.51 StartY=-28.7194 StartZ=0 EndX=-211.582 EndY=-39.5951 EndZ=0
    g3: LineSegment StartX=-211.582 StartY=-39.5951 StartZ=0 EndX=-209.225 EndY=-40.6939 EndZ=0
  constraints (11):
    c: Coincident(g1,g0)
    c: Coincident(g2,g1)
    c: Coincident(g3,g2)
    c: Coincident(g3,g0)
    c: Parallel(g-3,g0)
    c: Parallel(g0,g2)
    c: Perpendicular(g0,g3)
    c: Perpendicular(g1,g0)
    c: Distance(g3) = 2.6
    c: Distance(g2) = 12
    c: Coincident(g0,g-3)
FEATURE [Part::Extrusion] Extrude074  label="Extrude buco per saldature e diodo driver solenoide"
  Base = -> Sketch072
  Dir = (0,-1,2e-16)
  DirMode = 2
  FaceMakerClass = Part::FaceMakerBullseye
  FaceMakerMode = 3
  LengthFwd = 14.6
  LengthRev = 0
  Solid = true
  Symmetric = true
FEATURE [Part::Cut] Cut042
  Base = -> Cut041
  Refine = true
  Tool = -> Extrude074
FEATURE [Sketcher::SketchObject] Sketch073  label="fori slargati blocco solenoide"
  ArcFitTolerance = 1e-06
  AttachmentSupport = -> [XY_Plane]
  ExternalGeometry = -> [Sketch030]
  FullyConstrained = true
  MakeInternals = false
  MapMode = 5
  sketch-geometry (2):
    g0: Circle CenterX=-152.209 CenterY=6.95 CenterZ=0 NormalX=0 NormalY=0 NormalZ=1 AngleXU=0 Radius=3.7
    g1: Circle CenterX=-130.41 CenterY=-6.95 CenterZ=0 NormalX=0 NormalY=0 NormalZ=1 AngleXU=0 Radius=3.7
  constraints (4):
    c: Diameter(g0) = 7.4
    c: Coincident(g0,g-3)
    c: Diameter(g1) = 7.4
    c: Coincident(g1,g-4)
FEATURE [Part::Extrusion] Extrude075  label="Extrude fori slargati blocco solenoide"
  Base = -> Sketch073
  Dir = (0,0,1)
  DirMode = 2
  FaceMakerClass = Part::FaceMakerBullseye
  FaceMakerMode = 3
  LengthFwd = 1.5
  LengthRev = 0
  Placement = pos=(0,0,36.4) rot=(0,0,1;0rad)
  Solid = true
  Symmetric = false
FEATURE [Part::Cut] Cut043
  Base = -> Cut042
  Refine = true
  Tool = -> Extrude075
FEATURE [Sketcher::SketchObject] Sketch074  label="lato sx pistola"
  ArcFitTolerance = 1e-06
  AttachmentSupport = -> [XZ_Plane]
  ExternalGeometry = -> [Sketch016,Sketch,Sketch058]
  FullyConstrained = true
  MakeInternals = false
  MapMode = 5
  Placement = pos=(0,0,0) rot=(1,0,0;1.5708rad)
  sketch-geometry (37):
    g0: LineSegment StartX=-82.8 StartY=3.2 StartZ=0 EndX=0 EndY=3.2 EndZ=0
    g1: LineSegment StartX=-82.8 StartY=3.2 StartZ=0 EndX=-82.8 EndY=6.2 EndZ=0
    g2: LineSegment [constr] StartX=-107.6 StartY=18 StartZ=0 EndX=-107.6 EndY=20 EndZ=0
    g3: LineSegment [constr] StartX=-132.428 StartY=18 StartZ=0 EndX=-132.428 EndY=20 EndZ=0
    g4: LineSegment StartX=-132.428 StartY=20 StartZ=0 EndX=-107.6 EndY=20 EndZ=0
    g5: ArcOfCircle CenterX=-107.6 CenterY=4 CenterZ=0 NormalX=0 NormalY=0 NormalZ=1 AngleXU=0 Radius=16 StartAngle=0.137937 EndAngle=1.5708
    g6: LineSegment StartX=-82.8 StartY=6.2 StartZ=0 EndX=-91.752 EndY=6.2 EndZ=0
    g7: LineSegment [constr] StartX=-145.743 StartY=8.32624 StartZ=0 EndX=-147.645 EndY=8.94427 EndZ=0
    g8: ArcOfCircle CenterX=-132.428 CenterY=4 CenterZ=0 NormalX=0 NormalY=0 NormalZ=1 AngleXU=0 Radius=16 StartAngle=1.5708 EndAngle=2.82743
    g9: LineSegment StartX=-215.932 StartY=-80.4316 StartZ=0 EndX=-176.685 EndY=-80.4316 EndZ=0
    g10: LineSegment StartX=-147.645 StartY=8.94427 StartZ=0 EndX=-176.685 EndY=-80.4316 EndZ=0
    g11: LineSegment [constr] StartX=-193.988 StartY=-2.33927 StartZ=0 EndX=-192.176 EndY=-3.18451 EndZ=0
    g12: LineSegment [constr] StartX=-217.232 StartY=-52.1862 StartZ=0 EndX=-215.42 EndY=-53.0314 EndZ=0
    g13: LineSegment StartX=-192.176 StartY=-3.18451 StartZ=0 EndX=-215.42 EndY=-53.0314 EndZ=0
    g14: ArcOfCircle CenterX=-184.801 CenterY=-67.3089 CenterZ=0 NormalX=0 NormalY=0 NormalZ=1 AngleXU=0 Radius=33.7833 StartAngle=2.70526 EndAngle=3.54053
    g15: ArcOfCircle CenterX=-207.583 CenterY=4 CenterZ=0 NormalX=0 NormalY=0 NormalZ=1 AngleXU=0 Radius=17 StartAngle=5.84685 EndAngle=7.56663
    g16: LineSegment StartX=-202.765 StartY=20.303 StartZ=0 EndX=-195.887 EndY=39.2 EndZ=0
    g17: LineSegment [constr] StartX=-193.885 StartY=33.0037 StartZ=0 EndX=-197.644 EndY=34.3718 EndZ=0
    g18: LineSegment StartX=-195.887 StartY=39.2 StartZ=0 EndX=0 EndY=39.2 EndZ=0
    g19: LineSegment StartX=0 StartY=3.2 StartZ=0 EndX=0 EndY=39.2 EndZ=0
    g20: LineSegment StartX=-189.939 StartY=31.5672 StartZ=0 EndX=-192.333 EndY=24.9893 EndZ=0
    g21: LineSegment StartX=-196.467 StartY=26.4942 StartZ=0 EndX=-194.073 EndY=33.0721 EndZ=0
    g22: Circle CenterX=-213.443 CenterY=-76.8316 CenterZ=0 NormalX=0 NormalY=0 NormalZ=1 AngleXU=0 Radius=1.8
    g23: Circle CenterX=-179.305 CenterY=-76.8316 CenterZ=0 NormalX=0 NormalY=0 NormalZ=1 AngleXU=0 Radius=1.8
    g24: Circle CenterX=-184.08 CenterY=34.8 CenterZ=0 NormalX=0 NormalY=0 NormalZ=1 AngleXU=0 Radius=1.8
    g25: Circle CenterX=-78.51 CenterY=34.8 CenterZ=0 NormalX=0 NormalY=0 NormalZ=1 AngleXU=0 Radius=1.8
    g26: Circle CenterX=-78.51 CenterY=7.6 CenterZ=0 NormalX=0 NormalY=0 NormalZ=1 AngleXU=0 Radius=1.8
    g27: Circle CenterX=-5.6 CenterY=34.8 CenterZ=0 NormalX=0 NormalY=0 NormalZ=1 AngleXU=0 Radius=1.8
    g28: Circle CenterX=-5.6 CenterY=7.6 CenterZ=0 NormalX=0 NormalY=0 NormalZ=1 AngleXU=0 Radius=1.8
    g29: LineSegment StartX=-190.127 StartY=31.6356 StartZ=0 EndX=-189.939 EndY=31.5672 EndZ=0
    g30: LineSegment StartX=-194.073 StartY=33.0721 StartZ=0 EndX=-193.885 EndY=33.0037 EndZ=0
    g31: LineSegment StartX=-193.885 StartY=33.0037 StartZ=0 EndX=-190.127 EndY=31.6356 EndZ=0
    g32: LineSegment StartX=-196.467 StartY=26.4942 StartZ=0 EndX=-192.333 EndY=24.9893 EndZ=0
    g33: Circle CenterX=-19 CenterY=21.2 CenterZ=0 NormalX=0 NormalY=0 NormalZ=1 AngleXU=0 Radius=6.3
    g34: Circle CenterX=-42 CenterY=21.2 CenterZ=0 NormalX=0 NormalY=0 NormalZ=1 AngleXU=0 Radius=6.3
    g35: Circle CenterX=-65 CenterY=21.2 CenterZ=0 NormalX=0 NormalY=0 NormalZ=1 AngleXU=0 Radius=6.3
    g36: LineSegment [constr] StartX=-4 StartY=21.2 StartZ=0 EndX=-65 EndY=21.2 EndZ=0
  constraints (96):
    c: Coincident(g0,g-41)
    c: Horizontal(g0)
    c: PointOnObject(g0,g-39)
    c: Coincident(g1,g0)
    c: Vertical(g1)
    c: DistanceY(g1,g1) = 3
    c: Coincident(g2,g-17)
    c: Vertical(g2)
    c: Coincident(g3,g-16)
    c: Vertical(g3)
    c: DistanceY(g2,g2) = 2
    c: DistanceY(g3,g3) = 2
    c: Coincident(g4,g3)
    c: Coincident(g4,g2)
    c: Coincident(g5,g-17)
    c: Coincident(g5,g2)
    c: Coincident(g6,g1)
    c: Horizontal(g6)
    c: Coincident(g6,g5)
    c: Coincident(g7,g-15)
    c: Coincident(g8,g7)
    c: Coincident(g8,g3)
    c: Coincident(g8,g-15)
    c: Horizontal(g9)
    c: DistanceY(g-13,g9) = 2
    c: Coincident(g10,g7)
    c: Parallel(g10,g-14)
    c: Coincident(g9,g10)
    c: Distance(g11) = 2
    c: Coincident(g11,g-11)
    c: Perpendicular(g-11,g11)
    c: Distance(g12) = 2
    c: Coincident(g12,g-12)
    c: Perpendicular(g-11,g12)
    c: Coincident(g13,g11)
    c: Coincident(g13,g12)
    c: Coincident(g14,g-32)
    c: Coincident(g14,g12)
    c: Coincident(g14,g9)
    c: Coincident(g15,g-10)
    c: Coincident(g15,g11)
    c: Parallel(g16,g-22)
    c: Distance(g17) = 4
    c: PointOnObject(g17,g16)
    c: Coincident(g15,g16)
    c: Horizontal(g18)
    c: Coincident(g18,g16)
    c: Coincident(g19,g0)
    c: PointOnObject(g19,g-39)
    c: DistanceY(g19,g-36) = 2
    c: Coincident(g18,g19)
    c: Diameter(g22) = 3.6
    c: Coincident(g22,g-9)
    c: Diameter(g23) = 3.6
    c: Coincident(g23,g-8)
    c: Diameter(g24) = 3.6
    c: Diameter(g25) = 3.6
    c: Diameter(g26) = 3.6
    c: Diameter(g27) = 3.6
    c: Diameter(g28) = 3.6
    c: Coincident(g27,g-4)
    c: Coincident(g28,g-3)
    c: Coincident(g25,g-6)
    c: Coincident(g26,g-5)
    c: Coincident(g24,g-7)
    c: Parallel(g20,g-21)
    c: Equal(g20,g-21)
    c: Parallel(g21,g-19)
    c: Equal(g21,g-19)
    c: Distance(g29) = 0.2
    c: Distance(g30) = 0.2
    c: Parallel(g29,g-20)
    c: Parallel(g31,g-20)
    c: Equal(g31,g-20)
    c: Coincident(g30,g31)
    c: Coincident(g31,g29)
    c: Coincident(g29,g-21)
    c: Parallel(g30,g31)
    c: Coincident(g17,g30)
    c: Coincident(g20,g29)
    c: Coincident(g21,g30)
    c: Perpendicular(g16,g17)
    c: Coincident(g32,g21)
    c: Coincident(g32,g20)
    c: Perpendicular(g10,g7)
    c: Diameter(g33) = 12.6
    c: Diameter(g34) = 12.6
    c: Diameter(g35) = 12.6
    c: Horizontal(g36)
    c: PointOnObject(g33,g36)
    c: PointOnObject(g34,g36)
    c: DistanceX(g34,g33) = 23
    c: DistanceX(g35,g34) = 23
    c: DistanceX(g33,g36) = 15
    c: Symmetric(g-24,g-24,g36)
    c: Coincident(g36,g35)
FEATURE [Sketcher::SketchObject] Sketch075  label="lato dx pistola"
  ArcFitTolerance = 1e-06
  AttachmentSupport = -> [XZ_Plane]
  ExternalGeometry = -> [Sketch016,Sketch,Sketch058,Sketch074]
  FullyConstrained = true
  MakeInternals = false
  MapMode = 5
  Placement = pos=(0,0,0) rot=(1,0,0;1.5708rad)
  sketch-geometry (61):
    g0: LineSegment StartX=-82.8 StartY=3.2 StartZ=0 EndX=0 EndY=3.2 EndZ=0
    g1: LineSegment StartX=-82.8 StartY=3.2 StartZ=0 EndX=-82.8 EndY=6.2 EndZ=0
    g2: LineSegment [constr] StartX=-107.6 StartY=18 StartZ=0 EndX=-107.6 EndY=20 EndZ=0
    g3: LineSegment [constr] StartX=-132.428 StartY=18 StartZ=0 EndX=-132.428 EndY=20 EndZ=0
    g4: LineSegment StartX=-132.428 StartY=20 StartZ=0 EndX=-107.6 EndY=20 EndZ=0
    g5: ArcOfCircle CenterX=-107.6 CenterY=4 CenterZ=0 NormalX=0 NormalY=0 NormalZ=1 AngleXU=0 Radius=16 StartAngle=0.137937 EndAngle=1.5708
    g6: LineSegment StartX=-82.8 StartY=6.2 StartZ=0 EndX=-91.752 EndY=6.2 EndZ=0
    g7: LineSegment [constr] StartX=-145.743 StartY=8.32624 StartZ=0 EndX=-147.645 EndY=8.94427 EndZ=0
    g8: ArcOfCircle CenterX=-132.428 CenterY=4 CenterZ=0 NormalX=0 NormalY=0 NormalZ=1 AngleXU=0 Radius=16 StartAngle=1.5708 EndAngle=2.82743
    g9: LineSegment StartX=-215.932 StartY=-80.4316 StartZ=0 EndX=-176.685 EndY=-80.4316 EndZ=0
    g10: LineSegment StartX=-147.645 StartY=8.94427 StartZ=0 EndX=-176.685 EndY=-80.4316 EndZ=0
    g11: LineSegment [constr] StartX=-193.988 StartY=-2.33927 StartZ=0 EndX=-192.176 EndY=-3.18451 EndZ=0
    g12: LineSegment [constr] StartX=-217.232 StartY=-52.1862 StartZ=0 EndX=-215.42 EndY=-53.0314 EndZ=0
    g13: LineSegment StartX=-192.176 StartY=-3.18451 StartZ=0 EndX=-215.42 EndY=-53.0314 EndZ=0
    g14: ArcOfCircle CenterX=-184.801 CenterY=-67.3089 CenterZ=0 NormalX=0 NormalY=0 NormalZ=1 AngleXU=0 Radius=33.7833 StartAngle=2.70526 EndAngle=3.54053
    g15: ArcOfCircle CenterX=-207.583 CenterY=4 CenterZ=0 NormalX=0 NormalY=0 NormalZ=1 AngleXU=0 Radius=17 StartAngle=5.84685 EndAngle=7.56663
    g16: LineSegment StartX=-202.765 StartY=20.303 StartZ=0 EndX=-195.887 EndY=39.2 EndZ=0
    g17: LineSegment [constr] StartX=-193.885 StartY=33.0037 StartZ=0 EndX=-197.644 EndY=34.3718 EndZ=0
    g18: LineSegment StartX=-195.887 StartY=39.2 StartZ=0 EndX=0 EndY=39.2 EndZ=0
    g19: LineSegment StartX=0 StartY=3.2 StartZ=0 EndX=0 EndY=39.2 EndZ=0
    g20: LineSegment StartX=-189.939 StartY=31.5672 StartZ=0 EndX=-192.333 EndY=24.9893 EndZ=0
    g21: LineSegment StartX=-196.467 StartY=26.4942 StartZ=0 EndX=-194.073 EndY=33.0721 EndZ=0
    g22: Circle CenterX=-213.443 CenterY=-76.8316 CenterZ=0 NormalX=0 NormalY=0 NormalZ=1 AngleXU=0 Radius=1.8
    g23: Circle CenterX=-179.305 CenterY=-76.8316 CenterZ=0 NormalX=0 NormalY=0 NormalZ=1 AngleXU=0 Radius=1.8
    g24: Circle CenterX=-184.08 CenterY=34.8 CenterZ=0 NormalX=0 NormalY=0 NormalZ=1 AngleXU=0 Radius=1.8
    g25: Circle CenterX=-78.51 CenterY=34.8 CenterZ=0 NormalX=0 NormalY=0 NormalZ=1 AngleXU=0 Radius=1.8
    g26: Circle CenterX=-78.51 CenterY=7.6 CenterZ=0 NormalX=0 NormalY=0 NormalZ=1 AngleXU=0 Radius=1.8
    g27: Circle CenterX=-5.6 CenterY=34.8 CenterZ=0 NormalX=0 NormalY=0 NormalZ=1 AngleXU=0 Radius=1.8
    g28: Circle CenterX=-5.6 CenterY=7.6 CenterZ=0 NormalX=0 NormalY=0 NormalZ=1 AngleXU=0 Radius=1.8
    g29: LineSegment StartX=-190.127 StartY=31.6356 StartZ=0 EndX=-189.939 EndY=31.5672 EndZ=0
    g30: LineSegment StartX=-194.073 StartY=33.0721 StartZ=0 EndX=-193.885 EndY=33.0037 EndZ=0
    g31: LineSegment StartX=-193.885 StartY=33.0037 StartZ=0 EndX=-190.127 EndY=31.6356 EndZ=0
    g32: LineSegment StartX=-196.467 StartY=26.4942 StartZ=0 EndX=-192.333 EndY=24.9893 EndZ=0
    g33: LineSegment [constr] StartX=-4 StartY=21.2 StartZ=0 EndX=-87.91 EndY=21.2 EndZ=0
    g34: GeomPoint [constr] X=-4 Y=21.2 Z=0
    g35: LineSegment [constr] StartX=-15.2 StartY=33.7 StartZ=0 EndX=-15.2 EndY=8.7 EndZ=0
    g36: LineSegment [constr] StartX=-15.2 StartY=33.7 StartZ=0 EndX=-56.2 EndY=33.7 EndZ=0
    g37: LineSegment [constr] StartX=-15.2 StartY=8.7 StartZ=0 EndX=-56.2 EndY=8.7 EndZ=0
    g38: LineSegment [constr] StartX=-56.2 StartY=33.7 StartZ=0 EndX=-56.2 EndY=8.7 EndZ=0
    g39: Circle CenterX=-18.6 CenterY=30.3 CenterZ=0 NormalX=0 NormalY=0 NormalZ=1 AngleXU=0 Radius=3.4
    g40: Circle CenterX=-18.6 CenterY=12.1 CenterZ=0 NormalX=0 NormalY=0 NormalZ=1 AngleXU=0 Radius=3.4
    g41: Circle CenterX=-43.2 CenterY=30.3 CenterZ=0 NormalX=0 NormalY=0 NormalZ=1 AngleXU=0 Radius=3.4
    g42: Circle CenterX=-43.2 CenterY=12.1 CenterZ=0 NormalX=0 NormalY=0 NormalZ=1 AngleXU=0 Radius=3.4
    g43: LineSegment [constr] StartX=-4 StartY=21.2 StartZ=0 EndX=-15.2 EndY=21.2 EndZ=0
    g44: LineSegment [constr] StartX=-15.2 StartY=21.2 StartZ=0 EndX=-36.2 EndY=21.2 EndZ=0
    g45: LineSegment [constr] StartX=-41.5 StartY=16.2 StartZ=0 EndX=-30.9 EndY=16.2 EndZ=0
    g46: LineSegment [constr] StartX=-30.9 StartY=16.2 StartZ=0 EndX=-30.9 EndY=26.2 EndZ=0
    g47: LineSegment [constr] StartX=-30.9 StartY=26.2 StartZ=0 EndX=-41.5 EndY=26.2 EndZ=0
    g48: LineSegment [constr] StartX=-41.5 StartY=26.2 StartZ=0 EndX=-41.5 EndY=16.2 EndZ=0
    g49: GeomPoint [constr] X=-36.2 Y=21.2 Z=0
    g50: Circle CenterX=-36.2 CenterY=21.2 CenterZ=0 NormalX=0 NormalY=0 NormalZ=1 AngleXU=0 Radius=2.8
    g51: LineSegment [constr] StartX=-24.2 StartY=26.7 StartZ=0 EndX=-24.2 EndY=15.7 EndZ=0
    g52: Circle CenterX=-24.2 CenterY=26.7 CenterZ=0 NormalX=0 NormalY=0 NormalZ=1 AngleXU=0 Radius=3
    g53: Circle CenterX=-24.2 CenterY=15.7 CenterZ=0 NormalX=0 NormalY=0 NormalZ=1 AngleXU=0 Radius=3
    g54: GeomPoint X=-18.6 Y=30.3 Z=0
    g55: GeomPoint X=-18.6 Y=12.1 Z=0
    g56: GeomPoint X=-43.2 Y=12.1 Z=0
    g57: GeomPoint X=-43.2 Y=30.3 Z=0
    g58: Circle CenterX=-65 CenterY=21.2 CenterZ=0 NormalX=0 NormalY=0 NormalZ=1 AngleXU=0 Radius=1.5
    g59: Circle CenterX=-42 CenterY=21.2 CenterZ=0 NormalX=0 NormalY=0 NormalZ=1 AngleXU=0 Radius=1.5
    g60: Circle CenterX=-19 CenterY=21.2 CenterZ=0 NormalX=0 NormalY=0 NormalZ=1 AngleXU=0 Radius=1.5
  constraints (149):
    c: Coincident(g0,g-41)
    c: Horizontal(g0)
    c: PointOnObject(g0,g-39)
    c: Coincident(g1,g0)
    c: Vertical(g1)
    c: DistanceY(g1,g1) = 3
    c: Coincident(g2,g-17)
    c: Vertical(g2)
    c: Coincident(g3,g-16)
    c: Vertical(g3)
    c: DistanceY(g2,g2) = 2
    c: DistanceY(g3,g3) = 2
    c: Coincident(g4,g3)
    c: Coincident(g4,g2)
    c: Coincident(g5,g-17)
    c: Coincident(g5,g2)
    c: Coincident(g6,g1)
    c: Horizontal(g6)
    c: Coincident(g6,g5)
    c: Coincident(g7,g-15)
    c: Coincident(g8,g7)
    c: Coincident(g8,g3)
    c: Coincident(g8,g-15)
    c: Horizontal(g9)
    c: DistanceY(g-13,g9) = 2
    c: Coincident(g10,g7)
    c: Parallel(g10,g-14)
    c: Coincident(g9,g10)
    c: Distance(g11) = 2
    c: Coincident(g11,g-11)
    c: Perpendicular(g-11,g11)
    c: Distance(g12) = 2
    c: Coincident(g12,g-12)
    c: Perpendicular(g-11,g12)
    c: Coincident(g13,g11)
    c: Coincident(g13,g12)
    c: Coincident(g14,g-32)
    c: Coincident(g14,g12)
    c: Coincident(g14,g9)
    c: Coincident(g15,g-10)
    c: Coincident(g15,g11)
    c: Parallel(g16,g-22)
    c: Distance(g17) = 4
    c: PointOnObject(g17,g16)
    c: Coincident(g15,g16)
    c: Horizontal(g18)
    c: Coincident(g18,g16)
    c: Coincident(g19,g0)
    c: PointOnObject(g19,g-39)
    c: DistanceY(g19,g-36) = 2
    c: Coincident(g18,g19)
    c: Diameter(g22) = 3.6
    c: Coincident(g22,g-9)
    c: Diameter(g23) = 3.6
    c: Coincident(g23,g-8)
    c: Diameter(g24) = 3.6
    c: Diameter(g25) = 3.6
    c: Diameter(g26) = 3.6
    c: Diameter(g27) = 3.6
    c: Diameter(g28) = 3.6
    c: Coincident(g27,g-4)
    c: Coincident(g28,g-3)
    c: Coincident(g25,g-6)
    c: Coincident(g26,g-5)
    c: Coincident(g24,g-7)
    c: Parallel(g20,g-21)
    c: Equal(g20,g-21)
    c: Parallel(g21,g-19)
    c: Equal(g21,g-19)
    c: Distance(g29) = 0.2
    c: Distance(g30) = 0.2
    c: Parallel(g29,g-20)
    c: Parallel(g31,g-20)
    c: Equal(g31,g-20)
    c: Coincident(g30,g31)
    c: Coincident(g31,g29)
    c: Coincident(g29,g-21)
    c: Parallel(g30,g31)
    c: Coincident(g17,g30)
    c: Coincident(g20,g29)
    c: Coincident(g21,g30)
    c: Perpendicular(g16,g17)
    c: Coincident(g32,g21)
    c: Coincident(g32,g20)
    c: Perpendicular(g10,g7)
    c: Horizontal(g33)
    c: Symmetric(g-24,g-24,g33)
    c: PointOnObject(g33,g-28)
    c: Symmetric(g-24,g-24,g34)
    c: DistanceY(g35,g35) = 25
    c: Symmetric(g35,g35,g33)
    c: Distance(g36) = 41
    c: Coincident(g36,g35)
    c: Horizontal(g36)
    c: Coincident(g37,g35)
    c: Horizontal(g37)
    c: Coincident(g38,g36)
    c: Vertical(g38)
    c: Coincident(g37,g38)
    c: Diameter(g39) = 6.8
    c: Diameter(g40) = 6.8
    c: Tangent(g39,g36)
    c: Tangent(g40,g37)
    c: Tangent(g39,g35)
    c: Tangent(g40,g35)
    c: Diameter(g41) = 6.8
    c: Diameter(g42) = 6.8
    c: Tangent(g41,g36)
    c: Tangent(g42,g37)
    c: DistanceX(g41,g39) = 24.6
    c: DistanceX(g42,g40) = 24.6
    c: Distance(g43) = 11.2
    c: Coincident(g43,g33)
    c: PointOnObject(g43,g33)
    c: PointOnObject(g43,g35)
    c: Distance(g44) = 21
    c: Coincident(g44,g43)
    c: PointOnObject(g44,g33)
    c: Coincident(g45,g46)
    c: Coincident(g46,g47)
    c: Coincident(g47,g48)
    c: Coincident(g48,g45)
    c: Horizontal(g45)
    c: Horizontal(g47)
    c: Vertical(g46)
    c: Vertical(g48)
    c: Symmetric(g47,g45,g49)
    c: Distance(g46,g48) = 10.6
    c: Distance(g45,g47) = 10
    c: Coincident(g49,g44)
    c: Diameter(g50) = 5.6
    c: Coincident(g50,g44)
    c: Distance(g51) = 11
    c: Symmetric(g51,g51,g33)
    c: DistanceX(g51,g43) = 9
    c: Diameter(g52) = 6
    c: Coincident(g52,g51)
    c: Diameter(g53) = 6
    c: Coincident(g53,g51)
    c: Coincident(g40,g55)
    c: Coincident(g39,g54)
    c: Coincident(g41,g57)
    c: Coincident(g42,g56)
    c: Diameter(g58) = 3
    c: Diameter(g59) = 3
    c: Diameter(g60) = 3
    c: Coincident(g58,g-44)
    c: Coincident(g59,g-46)
    c: Coincident(g60,g-45)
FEATURE [PartDesign::Body] Body  label="Struttura pistola"
  AllowCompound = false
  Group = -> [Sketch,Sketch002,Sketch004,DatumPlane,Sketch005,DatumPlane001,CopyCut,Sketch008,Sketch009,Sketch010,Sketch011,Sketch012,Sketch013,Sketch014,Sketch015,Sketch016,Sketch017,Sketch018,Sketch019,Sketch020,Sketch022,Sketch023,Sketch024,Sketch025,Sketch026,Sketch027,Sketch029,Sketch030,Sketch031,Sketch032,Sketch033,Sketch034,Sketch035,Sketch036,Sketch037,Sketch038,Sketch039,Sketch040,Sketch041,Sketch042,+15 more]
  Origin = -> Origin
FEATURE [Sketcher::SketchObject] Sketch078
  ArcFitTolerance = 1e-06
  AttachmentSupport = -> [XZ_Plane005]
  FullyConstrained = true
  MakeInternals = false
  MapMode = 5
  Placement = pos=(0,0,0) rot=(1,0,0;1.5708rad)
  sketch-geometry (5):
    g0: LineSegment [constr] StartX=0 StartY=5.5 StartZ=0 EndX=0 EndY=-5.5 EndZ=0
    g1: ArcOfCircle CenterX=0 CenterY=5.5 CenterZ=0 NormalX=0 NormalY=0 NormalZ=1 AngleXU=0 Radius=2.7 StartAngle=0 EndAngle=3.14159
    g2: ArcOfCircle CenterX=0 CenterY=-5.5 CenterZ=0 NormalX=0 NormalY=0 NormalZ=1 AngleXU=0 Radius=2.7 StartAngle=3.1416 EndAngle=6.28318
    g3: LineSegment StartX=-2.7 StartY=5.5 StartZ=0 EndX=-2.7 EndY=-5.50001 EndZ=0
    g4: LineSegment StartX=2.7 StartY=5.5 StartZ=0 EndX=2.7 EndY=-5.50001 EndZ=0
  constraints (13):
    c: Distance(g0) = 11
    c: Vertical(g0)
    c: Symmetric(g0,g0,g-1)
    c: Radius(g1) = 2.7
    c: Coincident(g1,g0)
    c: Radius(g2) = 2.7
    c: Coincident(g2,g0)
    c: Vertical(g3)
    c: Vertical(g4)
    c: Coincident(g2,g4)
    c: Coincident(g2,g3)
    c: Tangent(g3,g1) = -1.5708
    c: Tangent(g4,g1) = 1.5708
FEATURE [PartDesign::Pad] Pad002
  Direction = (0,-1,2e-16)
  Length = 0.8
  Length2 = 10
  Placement = pos=(0,0,0) rot=(1,0,0;1.5708rad)
  Profile = -> Sketch078
  ReferenceAxis = -> Sketch078 [N_Axis]
  Refine = true
  Suppressed = false
  Type = 0
FEATURE [Sketcher::SketchObject] Sketch079
  ArcFitTolerance = 1e-06
  AttachmentSupport = -> [XZ_Plane005]
  ExternalGeometry = -> [Sketch078]
  FullyConstrained = true
  MakeInternals = false
  MapMode = 5
  Placement = pos=(0,0,0) rot=(1,0,0;1.5708rad)
  sketch-geometry (2):
    g0: Circle CenterX=-1e-16 CenterY=5.5 CenterZ=0 NormalX=0 NormalY=0 NormalZ=1 AngleXU=0 Radius=2.7
    g1: Circle CenterX=0 CenterY=-5.5 CenterZ=0 NormalX=0 NormalY=0 NormalZ=1 AngleXU=0 Radius=2.7
  constraints (4):
    c: Coincident(g0,g-3)
    c: PointOnObject(g-3,g0)
    c: Coincident(g1,g-4)
    c: Equal(g1,g-4)
FEATURE [PartDesign::Pad] Pad003
  BaseFeature = -> Pad002
  Direction = (0,-1,2e-16)
  Length = 5
  Length2 = 10
  Placement = pos=(0,0,0) rot=(1,0,0;1.5708rad)
  Profile = -> Sketch079
  ReferenceAxis = -> Sketch079 [N_Axis]
  Refine = true
  Suppressed = false
  Type = 0
FEATURE [PartDesign::Fillet] Fillet001
  Base = -> Pad003 [Edge16,Edge14]
  BaseFeature = -> Pad003
  Placement = pos=(0,0,0) rot=(1,0,0;1.5708rad)
  Radius = 0.4
  Refine = true
  SupportTransform = false
  Suppressed = false
  UseAllEdges = false
FEATURE [PartDesign::Body] Body005  label="pulsanti lato destro"
  AllowCompound = false
  Group = -> [Sketch078,Pad002,Sketch079,Pad003,Fillet001]
  Origin = -> Origin005
  Tip = -> Fillet001
FEATURE [PartDesign::SubShapeBinder] Binder
  BindCopyOnChange = 0
  BindMode = 0
  ClaimChildren = false
  Context = -> Body006 [Binder.]
  Fuse = false
  MakeFace = true
  OffsetFill = false
  OffsetIntersection = false
  OffsetJoinType = 0
  OffsetOpenResult = false
  PartialLoad = false
  Refine = true
  Relative = true
  Support = -> [Body[Sketch074.]]
  _Version = 2
FEATURE [PartDesign::SubShapeBinder] Binder001
  BindCopyOnChange = 0
  BindMode = 0
  ClaimChildren = false
  Context = -> Body007 [Binder001.]
  Fuse = false
  MakeFace = true
  OffsetFill = false
  OffsetIntersection = false
  OffsetJoinType = 0
  OffsetOpenResult = false
  PartialLoad = false
  Refine = true
  Relative = true
  Support = -> [Body[Sketch075.]]
  _Version = 2
FEATURE [Mesh::Feature] logo_per_PCB_definitivo_positivo
  Placement = pos=(-191,17,-66) rot=(0,1,1;0rad)
FEATURE [Sketcher::SketchObject] Sketch114  label="Sketch114 - base lato DX"
  ArcFitTolerance = 1e-06
  AttachmentSupport = -> [Binder001]
  ExternalGeometry = -> [Binder001]
  FullyConstrained = true
  MakeInternals = false
  MapMode = 5
  Placement = pos=(0,1e-15,0) rot=(0,0.707107,0.707107;3.14159rad)
  sketch-geometry (30):
    g0: Circle CenterX=5.6 CenterY=34.8 CenterZ=0 NormalX=0 NormalY=0 NormalZ=1 AngleXU=0 Radius=1.8
    g1: Circle CenterX=5.6 CenterY=7.6 CenterZ=0 NormalX=0 NormalY=0 NormalZ=1 AngleXU=0 Radius=1.8
    g2: Circle CenterX=24.2 CenterY=26.7 CenterZ=0 NormalX=0 NormalY=0 NormalZ=1 AngleXU=0 Radius=3
    g3: Circle CenterX=24.2 CenterY=15.7 CenterZ=0 NormalX=0 NormalY=0 NormalZ=1 AngleXU=0 Radius=3
    g4: Circle CenterX=36.2 CenterY=21.2 CenterZ=0 NormalX=0 NormalY=0 NormalZ=1 AngleXU=0 Radius=2.8
    g5: Circle CenterX=78.51 CenterY=34.8 CenterZ=0 NormalX=0 NormalY=0 NormalZ=1 AngleXU=0 Radius=1.8
    g6: Circle CenterX=78.51 CenterY=7.6 CenterZ=0 NormalX=0 NormalY=0 NormalZ=1 AngleXU=0 Radius=1.8
    g7: Circle CenterX=184.08 CenterY=34.8 CenterZ=0 NormalX=0 NormalY=0 NormalZ=1 AngleXU=0 Radius=1.8
    g8: Circle CenterX=213.443 CenterY=-76.8316 CenterZ=0 NormalX=0 NormalY=0 NormalZ=1 AngleXU=0 Radius=1.8
    g9: Circle CenterX=179.305 CenterY=-76.8316 CenterZ=0 NormalX=0 NormalY=0 NormalZ=1 AngleXU=0 Radius=1.8
    g10: ArcOfCircle [constr] CenterX=132.428 CenterY=4 CenterZ=0 NormalX=0 NormalY=0 NormalZ=1 AngleXU=0 Radius=16 StartAngle=0.314159 EndAngle=1.5708
    g11: ArcOfCircle CenterX=107.6 CenterY=4 CenterZ=0 NormalX=0 NormalY=0 NormalZ=1 AngleXU=0 Radius=16 StartAngle=1.5708 EndAngle=3.00366
    g12: ArcOfCircle CenterX=207.583 CenterY=4 CenterZ=0 NormalX=0 NormalY=0 NormalZ=1 AngleXU=0 Radius=17 StartAngle=1.85815 EndAngle=3.57792
    g13: ArcOfCircle CenterX=184.801 CenterY=-67.3089 CenterZ=0 NormalX=0 NormalY=0 NormalZ=1 AngleXU=0 Radius=33.7833 StartAngle=5.88425 EndAngle=6.71952
    g14: LineSegment StartX=0 StartY=39.2 StartZ=0 EndX=0 EndY=3.2 EndZ=0
    g15: LineSegment StartX=0 StartY=3.2 StartZ=0 EndX=82.8 EndY=3.2 EndZ=0
    g16: LineSegment StartX=82.8 StartY=3.2 StartZ=0 EndX=82.8 EndY=6.2 EndZ=0
    g17: LineSegment StartX=82.8 StartY=6.2 StartZ=0 EndX=91.752 EndY=6.2 EndZ=0
    g18: LineSegment StartX=107.6 StartY=20 StartZ=0 EndX=132.428 EndY=20 EndZ=0
    g19: LineSegment StartX=147.645 StartY=8.94427 StartZ=0 EndX=176.685 EndY=-80.4316 EndZ=0
    g20: LineSegment StartX=176.685 StartY=-80.4316 StartZ=0 EndX=215.932 EndY=-80.4316 EndZ=0
    g21: LineSegment StartX=215.42 StartY=-53.0314 StartZ=0 EndX=192.176 EndY=-3.18451 EndZ=0
    g22: LineSegment StartX=202.765 StartY=20.303 StartZ=0 EndX=195.887 EndY=39.2 EndZ=0
    g23: LineSegment StartX=195.887 StartY=39.2 StartZ=0 EndX=0 EndY=39.2 EndZ=0
    g24: LineSegment StartX=196.467 StartY=26.4942 StartZ=0 EndX=194.073 EndY=33.0721 EndZ=0
    g25: LineSegment StartX=194.073 StartY=33.0721 StartZ=0 EndX=189.939 EndY=31.5672 EndZ=0
    g26: LineSegment StartX=189.939 StartY=31.5672 StartZ=0 EndX=192.333 EndY=24.9893 EndZ=0
    g27: LineSegment StartX=192.333 StartY=24.9893 StartZ=0 EndX=196.467 EndY=26.4942 EndZ=0
    g28: LineSegment StartX=132.428 StartY=20 StartZ=0 EndX=144.053 EndY=20 EndZ=0
    g29: LineSegment StartX=144.053 StartY=20 StartZ=0 EndX=147.645 EndY=8.94427 EndZ=0
  constraints (65):
    c: Equal(g0,g-25)
    c: Equal(g2,g-29)
    c: Equal(g3,g-30)
    c: Equal(g4,g-28)
    c: Equal(g1,g-26)
    c: Coincident(g0,g-25)
    c: Coincident(g1,g-26)
    c: Coincident(g2,g-29)
    c: Coincident(g3,g-30)
    c: Coincident(g4,g-28)
    c: Equal(g5,g-23)
    c: Equal(g6,g-24)
    c: Coincident(g5,g-23)
    c: Coincident(g6,g-24)
    c: Equal(g7,g-20)
    c: Coincident(g7,g-20)
    c: Equal(g9,g-22)
    c: Coincident(g9,g-22)
    c: Equal(g8,g-21)
    c: Coincident(g8,g-21)
    c: Equal(g13,g-12)
    c: Equal(g12,g-14)
    c: Equal(g10,g-9)
    c: Equal(g11,g-7)
    c: Coincident(g14,g-27)
    c: Coincident(g14,g-27)
    c: Coincident(g15,g14)
    c: Coincident(g15,g-5)
    c: Coincident(g16,g15)
    c: Coincident(g16,g-6)
    c: Coincident(g17,g16)
    c: Coincident(g17,g-7)
    c: Coincident(g11,g17)
    c: Coincident(g11,g-8)
    c: Coincident(g18,g11)
    c: Coincident(g18,g-9)
    c: Coincident(g10,g18)
    c: Coincident(g10,g-10)
    c: Coincident(g19,g10)
    c: Coincident(g19,g-11)
    c: Coincident(g20,g19)
    c: Coincident(g20,g-12)
    c: Coincident(g13,g20)
    c: Coincident(g13,g-13)
    c: Coincident(g21,g13)
    c: Coincident(g21,g-14)
    c: Coincident(g12,g21)
    c: Coincident(g12,g-15)
    c: Coincident(g22,g12)
    c: Coincident(g22,g-15)
    c: Coincident(g23,g22)
    c: Coincident(g23,g14)
    c: Coincident(g24,g-18)
    c: Coincident(g24,g-16)
    c: Coincident(g25,g24)
    c: Coincident(g25,g-19)
    c: Coincident(g26,g25)
    c: Coincident(g26,g-19)
    c: Coincident(g27,g26)
    c: Coincident(g27,g24)
    c: Coincident(g29,g10)
    c: Coincident(g28,g10)
    c: Coincident(g29,g28)
    c: Parallel(g28,g18)
    c: Parallel(g29,g19)
FEATURE [PartDesign::Pad] Pad011
  Direction = (0,1,-2e-16)
  Length = 2
  Length2 = 10
  Profile = -> Sketch114
  ReferenceAxis = -> Sketch114 [N_Axis]
  Refine = true
  Reversed = true
  Suppressed = false
  Type = 0
FEATURE [Sketcher::SketchObject] Sketch115
  ArcFitTolerance = 1e-06
  AttachmentSupport = -> [Pad011]
  ExternalGeometry = -> [Binder001]
  FullyConstrained = true
  MakeInternals = false
  MapMode = 5
  Placement = pos=(0,1.7e-15,0) rot=(0,0.707107,0.707107;3.14159rad)
  sketch-geometry (4):
    g0: ArcOfCircle CenterX=24.2 CenterY=26.7 CenterZ=0 NormalX=0 NormalY=0 NormalZ=1 AngleXU=0 Radius=3 StartAngle=4.48384e-08 EndAngle=3.14159
    g1: ArcOfCircle CenterX=24.2 CenterY=15.7 CenterZ=0 NormalX=0 NormalY=0 NormalZ=1 AngleXU=0 Radius=3 StartAngle=3.14159 EndAngle=6.28318
    g2: LineSegment StartX=21.2 StartY=26.7 StartZ=0 EndX=21.2 EndY=15.7 EndZ=0
    g3: LineSegment StartX=27.2 StartY=26.7 StartZ=0 EndX=27.2 EndY=15.7 EndZ=0
  constraints (12):
    c: Equal(g1,g-4)
    c: Equal(g0,g-3)
    c: Coincident(g0,g-3)
    c: Coincident(g1,g-4)
    c: Vertical(g2)
    c: Vertical(g3)
    c: Tangent(g3,g-3)
    c: Tangent(g2,g-3)
    c: Coincident(g0,g2)
    c: Coincident(g0,g3)
    c: Coincident(g1,g2)
    c: Coincident(g3,g1)
FEATURE [Sketcher::SketchObject] Sketch117  label="Sketch117 - fori per inserto M3 x 3 x 4.5"
  ArcFitTolerance = 1e-06
  AttachmentSupport = -> [Pad011]
  ExternalGeometry = -> [Binder001]
  FullyConstrained = true
  MakeInternals = false
  MapMode = 5
  Placement = pos=(0,1.7e-15,0) rot=(0,0.707107,0.707107;3.14159rad)
  sketch-geometry (4):
    g0: Circle CenterX=43.2 CenterY=30.3 CenterZ=0 NormalX=0 NormalY=0 NormalZ=1 AngleXU=0 Radius=2.25
    g1: Circle CenterX=43.2 CenterY=12.1 CenterZ=0 NormalX=0 NormalY=0 NormalZ=1 AngleXU=0 Radius=2.25
    g2: Circle CenterX=18.6 CenterY=30.3 CenterZ=0 NormalX=0 NormalY=0 NormalZ=1 AngleXU=0 Radius=2.25
    g3: Circle CenterX=18.6 CenterY=12.1 CenterZ=0 NormalX=0 NormalY=0 NormalZ=1 AngleXU=0 Radius=2.25
  constraints (8):
    c: Diameter(g0) = 4.5
    c: Diameter(g1) = 4.5
    c: Diameter(g2) = 4.5
    c: Diameter(g3) = 4.5
    c: Coincident(g2,g-3)
    c: Coincident(g3,g-6)
    c: Coincident(g0,g-4)
    c: Coincident(g1,g-5)
FEATURE [Sketcher::SketchObject] Sketch118
  ArcFitTolerance = 1e-06
  AttachmentSupport = -> [Pad011]
  ExternalGeometry = -> [Binder001]
  FullyConstrained = true
  MakeInternals = false
  MapMode = 5
  Placement = pos=(0,-2,0) rot=(1,0,0;1.5708rad)
  sketch-geometry (12):
    g0: Circle CenterX=-78.51 CenterY=34.8 CenterZ=0 NormalX=0 NormalY=0 NormalZ=1 AngleXU=0 Radius=1.8
    g1: Circle CenterX=-78.51 CenterY=7.6 CenterZ=0 NormalX=0 NormalY=0 NormalZ=1 AngleXU=0 Radius=1.8
    g2: Circle CenterX=-5.6 CenterY=34.8 CenterZ=0 NormalX=0 NormalY=0 NormalZ=1 AngleXU=0 Radius=1.8
    g3: Circle CenterX=-5.6 CenterY=7.6 CenterZ=0 NormalX=0 NormalY=0 NormalZ=1 AngleXU=0 Radius=1.8
    g4: LineSegment StartX=0 StartY=39.2 StartZ=0 EndX=0 EndY=3.2 EndZ=0
    g5: LineSegment StartX=0 StartY=3.2 StartZ=0 EndX=-82.8 EndY=3.2 EndZ=0
    g6: LineSegment StartX=-82.8 StartY=3.2 StartZ=0 EndX=-82.8 EndY=39.2 EndZ=0
    g7: LineSegment StartX=-82.8 StartY=39.2 StartZ=0 EndX=0 EndY=39.2 EndZ=0
    g8: ArcOfCircle CenterX=-65 CenterY=21.2 CenterZ=0 NormalX=0 NormalY=0 NormalZ=1 AngleXU=0 Radius=10 StartAngle=1.5708 EndAngle=4.71239
    g9: ArcOfCircle CenterX=-19 CenterY=21.2 CenterZ=0 NormalX=0 NormalY=0 NormalZ=1 AngleXU=0 Radius=10 StartAngle=4.71239 EndAngle=7.85398
    g10: LineSegment StartX=-65 StartY=31.2 StartZ=0 EndX=-19 EndY=31.2 EndZ=0
    g11: LineSegment StartX=-65 StartY=11.2 StartZ=0 EndX=-19 EndY=11.2 EndZ=0
  constraints (25):
    c: Equal(g2,g-5)
    c: Equal(g3,g-7)
    c: Equal(g1,g-6)
    c: Equal(g0,g-4)
    c: Coincident(g0,g-4)
    c: Coincident(g1,g-6)
    c: Coincident(g3,g-7)
    c: Coincident(g2,g-5)
    c: Coincident(g4,g-8)
    c: Coincident(g4,g-9)
    c: Coincident(g5,g4)
    c: Coincident(g5,g-10)
    c: Coincident(g6,g5)
    c: PointOnObject(g6,g-3)
    c: Vertical(g6)
    c: Coincident(g7,g6)
    c: Coincident(g7,g4)
    c: Tangent(g8,g10) = 1.5708
    c: Tangent(g8,g11) = -1.5708
    c: Tangent(g9,g10) = 1.5708
    c: Tangent(g9,g11) = -1.5708
    c: Equal(g8,g9)
    c: Radius(g8) = 10
    c: Coincident(g8,g-11)
    c: Coincident(g9,g-12)
FEATURE [Sketcher::SketchObject] Sketch120
  ArcFitTolerance = 1e-06
  AttachmentSupport = -> [Pad011]
  ExternalGeometry = -> [Binder001]
  FullyConstrained = true
  MakeInternals = false
  MapMode = 5
  Placement = pos=(0,-2,0) rot=(1,0,0;1.5708rad)
  sketch-geometry (4):
    g0: LineSegment StartX=-137.815 StartY=39.2 StartZ=0 EndX=-142.655 EndY=24.303 EndZ=0
    g1: LineSegment StartX=-137.815 StartY=39.2 StartZ=0 EndX=-110.815 EndY=39.2 EndZ=0
    g2: LineSegment StartX=-142.655 StartY=24.303 StartZ=0 EndX=-110.815 EndY=24.303 EndZ=0
    g3: ArcOfCircle CenterX=-92.2534 CenterY=31.7515 CenterZ=0 NormalX=0 NormalY=0 NormalZ=1 AngleXU=0 Radius=20 StartAngle=2.75997 EndAngle=3.52321
  constraints (12):
    c: PointOnObject(g0,g-3)
    c: Coincident(g1,g0)
    c: PointOnObject(g1,g-3)
    c: Coincident(g2,g0)
    c: Horizontal(g2)
    c: Tangent(g0,g-4)
    c: Vertical(g2,g1)
    c: DistanceX(g1,g1) = 27
    c: DistanceY(g-6,g0) = 4
    c: Radius(g3) = 20
    c: Coincident(g3,g1)
    c: Coincident(g3,g2)
FEATURE [Sketcher::SketchObject] Sketch121
  ArcFitTolerance = 1e-06
  AttachmentSupport = -> [Pad011]
  ExternalGeometry = -> [Binder001]
  FullyConstrained = true
  MakeInternals = false
  MapMode = 5
  Placement = pos=(0,-2,0) rot=(1,0,0;1.5708rad)
  sketch-geometry (15):
    g0: LineSegment StartX=-137.815 StartY=39.2 StartZ=0 EndX=-143.955 EndY=20.303 EndZ=0
    g1: LineSegment StartX=-143.955 StartY=20.303 StartZ=0 EndX=-190.141 EndY=20.303 EndZ=0
    g2: LineSegment StartX=-190.141 StartY=20.303 StartZ=0 EndX=-186.139 EndY=31.3 EndZ=0
    g3: LineSegment StartX=-178.754 StartY=39.2 StartZ=0 EndX=-180.791 EndY=33.6029 EndZ=0
    g4: ArcOfCircle CenterX=-184.08 CenterY=34.8 CenterZ=0 NormalX=0 NormalY=0 NormalZ=1 AngleXU=0 Radius=3.5 StartAngle=4.71239 EndAngle=5.93412
    g5: LineSegment StartX=-184.08 StartY=31.3 StartZ=0 EndX=-186.139 EndY=31.3 EndZ=0
    g6: LineSegment StartX=-137.815 StartY=39.2 StartZ=0 EndX=-156.815 EndY=39.2 EndZ=0
    g7: LineSegment StartX=-168.815 StartY=39.2 StartZ=0 EndX=-178.754 EndY=39.2 EndZ=0
    g8: LineSegment StartX=-157.815 StartY=39.2 StartZ=0 EndX=-167.815 EndY=39.2 EndZ=0
    g9: LineSegment StartX=-168.815 StartY=31.2 StartZ=0 EndX=-156.815 EndY=31.2 EndZ=0
    g10: LineSegment StartX=-167.436 StartY=36.2 StartZ=0 EndX=-157.436 EndY=36.2 EndZ=0
    g11: ArcOfCircle CenterX=-176.411 CenterY=35.2 CenterZ=0 NormalX=0 NormalY=0 NormalZ=1 AngleXU=0 Radius=20 StartAngle=6.08183 EndAngle=6.48454
    g12: ArcOfCircle CenterX=-188.411 CenterY=35.2 CenterZ=0 NormalX=0 NormalY=0 NormalZ=1 AngleXU=0 Radius=20 StartAngle=6.08183 EndAngle=6.48454
    g13: ArcOfCircle CenterX=-177.411 CenterY=35.2 CenterZ=0 NormalX=0 NormalY=0 NormalZ=1 AngleXU=0 Radius=20 StartAngle=0.0500209 EndAngle=0.201358
    g14: ArcOfCircle CenterX=-187.411 CenterY=35.2 CenterZ=0 NormalX=0 NormalY=0 NormalZ=1 AngleXU=0 Radius=20 StartAngle=0.0500209 EndAngle=0.201358
  constraints (46):
    c: PointOnObject(g0,g-3)
    c: Tangent(g0,g-5)
    c: Coincident(g1,g0)
    c: Horizontal(g1)
    c: Coincident(g2,g1)
    c: PointOnObject(g3,g-3)
    c: Parallel(g3,g-6)
    c: Parallel(g2,g-6)
    c: Radius(g4) = 3.5
    c: Coincident(g4,g-7)
    c: Tangent(g3,g4) = 1.5708
    c: Horizontal(g5)
    c: Tangent(g5,g4) = 1.5708
    c: DistanceX(g-8,g5) = 3.8
    c: Coincident(g2,g5)
    c: Coincident(g6,g0)
    c: PointOnObject(g6,g-3)
    c: DistanceX(g6,g6) = 19
    c: PointOnObject(g7,g-3)
    c: DistanceX(g7,g6) = 12
    c: Coincident(g7,g3)
    c: PointOnObject(g8,g-3)
    c: PointOnObject(g8,g-3)
    c: DistanceX(g8,g8) = 10
    c: DistanceX(g8,g6) = 1
    c: Horizontal(g9)
    c: Vertical(g7,g9)
    c: Vertical(g6,g9)
    c: DistanceY(g9,g7) = 8
    c: Horizontal(g10)
    c: Equal(g8,g10)
    c: DistanceY(g10,g8) = 3
    c: Radius(g11) = 20
    c: Coincident(g11,g6)
    c: Coincident(g11,g9)
    c: Radius(g12) = 20
    c: Coincident(g12,g7)
    c: Coincident(g12,g9)
    c: Equal(g13,g11)
    c: Coincident(g13,g8)
    c: Coincident(g13,g10)
    c: Horizontal(g13,g11)
    c: Equal(g14,g12)
    c: Coincident(g14,g8)
    c: Coincident(g14,g10)
    c: Horizontal(g1,g-6)
FEATURE [Sketcher::SketchObject] Sketch122
  ArcFitTolerance = 1e-06
  AttachmentSupport = -> [Pad011]
  ExternalGeometry = -> [Binder001]
  FullyConstrained = true
  MakeInternals = false
  MapMode = 5
  Placement = pos=(0,-2,0) rot=(1,0,0;1.5708rad)
  sketch-geometry (8):
    g0: LineSegment StartX=-202.765 StartY=20.303 StartZ=0 EndX=-143.955 EndY=20.303 EndZ=0
    g1: ArcOfCircle CenterX=-184.801 CenterY=-67.3089 CenterZ=0 NormalX=0 NormalY=0 NormalZ=1 AngleXU=0 Radius=33.7833 StartAngle=2.70526 EndAngle=3.54053
    g2: LineSegment StartX=-176.685 StartY=-80.4316 StartZ=0 EndX=-215.932 EndY=-80.4316 EndZ=0
    g3: LineSegment StartX=-215.42 StartY=-53.0315 StartZ=0 EndX=-192.176 EndY=-3.18454 EndZ=0
    g4: ArcOfCircle CenterX=-207.583 CenterY=4 CenterZ=0 NormalX=0 NormalY=0 NormalZ=1 AngleXU=0 Radius=17 StartAngle=5.84685 EndAngle=7.56663
    g5: Circle CenterX=-213.443 CenterY=-76.8316 CenterZ=0 NormalX=0 NormalY=0 NormalZ=1 AngleXU=0 Radius=3
    g6: Circle CenterX=-179.305 CenterY=-76.8316 CenterZ=0 NormalX=0 NormalY=0 NormalZ=1 AngleXU=0 Radius=3
    g7: LineSegment StartX=-143.955 StartY=20.303 StartZ=0 EndX=-176.685 EndY=-80.4316 EndZ=0
  constraints (18):
    c: Coincident(g0,g-6)
    c: Coincident(g1,g-7)
    c: Coincident(g1,g-8)
    c: Coincident(g2,g1)
    c: Tangent(g3,g-5)
    c: Coincident(g4,g-6)
    c: Coincident(g4,g0)
    c: Coincident(g3,g4)
    c: Coincident(g1,g3)
    c: Diameter(g5) = 6
    c: Diameter(g6) = 6
    c: Coincident(g5,g-9)
    c: Coincident(g6,g-10)
    c: Horizontal(g0)
    c: Horizontal(g2)
    c: Coincident(g7,g0)
    c: Coincident(g7,g2)
    c: Tangent(g7,g-4)
FEATURE [Sketcher::SketchObject] Sketch123
  ArcFitTolerance = 1e-06
  AttachmentSupport = -> [Pad011]
  ExternalGeometry = -> [Binder001]
  FullyConstrained = true
  MakeInternals = false
  MapMode = 5
  Placement = pos=(0,-2,0) rot=(1,0,0;1.5708rad)
  sketch-geometry (4):
    g0: LineSegment StartX=-108 StartY=36.8 StartZ=0 EndX=-90 EndY=36.8 EndZ=0
    g1: LineSegment StartX=-108 StartY=36.8 StartZ=0 EndX=-108 EndY=26.8 EndZ=0
    g2: LineSegment StartX=-108 StartY=26.8 StartZ=0 EndX=-90 EndY=26.8 EndZ=0
    g3: ArcOfCircle CenterX=-94 CenterY=31.8 CenterZ=0 NormalX=0 NormalY=0 NormalZ=1 AngleXU=0 Radius=6.40312 StartAngle=5.38713 EndAngle=7.17924
  constraints (13):
    c: Horizontal(g0)
    c: Coincident(g1,g0)
    c: Vertical(g1)
    c: Coincident(g2,g1)
    c: Horizontal(g2)
    c: DistanceX(g0,g0) = 18
    c: DistanceY(g1,g1) = 10
    c: Equal(g0,g2)
    c: DistanceX(g0,g-3) = 90
    c: DistanceY(g0,g-3) = 2.4
    c: Coincident(g3,g0)
    c: Coincident(g3,g2)
    c: DistanceX(g3,g0) = 4
FEATURE [PartDesign::Chamfer] Chamfer014
  Angle = 45
  Base = -> Pad011 [Edge80,Edge4,Edge7]
  BaseFeature = -> Pad011
  ChamferType = 0
  FlipDirection = false
  Refine = true
  Size = 1.9
  Size2 = 1
  SupportTransform = false
  Suppressed = false
  UseAllEdges = false
FEATURE [PartDesign::Pocket] Pocket006
  BaseFeature = -> Chamfer014
  Direction = (0,-1,2e-16)
  Length = 1.2
  Length2 = 5
  Profile = -> Sketch115
  ReferenceAxis = -> Sketch115 [N_Axis]
  Refine = true
  Suppressed = false
  Type = 0
FEATURE [Sketcher::SketchObject] Sketch116  label="Sketch116 - pieno per inserto M3 x 3 x 4,5"
  ArcFitTolerance = 1e-06
  AttachmentSupport = -> [Pocket006]
  ExternalGeometry = -> [Binder001]
  FullyConstrained = true
  MakeInternals = false
  MapMode = 5
  Placement = pos=(0,1.7e-15,0) rot=(0,0.707107,0.707107;3.14159rad)
  sketch-geometry (4):
    g0: Circle CenterX=43.2 CenterY=30.3 CenterZ=0 NormalX=0 NormalY=0 NormalZ=1 AngleXU=0 Radius=3.4
    g1: Circle CenterX=43.2 CenterY=12.1 CenterZ=0 NormalX=0 NormalY=0 NormalZ=1 AngleXU=0 Radius=3.4
    g2: Circle CenterX=18.6 CenterY=30.3 CenterZ=0 NormalX=0 NormalY=0 NormalZ=1 AngleXU=0 Radius=3.4
    g3: Circle CenterX=18.6 CenterY=12.1 CenterZ=0 NormalX=0 NormalY=0 NormalZ=1 AngleXU=0 Radius=3.4
  constraints (8):
    c: Diameter(g0) = 6.8
    c: Diameter(g1) = 6.8
    c: Diameter(g2) = 6.8
    c: Diameter(g3) = 6.8
    c: Coincident(g2,g-3)
    c: Coincident(g0,g-4)
    c: Coincident(g3,g-6)
    c: Coincident(g1,g-5)
FEATURE [PartDesign::Pad] Pad012
  BaseFeature = -> Pocket006
  Direction = (0,1,-2e-16)
  Length = 2.4
  Length2 = 10
  Profile = -> Sketch116
  ReferenceAxis = -> Sketch116 [N_Axis]
  Refine = true
  Suppressed = false
  Type = 0
FEATURE [PartDesign::Pocket] Pocket007
  BaseFeature = -> Pad012
  Direction = (0,-1,2e-16)
  Length = 0.6
  Length2 = 2.4
  Profile = -> Sketch117
  ReferenceAxis = -> Sketch117 [N_Axis]
  Refine = true
  Suppressed = false
  Type = 4
FEATURE [PartDesign::Pad] Pad013
  BaseFeature = -> Pocket007
  Direction = (0,-1,2e-16)
  Length = 1.6
  Length2 = 10
  Profile = -> Sketch118
  ReferenceAxis = -> Sketch118 [N_Axis]
  Refine = true
  Suppressed = false
  Type = 0
FEATURE [Sketcher::SketchObject] Sketch119
  ArcFitTolerance = 1e-06
  AttachmentSupport = -> [Pad013]
  ExternalGeometry = -> [Binder001]
  FullyConstrained = true
  MakeInternals = false
  MapMode = 5
  Placement = pos=(0,-3.6,0) rot=(1,0,0;1.5708rad)
  sketch-geometry (21):
    g0: LineSegment [constr] StartX=-82.8 StartY=3.2 StartZ=0 EndX=-82.8 EndY=39.2 EndZ=0
    g1: ArcOfCircle CenterX=-78.51 CenterY=34.8 CenterZ=0 NormalX=0 NormalY=0 NormalZ=1 AngleXU=0 Radius=3.5 StartAngle=4.71239 EndAngle=6.28319
    g2: ArcOfCircle CenterX=-78.51 CenterY=7.6 CenterZ=0 NormalX=0 NormalY=0 NormalZ=1 AngleXU=0 Radius=3.5 StartAngle=0 EndAngle=1.5708
    g3: ArcOfCircle CenterX=-5.6 CenterY=34.8 CenterZ=0 NormalX=0 NormalY=0 NormalZ=1 AngleXU=0 Radius=3.5 StartAngle=3.14159 EndAngle=4.71239
    g4: ArcOfCircle CenterX=-5.6 CenterY=7.6 CenterZ=0 NormalX=0 NormalY=0 NormalZ=1 AngleXU=0 Radius=3.5 StartAngle=1.5708 EndAngle=3.14159
    g5: LineSegment StartX=0 StartY=39.2 StartZ=0 EndX=0 EndY=31.3 EndZ=0
    g6: LineSegment StartX=0 StartY=39.2 StartZ=0 EndX=-9.1 EndY=39.2 EndZ=0
    g7: LineSegment StartX=0 StartY=3.2 StartZ=0 EndX=0 EndY=11.1 EndZ=0
    g8: LineSegment StartX=0 StartY=3.2 StartZ=0 EndX=-9.1 EndY=3.2 EndZ=0
    g9: LineSegment StartX=-82.8 StartY=3.2 StartZ=0 EndX=-75.01 EndY=3.2 EndZ=0
    g10: LineSegment StartX=-82.8 StartY=3.2 StartZ=0 EndX=-82.8 EndY=11.1 EndZ=0
    g11: LineSegment StartX=-82.8 StartY=39.2 StartZ=0 EndX=-82.8 EndY=31.3 EndZ=0
    g12: LineSegment StartX=-82.8 StartY=39.2 StartZ=0 EndX=-75.01 EndY=39.2 EndZ=0
    g13: LineSegment StartX=-82.8 StartY=31.3 StartZ=0 EndX=-78.51 EndY=31.3 EndZ=0
    g14: LineSegment StartX=-75.01 StartY=39.2 StartZ=0 EndX=-75.01 EndY=34.8 EndZ=0
    g15: LineSegment StartX=-82.8 StartY=11.1 StartZ=0 EndX=-78.51 EndY=11.1 EndZ=0
    g16: LineSegment StartX=-75.01 StartY=3.2 StartZ=0 EndX=-75.01 EndY=7.6 EndZ=0
    g17: LineSegment StartX=-9.1 StartY=39.2 StartZ=0 EndX=-9.1 EndY=34.8 EndZ=0
    g18: LineSegment StartX=0 StartY=31.3 StartZ=0 EndX=-5.6 EndY=31.3 EndZ=0
    g19: LineSegment StartX=0 StartY=11.1 StartZ=0 EndX=-5.6 EndY=11.1 EndZ=0
    g20: LineSegment StartX=-9.1 StartY=3.2 StartZ=0 EndX=-9.1 EndY=7.6 EndZ=0
  constraints (51):
    c: Coincident(g0,g-10)
    c: PointOnObject(g0,g-8)
    c: Vertical(g0)
    c: Coincident(g1,g-3)
    c: Coincident(g2,g-4)
    c: Coincident(g3,g-5)
    c: Coincident(g4,g-6)
    c: Radius(g4) = 3.5
    c: Radius(g3) = 3.5
    c: Radius(g1) = 3.5
    c: Radius(g2) = 3.5
    c: Coincident(g5,g-9)
    c: PointOnObject(g5,g-9)
    c: Coincident(g6,g5)
    c: PointOnObject(g6,g-8)
    c: Coincident(g7,g-9)
    c: PointOnObject(g7,g-9)
    c: Coincident(g8,g7)
    c: PointOnObject(g8,g-7)
    c: Coincident(g9,g0)
    c: PointOnObject(g9,g-7)
    c: Coincident(g10,g0)
    c: PointOnObject(g10,g0)
    c: Coincident(g11,g0)
    c: PointOnObject(g11,g0)
    c: Coincident(g12,g0)
    c: PointOnObject(g12,g-8)
    c: Coincident(g13,g11)
    c: Horizontal(g13)
    c: Coincident(g14,g12)
    c: Vertical(g14)
    c: Coincident(g15,g10)
    c: Horizontal(g15)
    c: Coincident(g16,g9)
    c: Vertical(g16)
    c: Coincident(g17,g6)
    c: Vertical(g17)
    c: Coincident(g18,g5)
    c: Horizontal(g18)
    c: Coincident(g19,g7)
    c: Horizontal(g19)
    c: Coincident(g20,g8)
    c: Vertical(g20)
    c: Tangent(g20,g4) = 1.5708
    c: Tangent(g4,g19) = -1.5708
    c: Tangent(g18,g3) = 1.5708
    c: Tangent(g3,g17) = -1.5708
    c: Tangent(g13,g1) = -1.5708
    c: Tangent(g1,g14) = 1.5708
    c: Tangent(g16,g2) = -1.5708
    c: Tangent(g2,g15) = 1.5708
FEATURE [PartDesign::Pocket] Pocket008
  BaseFeature = -> Pad013
  Direction = (0,1,-2e-16)
  Length = 1.6
  Length2 = 5
  Profile = -> Sketch119
  ReferenceAxis = -> Sketch119 [N_Axis]
  Refine = true
  Suppressed = false
  Type = 0
FEATURE [PartDesign::Pad] Pad017
  BaseFeature = -> Pocket008
  Direction = (0,-1,2e-16)
  Length = 1.6
  Length2 = 10
  Profile = -> Sketch123
  ReferenceAxis = -> Sketch123 [N_Axis]
  Refine = true
  Suppressed = false
  Type = 0
FEATURE [Sketcher::SketchObject] Sketch125
  ArcFitTolerance = 1e-06
  AttachmentSupport = -> [Pad017]
  ExternalGeometry = -> [Pad017]
  FullyConstrained = true
  MakeInternals = false
  MapMode = 5
  Placement = pos=(0,-3.6,8e-16) rot=(1,0,0;1.5708rad)
  sketch-geometry (20):
    g0: LineSegment StartX=-108 StartY=35.8 StartZ=0 EndX=-108 EndY=35 EndZ=0
    g1: LineSegment StartX=-108 StartY=35 StartZ=0 EndX=-97 EndY=35 EndZ=0
    g2: LineSegment StartX=-97 StartY=35 StartZ=0 EndX=-97 EndY=35.8 EndZ=0
    g3: LineSegment StartX=-97 StartY=35.8 StartZ=0 EndX=-108 EndY=35.8 EndZ=0
    g4: LineSegment StartX=-108 StartY=28.6 StartZ=0 EndX=-108 EndY=27.8 EndZ=0
    g5: LineSegment StartX=-108 StartY=27.8 StartZ=0 EndX=-97 EndY=27.8 EndZ=0
    g6: LineSegment StartX=-97 StartY=27.8 StartZ=0 EndX=-97 EndY=28.6 EndZ=0
    g7: LineSegment StartX=-97 StartY=28.6 StartZ=0 EndX=-108 EndY=28.6 EndZ=0
    g8: LineSegment StartX=-108 StartY=30.4 StartZ=0 EndX=-108 EndY=29.6 EndZ=0
    g9: LineSegment StartX=-108 StartY=29.6 StartZ=0 EndX=-97 EndY=29.6 EndZ=0
    g10: LineSegment StartX=-97 StartY=29.6 StartZ=0 EndX=-97 EndY=30.4 EndZ=0
    g11: LineSegment StartX=-97 StartY=30.4 StartZ=0 EndX=-108 EndY=30.4 EndZ=0
    g12: LineSegment StartX=-108 StartY=32.2 StartZ=0 EndX=-108 EndY=31.4 EndZ=0
    g13: LineSegment StartX=-108 StartY=31.4 StartZ=0 EndX=-97 EndY=31.4 EndZ=0
    g14: LineSegment StartX=-97 StartY=31.4 StartZ=0 EndX=-97 EndY=32.2 EndZ=0
    g15: LineSegment StartX=-97 StartY=32.2 StartZ=0 EndX=-108 EndY=32.2 EndZ=0
    g16: LineSegment StartX=-108 StartY=34 StartZ=0 EndX=-108 EndY=33.2 EndZ=0
    g17: LineSegment StartX=-108 StartY=33.2 StartZ=0 EndX=-97 EndY=33.2 EndZ=0
    g18: LineSegment StartX=-97 StartY=33.2 StartZ=0 EndX=-97 EndY=34 EndZ=0
    g19: LineSegment StartX=-97 StartY=34 StartZ=0 EndX=-108 EndY=34 EndZ=0
  constraints (55):
    c: Coincident(g1,g0)
    c: Horizontal(g1)
    c: Coincident(g2,g1)
    c: Vertical(g2)
    c: Coincident(g3,g2)
    c: Horizontal(g3)
    c: Coincident(g3,g0)
    c: DistanceX(g1,g1) = 11
    c: DistanceY(g2,g2) = 0.8
    c: Coincident(g5,g4)
    c: Horizontal(g5)
    c: Coincident(g6,g5)
    c: Vertical(g6)
    c: Coincident(g7,g6)
    c: Horizontal(g7)
    c: Coincident(g7,g4)
    c: Coincident(g9,g8)
    c: Horizontal(g9)
    c: Coincident(g10,g9)
    c: Vertical(g10)
    c: Coincident(g11,g10)
    c: Horizontal(g11)
    c: Coincident(g11,g8)
    c: Coincident(g13,g12)
    c: Horizontal(g13)
    c: Coincident(g14,g13)
    c: Vertical(g14)
    c: Coincident(g15,g14)
    c: Horizontal(g15)
    c: Coincident(g15,g12)
    c: Coincident(g17,g16)
    c: Horizontal(g17)
    c: Coincident(g18,g17)
    c: Vertical(g18)
    c: Coincident(g19,g18)
    c: Horizontal(g19)
    c: Coincident(g19,g16)
    c: Equal(g3,g19)
    c: Equal(g3,g15)
    c: Equal(g3,g11)
    c: Equal(g3,g7)
    c: Equal(g2,g18)
    c: Equal(g2,g14)
    c: Equal(g2,g10)
    c: Equal(g2,g6)
    c: DistanceY(g-4,g4) = 1
    c: DistanceY(g4,g8) = 1
    c: DistanceY(g8,g12) = 1
    c: DistanceY(g12,g16) = 1
    c: DistanceY(g16,g0) = 1
    c: Tangent(g0,g-5)
    c: Tangent(g16,g-5)
    c: Tangent(g12,g-5)
    c: Tangent(g8,g-5)
    c: Tangent(g4,g-5)
FEATURE [PartDesign::Chamfer] Chamfer009
  Angle = 45
  Base = -> Pad017 [Edge151,Edge154]
  BaseFeature = -> Pad017
  ChamferType = 1
  FlipDirection = false
  Refine = true
  Size = 1.5
  Size2 = 2.8
  SupportTransform = false
  Suppressed = false
  UseAllEdges = false
FEATURE [PartDesign::Pocket] Pocket009
  BaseFeature = -> Chamfer009
  Direction = (0,1,-2e-16)
  Length = 1
  Length2 = 5
  Profile = -> Sketch125
  ReferenceAxis = -> Sketch125 [N_Axis]
  Refine = true
  Suppressed = false
  Type = 0
FEATURE [PartDesign::Pad] Pad014
  BaseFeature = -> Pocket009
  Direction = (0,-1,2e-16)
  Length = 0.8
  Length2 = 10
  Profile = -> Sketch120
  ReferenceAxis = -> Sketch120 [N_Axis]
  Refine = true
  Suppressed = false
  Type = 0
FEATURE [Sketcher::SketchObject] Sketch124
  ArcFitTolerance = 1e-06
  AttachmentSupport = -> [Pad014]
  ExternalGeometry = -> [Binder001]
  FullyConstrained = true
  MakeInternals = false
  MapMode = 5
  Placement = pos=(0,-2.8,6e-16) rot=(1,0,0;1.5708rad)
  sketch-geometry (4):
    g0: LineSegment StartX=-129 StartY=39.2 StartZ=0 EndX=-131.599 EndY=31.2 EndZ=0
    g1: LineSegment StartX=-118 StartY=39.2 StartZ=0 EndX=-120.599 EndY=31.2 EndZ=0
    g2: LineSegment StartX=-129 StartY=39.2 StartZ=0 EndX=-118 EndY=39.2 EndZ=0
    g3: LineSegment StartX=-120.599 StartY=31.2 StartZ=0 EndX=-131.599 EndY=31.2 EndZ=0
  constraints (12):
    c: PointOnObject(g0,g-3)
    c: PointOnObject(g1,g-3)
    c: Parallel(g-4,g0)
    c: Parallel(g-4,g1)
    c: Coincident(g2,g0)
    c: Coincident(g2,g1)
    c: DistanceX(g2,g2) = 11
    c: DistanceY(g1,g1) = 8
    c: Coincident(g3,g1)
    c: Horizontal(g3)
    c: Coincident(g3,g0)
    c: DistanceX(g1,g-3) = 118
FEATURE [PartDesign::Pad] Pad018
  BaseFeature = -> Pad014
  Direction = (0,-1,2e-16)
  Length = 1.2
  Length2 = 10
  Profile = -> Sketch124
  ReferenceAxis = -> Sketch124 [N_Axis]
  Refine = true
  Suppressed = false
  Type = 0
FEATURE [Sketcher::SketchObject] Sketch126
  ArcFitTolerance = 1e-06
  AttachmentSupport = -> [Pad018]
  ExternalGeometry = -> [Pad018]
  FullyConstrained = true
  MakeInternals = false
  MapMode = 5
  Placement = pos=(0,-4,0) rot=(1,0,0;1.5708rad)
  sketch-geometry (8):
    g0: LineSegment StartX=-129.877 StartY=36.5 StartZ=0 EndX=-130.137 EndY=35.7 EndZ=0
    g1: LineSegment StartX=-130.69 StartY=34 StartZ=0 EndX=-130.95 EndY=33.2 EndZ=0
    g2: LineSegment StartX=-129.877 StartY=36.5 StartZ=0 EndX=-118.877 EndY=36.5 EndZ=0
    g3: LineSegment StartX=-130.137 StartY=35.7 StartZ=0 EndX=-119.137 EndY=35.7 EndZ=0
    g4: LineSegment StartX=-130.69 StartY=34 StartZ=0 EndX=-119.69 EndY=34 EndZ=0
    g5: LineSegment StartX=-130.95 StartY=33.2 StartZ=0 EndX=-119.95 EndY=33.2 EndZ=0
    g6: LineSegment StartX=-118.877 StartY=36.5 StartZ=0 EndX=-119.137 EndY=35.7 EndZ=0
    g7: LineSegment StartX=-119.69 StartY=34 StartZ=0 EndX=-119.95 EndY=33.2 EndZ=0
  constraints (20):
    c: Coincident(g2,g0)
    c: Horizontal(g2)
    c: Coincident(g3,g0)
    c: Horizontal(g3)
    c: Coincident(g4,g1)
    c: Horizontal(g4)
    c: Coincident(g5,g1)
    c: Horizontal(g5)
    c: Coincident(g6,g2)
    c: Coincident(g6,g3)
    c: Coincident(g7,g4)
    c: Coincident(g7,g5)
    c: Tangent(g0,g-4)
    c: Tangent(g6,g-5)
    c: Tangent(g1,g-4)
    c: Tangent(g7,g-5)
    c: DistanceY(g3,g2) = 0.8
    c: DistanceY(g5,g4) = 0.8
    c: DistanceY(g-6,g1) = 2
    c: DistanceY(g-6,g0) = 4.5
FEATURE [PartDesign::Chamfer] Chamfer008
  Angle = 45
  Base = -> Pad018 [Edge257]
  BaseFeature = -> Pad018
  ChamferType = 1
  FlipDirection = false
  Refine = true
  Size = 1
  Size2 = 6
  SupportTransform = false
  Suppressed = false
  UseAllEdges = false
FEATURE [PartDesign::Pocket] Pocket010
  BaseFeature = -> Chamfer008
  Direction = (0,1,-2e-16)
  Length = 1
  Length2 = 5
  Profile = -> Sketch126
  ReferenceAxis = -> Sketch126 [N_Axis]
  Refine = true
  Suppressed = false
  Type = 0
FEATURE [PartDesign::Pad] Pad015
  BaseFeature = -> Pocket010
  Direction = (0,-1,2e-16)
  Length = 2
  Length2 = 10
  Profile = -> Sketch121
  ReferenceAxis = -> Sketch121 [N_Axis]
  Refine = true
  Suppressed = false
  Type = 0
FEATURE [PartDesign::Pad] Pad016
  BaseFeature = -> Pad015
  Direction = (0,-1,2e-16)
  Length = 1.6
  Length2 = 10
  Profile = -> Sketch122
  ReferenceAxis = -> Sketch122 [N_Axis]
  Refine = true
  Suppressed = false
  Type = 0
FEATURE [Sketcher::SketchObject] Sketch127
  ArcFitTolerance = 1e-06
  AttachmentSupport = -> [Pad016]
  ExternalGeometry = -> [Pad016]
  FullyConstrained = true
  MakeInternals = false
  MapMode = 5
  Placement = pos=(0,0,-80.4316) rot=(1,0,0;3.14159rad)
  sketch-geometry (8):
    g0: LineSegment StartX=-176.685 StartY=3.6 StartZ=0 EndX=-186.685 EndY=3.6 EndZ=0
    g1: LineSegment [constr] StartX=-186.685 StartY=3.6 StartZ=0 EndX=-186.685 EndY=-9e-16 EndZ=0
    g2: LineSegment StartX=-176.685 StartY=3.6 StartZ=0 EndX=-176.685 EndY=0 EndZ=0
    g3: ArcOfEllipse CenterX=-186.685 CenterY=-9e-16 CenterZ=0 NormalX=0 NormalY=0 NormalZ=1 MajorRadius=10 MinorRadius=3.6 AngleXU=1e-16 StartAngle=0 EndAngle=1.5708
    g4: LineSegment [constr] StartX=-176.685 StartY=-2e-15 StartZ=0 EndX=-196.685 EndY=-2e-15 EndZ=0
    g5: LineSegment [constr] StartX=-186.685 StartY=3.6 StartZ=0 EndX=-186.685 EndY=-3.6 EndZ=0
    g6: GeomPoint [constr] X=-177.356 Y=0 Z=0
    g7: GeomPoint [constr] X=-196.015 Y=-1.9e-15 Z=0
  constraints (13):
    c: Coincident(g0,g-4)
    c: PointOnObject(g0,g-4)
    c: DistanceX(g0,g0) = 10
    c: Coincident(g1,g0)
    c: PointOnObject(g1,g-5)
    c: Vertical(g1)
    c: Coincident(g2,g0)
    c: Coincident(g2,g-5)
    c: InternalAlignment(g4-g7 -> g3) x4
    c: Coincident(g3,g1)
    c: Coincident(g3,g0)
    c: Coincident(g3,g2)
    c: Horizontal(g4)
FEATURE [Sketcher::SketchObject] Sketch128
  ArcFitTolerance = 1e-06
  AttachmentSupport = -> [Pad016]
  ExternalGeometry = -> [Pad016]
  FullyConstrained = true
  MakeInternals = false
  MapMode = 5
  Placement = pos=(0,0,-80.4316) rot=(1,0,0;3.14159rad)
  sketch-geometry (8):
    g0: LineSegment StartX=-215.932 StartY=3.6 StartZ=0 EndX=-215.932 EndY=-1.3e-15 EndZ=0
    g1: LineSegment StartX=-215.932 StartY=3.6 StartZ=0 EndX=-205.932 EndY=3.6 EndZ=0
    g2: LineSegment [constr] StartX=-205.932 StartY=3.6 StartZ=0 EndX=-205.932 EndY=-9e-16 EndZ=0
    g3: ArcOfEllipse CenterX=-205.932 CenterY=-9e-16 CenterZ=0 NormalX=0 NormalY=0 NormalZ=1 MajorRadius=10 MinorRadius=3.6 AngleXU=-3.14159 StartAngle=4.71239 EndAngle=6.28319
    g4: LineSegment [constr] StartX=-215.932 StartY=-1e-15 StartZ=0 EndX=-195.932 EndY=-1e-15 EndZ=0
    g5: LineSegment [constr] StartX=-205.932 StartY=-3.6 StartZ=0 EndX=-205.932 EndY=3.6 EndZ=0
    g6: GeomPoint [constr] X=-215.262 Y=-2e-15 Z=0
    g7: GeomPoint [constr] X=-196.602 Y=-1e-15 Z=0
  constraints (13):
    c: Coincident(g0,g-4)
    c: Coincident(g0,g-5)
    c: Coincident(g1,g0)
    c: PointOnObject(g1,g-3)
    c: DistanceX(g1,g1) = 10
    c: Coincident(g2,g1)
    c: Vertical(g2)
    c: PointOnObject(g2,g-5)
    c: InternalAlignment(g4-g7 -> g3) x4
    c: Coincident(g3,g2)
    c: Coincident(g3,g1)
    c: Coincident(g3,g0)
    c: Horizontal(g4)
FEATURE [PartDesign::SubtractivePipe] SubtractivePipe002
  AuxilleryCurvelinear = true
  AuxillerySpineTangent = false
  BaseFeature = -> Pad016
  Binormal = (0,0,0)
  Mode = 0
  Profile = -> Sketch127
  Refine = true
  Spine = -> Pad016 [Edge254]
  SpineTangent = false
  Suppressed = false
  Transformation = 0
  Transition = 0
FEATURE [PartDesign::SubtractivePipe] SubtractivePipe003
  AuxilleryCurvelinear = true
  AuxillerySpineTangent = false
  BaseFeature = -> SubtractivePipe002
  Binormal = (0,0,0)
  Mode = 0
  Profile = -> Sketch128
  Refine = true
  Spine = -> Pad016 [Edge256,Edge251,Edge252]
  SpineTangent = false
  Suppressed = false
  Transformation = 0
  Transition = 0
FEATURE [Sketcher::SketchObject] Sketch129
  ArcFitTolerance = 1e-06
  AttachmentSupport = -> [Pad016]
  ExternalGeometry = -> [Binder001]
  FullyConstrained = true
  MakeInternals = false
  MapMode = 5
  Placement = pos=(0,-3.6,0) rot=(1,0,0;1.5708rad)
  sketch-geometry (12):
    g0: LineSegment [constr] StartX=-192.176 StartY=-3.18451 StartZ=0 EndX=-181.223 EndY=20.303 EndZ=0
    g1: LineSegment [constr] StartX=-202.765 StartY=20.303 StartZ=0 EndX=-181.223 EndY=20.303 EndZ=0
    g2: LineSegment StartX=-202.765 StartY=20.303 StartZ=0 EndX=-181.223 EndY=20.303 EndZ=0
    g3: LineSegment StartX=-192.176 StartY=-3.18451 StartZ=0 EndX=-196.804 EndY=-13.1107 EndZ=0
    g4: ArcOfCircle CenterX=-207.583 CenterY=4 CenterZ=0 NormalX=0 NormalY=0 NormalZ=1 AngleXU=0 Radius=17 StartAngle=5.84685 EndAngle=7.56663
    g5: ArcOfEllipse CenterX=-181.223 CenterY=8.55923 CenterZ=0 NormalX=0 NormalY=0 NormalZ=1 MajorRadius=23.4779 MinorRadius=11.7437 AngleXU=2e-16 StartAngle=4.71239 EndAngle=7.85398
    g6: LineSegment [constr] StartX=-157.745 StartY=8.55923 StartZ=0 EndX=-204.701 EndY=8.55923 EndZ=0
    g7: LineSegment [constr] StartX=-181.223 StartY=20.303 StartZ=0 EndX=-181.223 EndY=-3.18451 EndZ=0
    g8: GeomPoint [constr] X=-160.894 Y=8.55923 Z=0
    g9: GeomPoint [constr] X=-201.553 Y=8.55923 Z=0
    g10: ArcOfCircle CenterX=-181.223 CenterY=-20.3763 CenterZ=0 NormalX=0 NormalY=0 NormalZ=1 AngleXU=0 Radius=17.1918 StartAngle=1.57079 EndAngle=2.70526
    g11: GeomPoint [constr] X=-181.223 Y=-3.18451 Z=0
  constraints (23):
    c: Coincident(g0,g-5)
    c: Coincident(g1,g-6)
    c: Horizontal(g1)
    c: Coincident(g1,g0)
    c: Parallel(g0,g-4)
    c: Coincident(g2,g1)
    c: Coincident(g2,g0)
    c: Coincident(g3,g0)
    c: Equal(g4,g-5)
    c: Coincident(g4,g1)
    c: Coincident(g4,g0)
    c: InternalAlignment(g6-g9 -> g5) x4
    c: Vertical(g5,g0)
    c: Horizontal(g6)
    c: Coincident(g5,g0)
    c: DistanceX(g6,g-3) = 10.1
    c: Tangent(g10,g3) = -1.5708
    c: PointOnObject(g11,g10)
    c: Tangent(g5,g10,g11) = 1.5708
    c: Coincident(g10,g5)
    c: Coincident(g11,g7)
    c: Parallel(g3,g-4)
    c: Horizontal(g5,g0)
FEATURE [Sketcher::SketchObject] Sketch130
  ArcFitTolerance = 1e-06
  AttachmentOffset = pos=(0,0,-1.6) rot=(0,0,1;0rad)
  AttachmentSupport = -> [Pad016]
  ExternalGeometry = -> [Binder001]
  FullyConstrained = true
  MakeInternals = false
  MapMode = 5
  Placement = pos=(0,-2,-4e-16) rot=(1,0,0;1.5708rad)
  sketch-geometry (12):
    g0: LineSegment [constr] StartX=-192.176 StartY=-3.18451 StartZ=0 EndX=-181.223 EndY=20.303 EndZ=0
    g1: LineSegment [constr] StartX=-202.765 StartY=20.303 StartZ=0 EndX=-181.223 EndY=20.303 EndZ=0
    g2: LineSegment StartX=-202.765 StartY=20.303 StartZ=0 EndX=-181.223 EndY=20.303 EndZ=0
    g3: LineSegment StartX=-192.176 StartY=-3.18451 StartZ=0 EndX=-193.827 EndY=-6.72678 EndZ=0
    g4: ArcOfCircle CenterX=-207.583 CenterY=4 CenterZ=0 NormalX=0 NormalY=0 NormalZ=1 AngleXU=0 Radius=17 StartAngle=5.84685 EndAngle=7.56663
    g5: ArcOfEllipse CenterX=-181.223 CenterY=10.803 CenterZ=0 NormalX=0 NormalY=0 NormalZ=1 MajorRadius=14.4779 MinorRadius=9.5 AngleXU=0 StartAngle=4.71239 EndAngle=7.85398
    g6: LineSegment [constr] StartX=-166.745 StartY=10.803 StartZ=0 EndX=-195.701 EndY=10.803 EndZ=0
    g7: LineSegment [constr] StartX=-181.223 StartY=20.303 StartZ=0 EndX=-181.223 EndY=1.30297 EndZ=0
    g8: GeomPoint [constr] X=-170.298 Y=10.803 Z=0
    g9: GeomPoint [constr] X=-192.148 Y=10.803 Z=0
    g10: ArcOfCircle CenterX=-181.223 CenterY=-12.6042 CenterZ=0 NormalX=0 NormalY=0 NormalZ=1 AngleXU=0 Radius=13.9072 StartAngle=1.5708 EndAngle=2.70526
    g11: GeomPoint [constr] X=-181.223 Y=1.30297 Z=0
  constraints (23):
    c: Coincident(g0,g-5)
    c: Coincident(g1,g-6)
    c: Horizontal(g1)
    c: Coincident(g1,g0)
    c: Parallel(g0,g-4)
    c: Coincident(g2,g1)
    c: Coincident(g2,g0)
    c: Coincident(g3,g0)
    c: Equal(g4,g-5)
    c: Coincident(g4,g1)
    c: Coincident(g4,g0)
    c: InternalAlignment(g6-g9 -> g5) x4
    c: Vertical(g5,g0)
    c: Horizontal(g6)
    c: Coincident(g5,g0)
    c: DistanceX(g6,g-3) = 19.1
    c: Tangent(g10,g3) = -1.5708
    c: PointOnObject(g11,g10)
    c: Tangent(g5,g10,g11) = 1.5708
    c: Coincident(g10,g5)
    c: Coincident(g11,g7)
    c: Parallel(g3,g-4)
    c: DistanceY(g5,g0) = 19
FEATURE [Part::Part2DObjectPython] Clone2D001  label="Sketch130 (2D)"  # Draft 2D object (typed FeaturePython)
  Fuse = false
  Objects = -> [Sketch130]
  Placement = pos=(0,-2,-4e-16) rot=(1,0,0;1.5708rad)
  Scale = (1,1,1)
FEATURE [Sketcher::SketchObject] Sketch131
  ArcFitTolerance = 1e-06
  AttachmentOffset = pos=(0,0,-3.5) rot=(0,0,1;0rad)
  AttachmentSupport = -> [Pad016]
  ExternalGeometry = -> [Binder001]
  FullyConstrained = true
  MakeInternals = false
  MapMode = 5
  Placement = pos=(0,-0.1,-8e-16) rot=(1,0,0;1.5708rad)
  sketch-geometry (1):
    g0: GeomPoint X=-197.47 Y=8.55923 Z=0
  constraints (1):
    c: Symmetric(g-6,g-4,g0)
FEATURE [PartDesign::SubtractiveLoft] SubtractiveLoft002
  BaseFeature = -> SubtractivePipe003
  Closed = false
  Profile = -> Sketch129
  Refine = true
  Ruled = false
  Sections = -> [Sketch130]
  Suppressed = false
FEATURE [PartDesign::SubtractiveLoft] SubtractiveLoft003
  BaseFeature = -> SubtractiveLoft002
  Closed = false
  Profile = -> Clone2D001
  Refine = true
  Ruled = false
  Sections = -> [Sketch131]
  Suppressed = false
FEATURE [PartDesign::Chamfer] Chamfer010
  Angle = 45
  Base = -> SubtractiveLoft003 [Edge200,Edge201,Edge203,Edge202,Edge194]
  BaseFeature = -> SubtractiveLoft003
  ChamferType = 0
  FlipDirection = false
  Refine = true
  Size = 1.5
  Size2 = 1
  SupportTransform = false
  Suppressed = false
  UseAllEdges = false
FEATURE [PartDesign::Chamfer] Chamfer011
  Angle = 45
  Base = -> Chamfer010 [Edge15]
  BaseFeature = -> Chamfer010
  ChamferType = 0
  FlipDirection = false
  Refine = true
  Size = 3.5
  Size2 = 1
  SupportTransform = false
  Suppressed = false
  UseAllEdges = false
FEATURE [PartDesign::Chamfer] Chamfer012
  Angle = 45
  Base = -> Chamfer011 [Edge10]
  BaseFeature = -> Chamfer011
  ChamferType = 0
  FlipDirection = false
  Refine = true
  Size = 3.5
  Size2 = 1
  SupportTransform = false
  Suppressed = false
  UseAllEdges = false
FEATURE [PartDesign::Chamfer] Chamfer013
  Angle = 45
  Base = -> Chamfer012 [Edge146,Edge93]
  BaseFeature = -> Chamfer012
  ChamferType = 0
  FlipDirection = false
  Refine = true
  Size = 1.9
  Size2 = 1
  SupportTransform = false
  Suppressed = false
  UseAllEdges = false
FEATURE [Sketcher::SketchObject] Sketch132
  ArcFitTolerance = 1e-06
  AttachmentSupport = -> [Pad016]
  ExternalGeometry = -> [Binder001]
  FullyConstrained = true
  MakeInternals = false
  MapMode = 5
  Placement = pos=(0,-3.6,0) rot=(1,0,0;1.5708rad)
  sketch-geometry (3):
    g0: LineSegment [constr] StartX=-215.42 StartY=-53.0314 StartZ=0 EndX=-167.782 EndY=-53.0314 EndZ=0
    g1: Circle CenterX=-191.282 CenterY=-53.0314 CenterZ=0 NormalX=0 NormalY=0 NormalZ=1 AngleXU=0 Radius=11.5
    g2: Circle CenterX=-191.282 CenterY=-53.0314 CenterZ=0 NormalX=0 NormalY=0 NormalZ=1 AngleXU=0 Radius=10.7
  constraints (8):
    c: Coincident(g0,g-3)
    c: PointOnObject(g0,g-4)
    c: Horizontal(g0)
    c: Diameter(g1) = 23
    c: PointOnObject(g1,g0)
    c: DistanceX(g1,g0) = 23.5
    c: Diameter(g2) = 21.4
    c: Coincident(g2,g1)
FEATURE [PartDesign::Fillet] Fillet007
  Base = -> Chamfer013 [Edge84]
  BaseFeature = -> Chamfer013
  Radius = 1.1
  Refine = true
  SupportTransform = false
  Suppressed = false
  UseAllEdges = false
FEATURE [PartDesign::Fillet] Fillet008
  Base = -> Fillet007 [Edge77]
  BaseFeature = -> Fillet007
  Radius = 1.9
  Refine = true
  SupportTransform = false
  Suppressed = false
  UseAllEdges = false
FEATURE [PartDesign::Pocket] Pocket011
  BaseFeature = -> Fillet008
  Direction = (0,1,-2e-16)
  Length = 0.8
  Length2 = 5
  Profile = -> Sketch132
  ReferenceAxis = -> Sketch132 [N_Axis]
  Refine = true
  Suppressed = false
  Type = 0
FEATURE [Part::Part2DObjectPython] ShapeString  # Draft 2D object (typed FeaturePython)
  FontFile = <path>
  Fuse = false
  Justification = 6
  JustificationReference = 0
  KeepLeftMargin = false
  MakeFace = true
  ObliqueAngle = 0
  Placement = pos=(-199,-3.6,-57.5) rot=(1,0,0;1.5708rad)
  ScaleToSize = true
  Size = 10
  String = AS
  Tracking = 0
FEATURE [PartDesign::Pocket] Pocket012
  BaseFeature = -> Pocket011
  Direction = (0,1,0)
  Length = 1
  Length2 = 5
  Profile = -> ShapeString
  ReferenceAxis = -> ShapeString [N_Axis]
  Refine = true
  Suppressed = false
  Type = 0
FEATURE [PartDesign::Body] Body007  label="lato DX"
  AllowCompound = false
  Group = -> [Binder001,Sketch114,Pad011,Chamfer014,Sketch115,Pocket006,Sketch116,Pad012,Sketch117,Pocket007,Sketch118,Pad013,Sketch119,Pocket008,Pad017,Chamfer009,Pocket009,Sketch123,Sketch120,Pad014,Pad018,Chamfer008,Pocket010,Sketch121,Pad015,Sketch122,Pad016,Sketch124,Sketch125,Sketch126,Sketch127,Sketch128,SubtractivePipe002,SubtractivePipe003,Sketch129,Sketch130,Clone2D001,Sketch131,SubtractiveLoft002,+11 more]
  Origin = -> Origin007
  Tip = -> Pocket012
FEATURE [Sketcher::SketchObject] Sketch133
  ArcFitTolerance = 1e-06
  AttachmentSupport = -> [Binder]
  ExternalGeometry = -> [Binder]
  FullyConstrained = true
  MakeInternals = false
  MapMode = 5
  Placement = pos=(0,9e-16,0) rot=(0,0.707107,0.707107;3.14159rad)
  sketch-geometry (30):
    g0: LineSegment StartX=0 StartY=39.2 StartZ=0 EndX=0 EndY=3.2 EndZ=0
    g1: LineSegment StartX=0 StartY=3.2 StartZ=0 EndX=82.8 EndY=3.2 EndZ=0
    g2: LineSegment StartX=82.8 StartY=3.2 StartZ=0 EndX=82.8 EndY=6.2 EndZ=0
    g3: LineSegment StartX=82.8 StartY=6.2 StartZ=0 EndX=91.752 EndY=6.2 EndZ=0
    g4: LineSegment StartX=0 StartY=39.2 StartZ=0 EndX=195.887 EndY=39.2 EndZ=0
    g5: LineSegment StartX=195.887 StartY=39.2 StartZ=0 EndX=202.765 EndY=20.303 EndZ=0
    g6: LineSegment StartX=192.333 StartY=24.9893 StartZ=0 EndX=196.467 EndY=26.4942 EndZ=0
    g7: LineSegment StartX=196.467 StartY=26.4942 StartZ=0 EndX=194.073 EndY=33.0721 EndZ=0
    g8: LineSegment StartX=194.073 StartY=33.0721 StartZ=0 EndX=189.939 EndY=31.5672 EndZ=0
    g9: LineSegment StartX=189.939 StartY=31.5672 StartZ=0 EndX=192.333 EndY=24.9893 EndZ=0
    g10: ArcOfCircle CenterX=107.6 CenterY=4 CenterZ=0 NormalX=0 NormalY=0 NormalZ=1 AngleXU=0 Radius=16 StartAngle=1.5708 EndAngle=3.00366
    g11: LineSegment StartX=107.6 StartY=20 StartZ=0 EndX=132.428 EndY=20 EndZ=0
    g12: ArcOfCircle [constr] CenterX=132.428 CenterY=4 CenterZ=0 NormalX=0 NormalY=0 NormalZ=1 AngleXU=0 Radius=16 StartAngle=0.314159 EndAngle=1.5708
    g13: LineSegment StartX=147.645 StartY=8.94427 StartZ=0 EndX=176.685 EndY=-80.4316 EndZ=0
    g14: LineSegment StartX=176.685 StartY=-80.4316 StartZ=0 EndX=215.932 EndY=-80.4316 EndZ=0
    g15: ArcOfCircle CenterX=207.583 CenterY=4 CenterZ=0 NormalX=0 NormalY=0 NormalZ=1 AngleXU=0 Radius=17 StartAngle=1.85815 EndAngle=3.57792
    g16: ArcOfCircle CenterX=184.801 CenterY=-67.3089 CenterZ=0 NormalX=0 NormalY=0 NormalZ=1 AngleXU=0 Radius=33.7833 StartAngle=5.88425 EndAngle=6.71952
    g17: LineSegment StartX=192.176 StartY=-3.18451 StartZ=0 EndX=215.42 EndY=-53.0314 EndZ=0
    g18: Circle CenterX=5.6 CenterY=34.8 CenterZ=0 NormalX=0 NormalY=0 NormalZ=1 AngleXU=0 Radius=1.8
    g19: Circle CenterX=5.6 CenterY=7.6 CenterZ=0 NormalX=0 NormalY=0 NormalZ=1 AngleXU=0 Radius=1.8
    g20: Circle CenterX=78.51 CenterY=34.8 CenterZ=0 NormalX=0 NormalY=0 NormalZ=1 AngleXU=0 Radius=1.8
    g21: Circle CenterX=78.51 CenterY=7.6 CenterZ=0 NormalX=0 NormalY=0 NormalZ=1 AngleXU=0 Radius=1.8
    g22: Circle CenterX=184.08 CenterY=34.8 CenterZ=0 NormalX=0 NormalY=0 NormalZ=1 AngleXU=0 Radius=1.8
    g23: Circle CenterX=179.305 CenterY=-76.8316 CenterZ=0 NormalX=0 NormalY=0 NormalZ=1 AngleXU=0 Radius=1.8
    g24: Circle CenterX=213.443 CenterY=-76.8316 CenterZ=0 NormalX=0 NormalY=0 NormalZ=1 AngleXU=0 Radius=1.8
    g25: Circle CenterX=19 CenterY=21.2 CenterZ=0 NormalX=0 NormalY=0 NormalZ=1 AngleXU=0 Radius=6.3
    g26: Circle CenterX=42 CenterY=21.2 CenterZ=0 NormalX=0 NormalY=0 NormalZ=1 AngleXU=0 Radius=6.3
    g27: Circle CenterX=65 CenterY=21.2 CenterZ=0 NormalX=0 NormalY=0 NormalZ=1 AngleXU=0 Radius=6.3
    g28: LineSegment StartX=132.428 StartY=20 StartZ=0 EndX=144.053 EndY=20 EndZ=0
    g29: LineSegment StartX=147.645 StartY=8.94427 StartZ=0 EndX=144.053 EndY=20 EndZ=0
  constraints (65):
    c: Coincident(g0,g-4)
    c: Coincident(g0,g-5)
    c: Coincident(g1,g0)
    c: Coincident(g1,g-6)
    c: Coincident(g2,g1)
    c: Coincident(g2,g-7)
    c: Coincident(g3,g2)
    c: Coincident(g3,g-8)
    c: Coincident(g4,g0)
    c: Coincident(g4,g-16)
    c: Coincident(g5,g4)
    c: Coincident(g5,g-16)
    c: Coincident(g6,g-20)
    c: Coincident(g6,g-21)
    c: Coincident(g7,g6)
    c: Coincident(g7,g-23)
    c: Coincident(g8,g7)
    c: Coincident(g8,g-22)
    c: Coincident(g9,g8)
    c: Coincident(g9,g6)
    c: Equal(g10,g-8)
    c: Coincident(g10,g3)
    c: Coincident(g10,g-9)
    c: Coincident(g11,g10)
    c: Coincident(g11,g-10)
    c: Equal(g12,g-10)
    c: Coincident(g12,g11)
    c: Coincident(g12,g-11)
    c: Coincident(g13,g12)
    c: Coincident(g13,g-12)
    c: Coincident(g14,g13)
    c: Coincident(g14,g-13)
    c: Equal(g15,g-15)
    c: Coincident(g15,g5)
    c: Coincident(g15,g-15)
    c: Equal(g16,g-13)
    c: Coincident(g16,g14)
    c: Coincident(g16,g-14)
    c: Coincident(g17,g15)
    c: Coincident(g17,g16)
    c: Equal(g18,g-28)
    c: Equal(g19,g-29)
    c: Equal(g20,g-26)
    c: Equal(g21,g-27)
    c: Equal(g22,g-17)
    c: Equal(g24,g-25)
    c: Equal(g23,g-24)
    c: Coincident(g23,g-24)
    c: Coincident(g24,g-25)
    c: Coincident(g22,g-17)
    c: Coincident(g20,g-26)
    c: Coincident(g21,g-27)
    c: Coincident(g18,g-28)
    c: Coincident(g19,g-29)
    c: Equal(g25,g-30)
    c: Equal(g26,g-31)
    c: Equal(g27,g-32)
    c: Coincident(g25,g-30)
    c: Coincident(g26,g-31)
    c: Coincident(g27,g-32)
    c: Parallel(g28,g11)
    c: Parallel(g29,g13)
    c: Coincident(g28,g11)
    c: Coincident(g29,g12)
    c: Coincident(g29,g28)
FEATURE [PartDesign::Pad] Pad019
  Direction = (0,1,-2e-16)
  Length = 2
  Length2 = 10
  Profile = -> Sketch133
  ReferenceAxis = -> Sketch133 [N_Axis]
  Refine = true
  Suppressed = false
  Type = 0
FEATURE [Sketcher::SketchObject] Sketch091  label="Sketch091 - forma anteriore"
  ArcFitTolerance = 1e-06
  AttachmentSupport = -> [Pad019]
  ExternalGeometry = -> [Binder]
  FullyConstrained = true
  MakeInternals = false
  MapMode = 5
  Placement = pos=(0,2,0) rot=(0,0.707107,0.707107;3.14159rad)
  sketch-geometry (12):
    g0: Circle CenterX=5.6 CenterY=34.8 CenterZ=0 NormalX=0 NormalY=0 NormalZ=1 AngleXU=0 Radius=1.8
    g1: Circle CenterX=5.6 CenterY=7.6 CenterZ=0 NormalX=0 NormalY=0 NormalZ=1 AngleXU=0 Radius=1.8
    g2: Circle CenterX=78.51 CenterY=34.8 CenterZ=0 NormalX=0 NormalY=0 NormalZ=1 AngleXU=0 Radius=1.8
    g3: Circle CenterX=78.51 CenterY=7.6 CenterZ=0 NormalX=0 NormalY=0 NormalZ=1 AngleXU=0 Radius=1.8
    g4: LineSegment StartX=0 StartY=39.2 StartZ=0 EndX=0 EndY=3.2 EndZ=0
    g5: LineSegment StartX=0 StartY=3.2 StartZ=0 EndX=82.8 EndY=3.2 EndZ=0
    g6: LineSegment StartX=82.8 StartY=3.2 StartZ=0 EndX=82.8 EndY=39.2 EndZ=0
    g7: LineSegment StartX=82.8 StartY=39.2 StartZ=0 EndX=0 EndY=39.2 EndZ=0
    g8: ArcOfCircle CenterX=19 CenterY=21.2 CenterZ=0 NormalX=0 NormalY=0 NormalZ=1 AngleXU=0 Radius=10 StartAngle=1.5708 EndAngle=4.71239
    g9: ArcOfCircle CenterX=65 CenterY=21.2 CenterZ=0 NormalX=0 NormalY=0 NormalZ=1 AngleXU=0 Radius=10 StartAngle=4.71239 EndAngle=7.85398
    g10: LineSegment StartX=19 StartY=31.2 StartZ=0 EndX=65 EndY=31.2 EndZ=0
    g11: LineSegment StartX=19 StartY=11.2 StartZ=0 EndX=65 EndY=11.2 EndZ=0
  constraints (25):
    c: Equal(g2,g-7)
    c: Equal(g3,g-8)
    c: Equal(g1,g-13)
    c: Equal(g0,g-12)
    c: Coincident(g0,g-12)
    c: Coincident(g1,g-13)
    c: Coincident(g3,g-8)
    c: Coincident(g2,g-7)
    c: Coincident(g4,g-4)
    c: Coincident(g4,g-5)
    c: Coincident(g5,g4)
    c: Coincident(g5,g-6)
    c: Coincident(g6,g5)
    c: PointOnObject(g6,g-3)
    c: Vertical(g6)
    c: Coincident(g7,g6)
    c: Coincident(g7,g4)
    c: Tangent(g8,g10) = 1.5708
    c: Tangent(g8,g11) = -1.5708
    c: Tangent(g9,g10) = 1.5708
    c: Tangent(g9,g11) = -1.5708
    c: Equal(g8,g9)
    c: Radius(g8) = 10
    c: Coincident(g8,g-11)
    c: Coincident(g9,g-9)
FEATURE [Sketcher::SketchObject] Sketch093  label="Sketch093 - scavi interni pulsanti"
  ArcFitTolerance = 1e-06
  AttachmentSupport = -> [Pad019]
  ExternalGeometry = -> [Binder]
  FullyConstrained = true
  MakeInternals = false
  MapMode = 5
  Placement = pos=(0,1.8e-15,0) rot=(1,0,0;1.5708rad)
  sketch-geometry (3):
    g0: Circle CenterX=-65 CenterY=21.2 CenterZ=0 NormalX=0 NormalY=0 NormalZ=1 AngleXU=0 Radius=7.3
    g1: Circle CenterX=-42 CenterY=21.2 CenterZ=0 NormalX=0 NormalY=0 NormalZ=1 AngleXU=0 Radius=7.3
    g2: Circle CenterX=-19 CenterY=21.2 CenterZ=0 NormalX=0 NormalY=0 NormalZ=1 AngleXU=0 Radius=7.3
  constraints (6):
    c: Coincident(g0,g-3)
    c: Coincident(g1,g-4)
    c: Coincident(g2,g-5)
    c: Diameter(g0) = 14.6
    c: Diameter(g1) = 14.6
    c: Diameter(g2) = 14.6
FEATURE [Sketcher::SketchObject] Sketch094  label="Sketch094 - forma centrale"
  ArcFitTolerance = 1e-06
  AttachmentSupport = -> [Pad019]
  ExternalGeometry = -> [Binder]
  FullyConstrained = true
  MakeInternals = false
  MapMode = 5
  Placement = pos=(0,2,0) rot=(0,0.707107,0.707107;3.14159rad)
  sketch-geometry (4):
    g0: LineSegment StartX=137.815 StartY=39.2 StartZ=0 EndX=142.655 EndY=24.303 EndZ=0
    g1: LineSegment StartX=110.815 StartY=24.303 StartZ=0 EndX=142.655 EndY=24.303 EndZ=0
    g2: LineSegment StartX=137.815 StartY=39.2 StartZ=0 EndX=110.815 EndY=39.2 EndZ=0
    g3: ArcOfCircle CenterX=92.2534 CenterY=31.7515 CenterZ=0 NormalX=0 NormalY=0 NormalZ=1 AngleXU=0 Radius=20 StartAngle=5.90156 EndAngle=6.66481
  constraints (12):
    c: PointOnObject(g0,g-3)
    c: Tangent(g0,g-5)
    c: Horizontal(g1)
    c: Coincident(g1,g0)
    c: Coincident(g2,g0)
    c: PointOnObject(g2,g-3)
    c: DistanceX(g2,g2) = 27
    c: Vertical(g1,g2)
    c: Coincident(g3,g2)
    c: Radius(g3) = 20
    c: Coincident(g3,g1)
    c: DistanceY(g-6,g0) = 4
FEATURE [Sketcher::SketchObject] Sketch095  label="Sketch095 - forma posteriore"
  ArcFitTolerance = 1e-06
  AttachmentSupport = -> [Pad019]
  ExternalGeometry = -> [Binder]
  FullyConstrained = true
  MakeInternals = false
  MapMode = 5
  Placement = pos=(0,2,0) rot=(0,0.707107,0.707107;3.14159rad)
  sketch-geometry (15):
    g0: LineSegment StartX=137.815 StartY=39.2 StartZ=0 EndX=143.955 EndY=20.303 EndZ=0
    g1: LineSegment StartX=143.955 StartY=20.303 StartZ=0 EndX=190.141 EndY=20.303 EndZ=0
    g2: ArcOfCircle CenterX=184.08 CenterY=34.8 CenterZ=0 NormalX=0 NormalY=0 NormalZ=1 AngleXU=0 Radius=3.5 StartAngle=3.49066 EndAngle=4.71239
    g3: LineSegment StartX=180.791 StartY=33.6029 StartZ=0 EndX=178.754 EndY=39.2 EndZ=0
    g4: LineSegment StartX=184.08 StartY=31.3 StartZ=0 EndX=186.139 EndY=31.3 EndZ=0
    g5: LineSegment StartX=190.141 StartY=20.303 StartZ=0 EndX=186.139 EndY=31.3 EndZ=0
    g6: LineSegment StartX=137.815 StartY=39.2 StartZ=0 EndX=156.815 EndY=39.2 EndZ=0
    g7: LineSegment StartX=178.754 StartY=39.2 StartZ=0 EndX=168.815 EndY=39.2 EndZ=0
    g8: LineSegment StartX=156.815 StartY=31.2 StartZ=0 EndX=168.815 EndY=31.2 EndZ=0
    g9: ArcOfCircle CenterX=176.411 CenterY=35.2 CenterZ=0 NormalX=0 NormalY=0 NormalZ=1 AngleXU=0 Radius=20 StartAngle=2.94023 EndAngle=3.34295
    g10: ArcOfCircle CenterX=188.411 CenterY=35.2 CenterZ=0 NormalX=0 NormalY=0 NormalZ=1 AngleXU=0 Radius=20 StartAngle=2.94023 EndAngle=3.34295
    g11: LineSegment StartX=157.815 StartY=39.2 StartZ=0 EndX=167.815 EndY=39.2 EndZ=0
    g12: LineSegment StartX=157.436 StartY=36.2 StartZ=0 EndX=167.436 EndY=36.2 EndZ=0
    g13: ArcOfCircle CenterX=177.411 CenterY=35.2 CenterZ=0 NormalX=0 NormalY=0 NormalZ=1 AngleXU=0 Radius=20 StartAngle=2.94023 EndAngle=3.09157
    g14: ArcOfCircle CenterX=187.411 CenterY=35.2 CenterZ=0 NormalX=0 NormalY=0 NormalZ=1 AngleXU=0 Radius=20 StartAngle=2.94023 EndAngle=3.09157
  constraints (46):
    c: PointOnObject(g0,g-3)
    c: Tangent(g0,g-6)
    c: Coincident(g1,g0)
    c: Horizontal(g1)
    c: Radius(g2) = 3.5
    c: Coincident(g2,g-5)
    c: PointOnObject(g3,g-3)
    c: Parallel(g3,g-4)
    c: Tangent(g3,g2) = 1.5708
    c: Horizontal(g4)
    c: Tangent(g4,g2) = -1.5708
    c: Coincident(g5,g1)
    c: Parallel(g5,g-4)
    c: Coincident(g5,g4)
    c: DistanceX(g4,g-8) = 3.8
    c: Coincident(g6,g0)
    c: PointOnObject(g6,g-3)
    c: Coincident(g7,g3)
    c: PointOnObject(g7,g-3)
    c: Horizontal(g8)
    c: DistanceX(g6,g7) = 12
    c: Vertical(g8,g6)
    c: Vertical(g7,g8)
    c: DistanceY(g8,g6) = 8
    c: Coincident(g9,g8)
    c: Coincident(g9,g6)
    c: Coincident(g10,g7)
    c: Coincident(g10,g8)
    c: Radius(g9) = 20
    c: Radius(g10) = 20
    c: PointOnObject(g11,g-3)
    c: PointOnObject(g11,g-3)
    c: DistanceX(g11,g11) = 10
    c: DistanceX(g6,g11) = 1
    c: Horizontal(g12)
    c: Equal(g12,g11)
    c: DistanceY(g12,g11) = 3
    c: Coincident(g13,g11)
    c: Coincident(g13,g12)
    c: Radius(g13) = 20
    c: Coincident(g14,g11)
    c: Coincident(g14,g12)
    c: Radius(g14) = 20
    c: DistanceX(g0,g6) = 19
    c: Horizontal(g9,g13)
    c: Horizontal(g0,g-4)
FEATURE [Sketcher::SketchObject] Sketch096  label="Sketch096 - forma impugnatura"
  ArcFitTolerance = 1e-06
  AttachmentSupport = -> [Pad019]
  ExternalGeometry = -> [Binder]
  FullyConstrained = true
  MakeInternals = false
  MapMode = 5
  Placement = pos=(0,2,0) rot=(0,0.707107,0.707107;3.14159rad)
  sketch-geometry (8):
    g0: LineSegment StartX=176.685 StartY=-80.4316 StartZ=0 EndX=143.955 EndY=20.303 EndZ=0
    g1: LineSegment StartX=176.685 StartY=-80.4316 StartZ=0 EndX=215.932 EndY=-80.4316 EndZ=0
    g2: Circle CenterX=179.305 CenterY=-76.8316 CenterZ=0 NormalX=0 NormalY=0 NormalZ=1 AngleXU=0 Radius=3
    g3: Circle CenterX=213.443 CenterY=-76.8316 CenterZ=0 NormalX=0 NormalY=0 NormalZ=1 AngleXU=0 Radius=3
    g4: LineSegment StartX=143.955 StartY=20.303 StartZ=0 EndX=202.765 EndY=20.303 EndZ=0
    g5: LineSegment StartX=215.42 StartY=-53.0314 StartZ=0 EndX=192.176 EndY=-3.18451 EndZ=0
    g6: ArcOfCircle CenterX=184.801 CenterY=-67.3089 CenterZ=0 NormalX=0 NormalY=0 NormalZ=1 AngleXU=0 Radius=33.7833 StartAngle=5.88425 EndAngle=6.71952
    g7: ArcOfCircle CenterX=207.583 CenterY=4 CenterZ=0 NormalX=0 NormalY=0 NormalZ=1 AngleXU=0 Radius=17 StartAngle=1.85815 EndAngle=3.57792
  constraints (19):
    c: Coincident(g0,g-4)
    c: PointOnObject(g0,g-3)
    c: Horizontal(g0,g-7)
    c: Coincident(g1,g0)
    c: Coincident(g1,g-5)
    c: Diameter(g2) = 6
    c: Diameter(g3) = 6
    c: Coincident(g2,g-9)
    c: Coincident(g3,g-10)
    c: Coincident(g4,g0)
    c: Coincident(g5,g-6)
    c: Coincident(g6,g1)
    c: Coincident(g6,g5)
    c: Equal(g-5,g6)
    c: Coincident(g5,g-7)
    c: Coincident(g4,g-7)
    c: Tangent(g7,g-7)
    c: Coincident(g7,g4)
    c: Coincident(g7,g5)
FEATURE [Sketcher::SketchObject] Sketch097
  ArcFitTolerance = 1e-06
  AttachmentSupport = -> [Pad019]
  ExternalGeometry = -> [Binder]
  FullyConstrained = true
  MakeInternals = false
  MapMode = 5
  Placement = pos=(0,2,0) rot=(0,0.707107,0.707107;3.14159rad)
  sketch-geometry (4):
    g0: LineSegment StartX=90 StartY=36.8 StartZ=0 EndX=108 EndY=36.8 EndZ=0
    g1: LineSegment StartX=108 StartY=36.8 StartZ=0 EndX=108 EndY=26.8 EndZ=0
    g2: LineSegment StartX=108 StartY=26.8 StartZ=0 EndX=90 EndY=26.8 EndZ=0
    g3: ArcOfCircle CenterX=94 CenterY=31.8 CenterZ=0 NormalX=0 NormalY=0 NormalZ=1 AngleXU=0 Radius=6.40312 StartAngle=2.24554 EndAngle=4.03765
  constraints (13):
    c: Horizontal(g0)
    c: Coincident(g1,g0)
    c: Vertical(g1)
    c: DistanceX(g0,g0) = 18
    c: DistanceY(g1,g1) = 10
    c: Coincident(g2,g1)
    c: Horizontal(g2)
    c: Equal(g2,g0)
    c: DistanceY(g0,g-3) = 2.4
    c: Coincident(g3,g0)
    c: Coincident(g3,g2)
    c: DistanceX(g2,g3) = 4
    c: DistanceX(g-3,g0) = 90
FEATURE [PartDesign::Chamfer] Chamfer015
  Angle = 45
  Base = -> Pad019 [Edge19,Edge22,Edge79]
  BaseFeature = -> Pad019
  ChamferType = 0
  FlipDirection = false
  Refine = true
  Size = 1.9
  Size2 = 1
  SupportTransform = false
  Suppressed = false
  UseAllEdges = false
FEATURE [PartDesign::Pocket] Pocket002
  BaseFeature = -> Chamfer015
  Direction = (0,1,-2e-16)
  Length = 1.2
  Length2 = 5
  Profile = -> Sketch093
  ReferenceAxis = -> Sketch093 [N_Axis]
  Refine = true
  Suppressed = false
  Type = 0
FEATURE [PartDesign::Pad] Pad005
  BaseFeature = -> Pocket002
  Direction = (0,1,-2e-16)
  Length = 1.6
  Length2 = 10
  Profile = -> Sketch091
  ReferenceAxis = -> Sketch091 [N_Axis]
  Refine = true
  Suppressed = false
  Type = 0
FEATURE [Sketcher::SketchObject] Sketch092  label="Sketch092 - scavi per viti anteriori"
  ArcFitTolerance = 1e-06
  AttachmentSupport = -> [Pad005]
  ExternalGeometry = -> [Binder]
  FullyConstrained = true
  MakeInternals = false
  MapMode = 5
  Placement = pos=(0,3.6,0) rot=(0,0.707107,0.707107;3.14159rad)
  sketch-geometry (20):
    g0: ArcOfCircle CenterX=5.6 CenterY=7.6 CenterZ=0 NormalX=0 NormalY=0 NormalZ=1 AngleXU=0 Radius=3.5 StartAngle=0 EndAngle=1.5708
    g1: ArcOfCircle CenterX=5.6 CenterY=34.8 CenterZ=0 NormalX=0 NormalY=0 NormalZ=1 AngleXU=0 Radius=3.5 StartAngle=4.71239 EndAngle=6.28319
    g2: ArcOfCircle CenterX=78.51 CenterY=34.8 CenterZ=0 NormalX=0 NormalY=0 NormalZ=1 AngleXU=0 Radius=3.5 StartAngle=3.14159 EndAngle=4.71239
    g3: ArcOfCircle CenterX=78.51 CenterY=7.6 CenterZ=0 NormalX=0 NormalY=0 NormalZ=1 AngleXU=0 Radius=3.5 StartAngle=1.5708 EndAngle=3.14159
    g4: LineSegment StartX=0 StartY=3.2 StartZ=0 EndX=0 EndY=11.1 EndZ=0
    g5: LineSegment StartX=0 StartY=11.1 StartZ=0 EndX=5.6 EndY=11.1 EndZ=0
    g6: LineSegment StartX=0 StartY=3.2 StartZ=0 EndX=9.1 EndY=3.2 EndZ=0
    g7: LineSegment StartX=9.1 StartY=3.2 StartZ=0 EndX=9.1 EndY=7.6 EndZ=0
    g8: LineSegment StartX=0 StartY=39.2 StartZ=0 EndX=0 EndY=31.3 EndZ=0
    g9: LineSegment StartX=0 StartY=31.3 StartZ=0 EndX=5.6 EndY=31.3 EndZ=0
    g10: LineSegment StartX=0 StartY=39.2 StartZ=0 EndX=9.1 EndY=39.2 EndZ=0
    g11: LineSegment StartX=9.1 StartY=39.2 StartZ=0 EndX=9.1 EndY=34.8 EndZ=0
    g12: LineSegment StartX=82.8 StartY=39.2 StartZ=0 EndX=75.01 EndY=39.2 EndZ=0
    g13: LineSegment StartX=82.8 StartY=39.2 StartZ=0 EndX=82.8 EndY=31.3 EndZ=0
    g14: LineSegment StartX=82.8 StartY=31.3 StartZ=0 EndX=78.51 EndY=31.3 EndZ=0
    g15: LineSegment StartX=82.8 StartY=3.2 StartZ=0 EndX=75.01 EndY=3.2 EndZ=0
    g16: LineSegment StartX=75.01 StartY=3.2 StartZ=0 EndX=75.01 EndY=7.6 EndZ=0
    g17: LineSegment StartX=82.8 StartY=3.2 StartZ=0 EndX=82.8 EndY=11.1 EndZ=0
    g18: LineSegment StartX=82.8 StartY=11.1 StartZ=0 EndX=78.51 EndY=11.1 EndZ=0
    g19: LineSegment StartX=75.01 StartY=39.2 StartZ=0 EndX=75.01 EndY=34.8 EndZ=0
  constraints (48):
    c: Radius(g0) = 3.5
    c: Coincident(g0,g-10)
    c: Radius(g1) = 3.5
    c: Coincident(g1,g-9)
    c: Radius(g2) = 3.5
    c: Coincident(g2,g-8)
    c: Radius(g3) = 3.5
    c: Coincident(g3,g-7)
    c: Coincident(g4,g-5)
    c: PointOnObject(g4,g-4)
    c: Coincident(g5,g4)
    c: Horizontal(g5)
    c: Coincident(g6,g4)
    c: PointOnObject(g6,g-5)
    c: Coincident(g7,g6)
    c: Vertical(g7)
    c: Coincident(g8,g-4)
    c: PointOnObject(g8,g-4)
    c: Coincident(g9,g8)
    c: Horizontal(g9)
    c: Coincident(g10,g8)
    c: PointOnObject(g10,g-3)
    c: Coincident(g11,g10)
    c: Vertical(g11)
    c: PointOnObject(g12,g-3)
    c: PointOnObject(g12,g-3)
    c: Coincident(g13,g12)
    c: Vertical(g13)
    c: Coincident(g14,g13)
    c: Horizontal(g14)
    c: Coincident(g15,g-6)
    c: PointOnObject(g15,g-5)
    c: Coincident(g16,g15)
    c: Vertical(g16)
    c: Coincident(g17,g15)
    c: Coincident(g18,g17)
    c: Horizontal(g18)
    c: Tangent(g3,g18) = -1.5708
    c: Tangent(g16,g3) = 1.5708
    c: Coincident(g19,g12)
    c: Vertical(g19)
    c: Tangent(g2,g19) = -1.5708
    c: Tangent(g2,g14) = 1.5708
    c: Tangent(g0,g7) = -1.5708
    c: Tangent(g0,g5) = 1.5708
    c: Tangent(g9,g1) = -1.5708
    c: Tangent(g1,g11) = 1.5708
    c: Tangent(g17,g13)
FEATURE [PartDesign::Pocket] Pocket001
  BaseFeature = -> Pad005
  Direction = (0,-1,2e-16)
  Length = 1.6
  Length2 = 5
  Profile = -> Sketch092
  ReferenceAxis = -> Sketch092 [N_Axis]
  Refine = true
  Suppressed = false
  Type = 0
FEATURE [PartDesign::Pad] Pad006
  BaseFeature = -> Pocket001
  Direction = (0,1,-2e-16)
  Length = 0.8
  Length2 = 10
  Profile = -> Sketch094
  ReferenceAxis = -> Sketch094 [N_Axis]
  Refine = true
  Suppressed = false
  Type = 0
FEATURE [PartDesign::Pad] Pad007
  BaseFeature = -> Pad006
  Direction = (0,1,-2e-16)
  Length = 2
  Length2 = 10
  Profile = -> Sketch095
  ReferenceAxis = -> Sketch095 [N_Axis]
  Refine = true
  Suppressed = false
  Type = 0
FEATURE [PartDesign::Pad] Pad008  label="Pad008 - forma impugnatura"
  BaseFeature = -> Pad007
  Direction = (0,1,-2e-16)
  Length = 1.6
  Length2 = 10
  Profile = -> Sketch096
  ReferenceAxis = -> Sketch096 [N_Axis]
  Refine = true
  Suppressed = false
  Type = 0
FEATURE [PartDesign::Pad] Pad009
  BaseFeature = -> Pad008
  Direction = (0,1,-2e-16)
  Length = 1.6
  Length2 = 10
  Profile = -> Sketch097
  ReferenceAxis = -> Sketch097 [N_Axis]
  Refine = true
  Suppressed = false
  Type = 0
FEATURE [Sketcher::SketchObject] Sketch098
  ArcFitTolerance = 1e-06
  AttachmentSupport = -> [Pad006]
  ExternalGeometry = -> [Binder]
  FullyConstrained = true
  MakeInternals = false
  MapMode = 5
  Placement = pos=(0,2.8,-7e-16) rot=(0,0.707107,0.707107;3.14159rad)
  sketch-geometry (4):
    g0: LineSegment StartX=118 StartY=39.2 StartZ=0 EndX=129 EndY=39.2 EndZ=0
    g1: LineSegment StartX=120.599 StartY=31.2 StartZ=0 EndX=131.599 EndY=31.2 EndZ=0
    g2: LineSegment StartX=129 StartY=39.2 StartZ=0 EndX=131.599 EndY=31.2 EndZ=0
    g3: LineSegment StartX=118 StartY=39.2 StartZ=0 EndX=120.599 EndY=31.2 EndZ=0
  constraints (12):
    c: PointOnObject(g0,g-3)
    c: PointOnObject(g0,g-3)
    c: DistanceX(g0,g0) = 11
    c: Horizontal(g1)
    c: Equal(g1,g0)
    c: Coincident(g2,g0)
    c: Coincident(g3,g0)
    c: Parallel(g-4,g2)
    c: Coincident(g1,g2)
    c: Coincident(g1,g3)
    c: DistanceY(g1,g0) = 8
    c: DistanceX(g-3,g0) = 118
FEATURE [Sketcher::SketchObject] Sketch099
  ArcFitTolerance = 1e-06
  AttachmentSupport = -> [Pad008]
  ExternalGeometry = -> [Binder]
  FullyConstrained = true
  MakeInternals = false
  MapMode = 5
  Placement = pos=(0,3.6,0) rot=(0,0.707107,0.707107;3.14159rad)
  sketch-geometry (13):
    g0: LineSegment StartX=192.176 StartY=-3.18451 StartZ=0 EndX=196.804 EndY=-13.1108 EndZ=0
    g1: LineSegment [constr] StartX=202.765 StartY=20.303 StartZ=0 EndX=181.223 EndY=20.303 EndZ=0
    g2: LineSegment [constr] StartX=181.223 StartY=20.303 StartZ=0 EndX=181.223 EndY=-3.18451 EndZ=0
    g3: ArcOfCircle CenterX=181.223 CenterY=-20.3764 CenterZ=0 NormalX=0 NormalY=0 NormalZ=1 AngleXU=0 Radius=17.1918 StartAngle=0.436332 EndAngle=1.57079
    g4: ArcOfEllipse CenterX=181.223 CenterY=8.55923 CenterZ=0 NormalX=0 NormalY=0 NormalZ=1 MajorRadius=23.4779 MinorRadius=11.7437 AngleXU=0 StartAngle=1.5708 EndAngle=4.71239
    g5: LineSegment [constr] StartX=204.701 StartY=8.55923 StartZ=0 EndX=157.745 EndY=8.55923 EndZ=0
    g6: LineSegment [constr] StartX=181.223 StartY=20.303 StartZ=0 EndX=181.223 EndY=-3.18451 EndZ=0
    g7: GeomPoint [constr] X=201.553 Y=8.55923 Z=0
    g8: GeomPoint [constr] X=160.894 Y=8.55923 Z=0
    g9: GeomPoint [constr] X=181.223 Y=-3.18451 Z=0
    g10: LineSegment StartX=181.223 StartY=20.303 StartZ=0 EndX=202.765 EndY=20.303 EndZ=0
    g11: ArcOfCircle CenterX=207.583 CenterY=4 CenterZ=0 NormalX=0 NormalY=0 NormalZ=1 AngleXU=0 Radius=17 StartAngle=1.85815 EndAngle=3.57792
    g12: LineSegment [constr] StartX=172.411 StartY=39.2 StartZ=0 EndX=192.176 EndY=-3.18451 EndZ=0
  constraints (27):
    c: Coincident(g1,g-7)
    c: Horizontal(g1)
    c: Coincident(g2,g1)
    c: Vertical(g2)
    c: Horizontal(g2,g0)
    c: Coincident(g3,g0)
    c: Coincident(g3,g2)
    c: InternalAlignment(g5-g8 -> g4) x4
    c: Horizontal(g5)
    c: PointOnObject(g4,g2)
    c: Coincident(g4,g1)
    c: DistanceX(g-3,g5) = 10.1
    c: Coincident(g4,g2)
    c: Tangent(g3,g-5)
    c: PointOnObject(g9,g4)
    c: PointOnObject(g9,g3)
    c: Tangent(g4,g3,g9) = 1.5708
    c: Coincident(g10,g1)
    c: Coincident(g10,g1)
    c: Equal(g11,g-4)
    c: Coincident(g11,g1)
    c: Coincident(g11,g0)
    c: PointOnObject(g12,g-6)
    c: PointOnObject(g1,g12)
    c: Tangent(g12,g-5) = -1.5708
    c: Tangent(g0,g-5) = -1.5708
    c: Horizontal(g9,g12)
FEATURE [Sketcher::SketchObject] Sketch106  label="Sketch106 - smusso impuniatura interno"
  ArcFitTolerance = 1e-06
  AttachmentSupport = -> [Pad008]
  ExternalGeometry = -> [Pad008]
  FullyConstrained = true
  MakeInternals = false
  MapMode = 5
  Placement = pos=(0,-1.585e-13,-80.4316) rot=(1,0,0;3.14159rad)
  sketch-geometry (9):
    g0: LineSegment StartX=-176.685 StartY=-3.6 StartZ=0 EndX=-176.685 EndY=2.12528e-11 EndZ=0
    g1: LineSegment [constr] StartX=-176.685 StartY=1.79e-14 StartZ=0 EndX=-176.685 EndY=2.12527e-11 EndZ=0
    g2: LineSegment [constr] StartX=-186.685 StartY=-3.6 StartZ=0 EndX=-186.685 EndY=2.12528e-11 EndZ=0
    g3: ArcOfEllipse CenterX=-186.685 CenterY=2.12527e-11 CenterZ=0 NormalX=0 NormalY=0 NormalZ=1 MajorRadius=10 MinorRadius=3.6 AngleXU=-3.14159 StartAngle=1.5708 EndAngle=3.14159
    g4: LineSegment [constr] StartX=-196.685 StartY=1.79e-14 StartZ=0 EndX=-176.685 EndY=1.79e-14 EndZ=0
    g5: LineSegment [constr] StartX=-186.685 StartY=-3.6 StartZ=0 EndX=-186.685 EndY=3.6 EndZ=0
    g6: GeomPoint [constr] X=-196.015 Y=1.55e-14 Z=0
    g7: GeomPoint [constr] X=-177.356 Y=1.85e-14 Z=0
    g8: LineSegment StartX=-176.685 StartY=-3.6 StartZ=0 EndX=-186.685 EndY=-3.6 EndZ=0
  constraints (15):
    c: PointOnObject(g2,g-3)
    c: Coincident(g1,g-5)
    c: DistanceY(g1,g1) = 0
    c: Coincident(g0,g1)
    c: DistanceX(g2,g-5) = 10
    c: Vertical(g2)
    c: Horizontal(g2,g0)
    c: InternalAlignment(g4-g7 -> g3) x4
    c: Coincident(g3,g2)
    c: Horizontal(g4)
    c: Coincident(g3,g0)
    c: Tangent(g0,g-5) = 1.5708
    c: Coincident(g3,g2)
    c: Coincident(g8,g0)
    c: Coincident(g8,g2)
FEATURE [Sketcher::SketchObject] Sketch107  label="Sketch107 - smusso impugnatura esterno"
  ArcFitTolerance = 1e-06
  AttachmentSupport = -> [Pad008]
  ExternalGeometry = -> [Pad008]
  FullyConstrained = true
  MakeInternals = false
  MapMode = 5
  Placement = pos=(0,-1.585e-13,-80.4316) rot=(1,0,0;3.14159rad)
  sketch-geometry (9):
    g0: LineSegment [constr] StartX=-215.932 StartY=1.79e-14 StartZ=0 EndX=-215.932 EndY=2.09e-14 EndZ=0
    g1: LineSegment StartX=-215.932 StartY=-3.6 StartZ=0 EndX=-215.932 EndY=2.09e-14 EndZ=0
    g2: LineSegment StartX=-215.932 StartY=-3.6 StartZ=0 EndX=-205.932 EndY=-3.6 EndZ=0
    g3: LineSegment [constr] StartX=-205.932 StartY=-3.6 StartZ=0 EndX=-205.932 EndY=2.09e-14 EndZ=0
    g4: ArcOfEllipse CenterX=-205.932 CenterY=2.09e-14 CenterZ=0 NormalX=0 NormalY=0 NormalZ=1 MajorRadius=10 MinorRadius=3.6 AngleXU=3.14159 StartAngle=1e-16 EndAngle=1.5708
    g5: LineSegment [constr] StartX=-215.932 StartY=1.79e-14 StartZ=0 EndX=-195.932 EndY=1.79e-14 EndZ=0
    g6: LineSegment [constr] StartX=-205.932 StartY=-3.6 StartZ=0 EndX=-205.932 EndY=3.6 EndZ=0
    g7: GeomPoint [constr] X=-215.262 Y=2.14e-14 Z=0
    g8: GeomPoint [constr] X=-196.602 Y=1.78e-14 Z=0
  constraints (16):
    c: Coincident(g0,g-6)
    c: PointOnObject(g0,g-6)
    c: DistanceY(g0,g0) = 0
    c: Coincident(g1,g-6)
    c: Coincident(g1,g0)
    c: Tangent(g2,g-3)
    c: DistanceX(g2,g2) = 10
    c: Coincident(g3,g2)
    c: Vertical(g3)
    c: Horizontal(g3,g0)
    c: InternalAlignment(g5-g8 -> g4) x4
    c: Coincident(g4,g3)
    c: Horizontal(g5)
    c: Coincident(g4,g0)
    c: Coincident(g4,g2)
    c: PointOnObject(g2,g1)
FEATURE [Sketcher::SketchObject] Sketch108
  ArcFitTolerance = 1e-06
  AttachmentOffset = pos=(0,0,-1.6) rot=(0,0,1;0rad)
  AttachmentSupport = -> [Pad008]
  ExternalGeometry = -> [Binder]
  FullyConstrained = true
  MakeInternals = false
  MapMode = 5
  Placement = pos=(0,2,4e-16) rot=(0,0.707107,0.707107;3.14159rad)
  sketch-geometry (14):
    g0: LineSegment StartX=192.176 StartY=-3.18451 StartZ=0 EndX=193.827 EndY=-6.72678 EndZ=0
    g1: LineSegment [constr] StartX=202.765 StartY=20.303 StartZ=0 EndX=181.223 EndY=20.303 EndZ=0
    g2: LineSegment [constr] StartX=181.223 StartY=20.303 StartZ=0 EndX=181.223 EndY=1.30297 EndZ=0
    g3: ArcOfCircle CenterX=181.223 CenterY=-12.6042 CenterZ=0 NormalX=0 NormalY=0 NormalZ=1 AngleXU=0 Radius=13.9072 StartAngle=0.436332 EndAngle=1.5708
    g4: ArcOfEllipse CenterX=181.223 CenterY=10.803 CenterZ=0 NormalX=0 NormalY=0 NormalZ=1 MajorRadius=14.4779 MinorRadius=9.5 AngleXU=0 StartAngle=1.5708 EndAngle=4.71239
    g5: LineSegment [constr] StartX=195.701 StartY=10.803 StartZ=0 EndX=166.745 EndY=10.803 EndZ=0
    g6: LineSegment [constr] StartX=181.223 StartY=20.303 StartZ=0 EndX=181.223 EndY=1.30297 EndZ=0
    g7: GeomPoint [constr] X=192.148 Y=10.803 Z=0
    g8: GeomPoint [constr] X=170.298 Y=10.803 Z=0
    g9: LineSegment StartX=181.223 StartY=20.303 StartZ=0 EndX=202.765 EndY=20.303 EndZ=0
    g10: ArcOfCircle CenterX=207.583 CenterY=4 CenterZ=0 NormalX=0 NormalY=0 NormalZ=1 AngleXU=0 Radius=17 StartAngle=1.85815 EndAngle=3.57792
    g11: LineSegment [constr] StartX=172.411 StartY=39.2 StartZ=0 EndX=192.176 EndY=-3.18451 EndZ=0
    g12: GeomPoint [constr] X=181.223 Y=1.30297 Z=0
    g13: GeomPoint [constr] X=181.223 Y=1.30297 Z=0
  constraints (28):
    c: Coincident(g1,g-7)
    c: Horizontal(g1)
    c: Coincident(g2,g1)
    c: Vertical(g2)
    c: Coincident(g3,g2)
    c: InternalAlignment(g5-g8 -> g4) x4
    c: Horizontal(g5)
    c: PointOnObject(g4,g2)
    c: Coincident(g4,g1)
    c: DistanceX(g-3,g5) = 19.1
    c: Coincident(g4,g2)
    c: Coincident(g9,g1)
    c: Coincident(g9,g1)
    c: Coincident(g10,g1)
    c: Coincident(g10,g0)
    c: PointOnObject(g11,g-6)
    c: PointOnObject(g1,g11)
    c: DistanceY(g2,g1) = 19
    c: Coincident(g10,g-4)
    c: PointOnObject(g12,g4)
    c: PointOnObject(g12,g3)
    c: Tangent(g11,g-5) = -1.5708
    c: Tangent(g0,g-5) = -1.5708
    c: Tangent(g3,g0) = 1.5708
    c: PointOnObject(g13,g4)
    c: PointOnObject(g13,g3)
    c: Tangent(g4,g3,g13) = 1.5708
    c: Horizontal(g11,g0)
FEATURE [Part::Part2DObjectPython] Clone2D  label="Sketch108 (2D)"  # Draft 2D object (typed FeaturePython)
  Fuse = false
  Objects = -> [Sketch108]
  Placement = pos=(0,2,4e-16) rot=(0,0.707107,0.707107;3.14159rad)
  Scale = (1,1,1)
FEATURE [Sketcher::SketchObject] Sketch109
  ArcFitTolerance = 1e-06
  AttachmentOffset = pos=(0,0,-3.5) rot=(0,0,1;0rad)
  AttachmentSupport = -> [Pad008]
  ExternalGeometry = -> [Binder]
  FullyConstrained = true
  MakeInternals = false
  MapMode = 5
  Placement = pos=(0,0.1,8e-16) rot=(0,0.707107,0.707107;3.14159rad)
  sketch-geometry (1):
    g0: GeomPoint X=197.47 Y=8.55923 Z=0
  constraints (1):
    c: Symmetric(g-7,g-5,g0)
FEATURE [PartDesign::Chamfer] Chamfer005
  Angle = 45
  Base = -> Pad009 [Edge215,Edge212]
  BaseFeature = -> Pad009
  ChamferType = 1
  FlipDirection = false
  Refine = true
  Size = 1.5
  Size2 = 2.8
  SupportTransform = false
  Suppressed = false
  UseAllEdges = false
FEATURE [Sketcher::SketchObject] Sketch111
  ArcFitTolerance = 1e-06
  AttachmentSupport = -> [Pad009]
  ExternalGeometry = -> [Pad009]
  FullyConstrained = true
  MakeInternals = false
  MapMode = 5
  Placement = pos=(0,3.6,-8e-16) rot=(0,0.707107,0.707107;3.14159rad)
  sketch-geometry (21):
    g0: LineSegment [constr] StartX=97 StartY=36.8 StartZ=0 EndX=97 EndY=26.8 EndZ=0
    g1: LineSegment StartX=97 StartY=28.6 StartZ=0 EndX=97 EndY=27.8 EndZ=0
    g2: LineSegment StartX=97 StartY=27.8 StartZ=0 EndX=108 EndY=27.8 EndZ=0
    g3: LineSegment StartX=108 StartY=27.8 StartZ=0 EndX=108 EndY=28.6 EndZ=0
    g4: LineSegment StartX=108 StartY=28.6 StartZ=0 EndX=97 EndY=28.6 EndZ=0
    g5: LineSegment StartX=97 StartY=35.8 StartZ=0 EndX=97 EndY=35 EndZ=0
    g6: LineSegment StartX=97 StartY=35 StartZ=0 EndX=108 EndY=35 EndZ=0
    g7: LineSegment StartX=108 StartY=35 StartZ=0 EndX=108 EndY=35.8 EndZ=0
    g8: LineSegment StartX=108 StartY=35.8 StartZ=0 EndX=97 EndY=35.8 EndZ=0
    g9: LineSegment StartX=97 StartY=30.4 StartZ=0 EndX=97 EndY=29.6 EndZ=0
    g10: LineSegment StartX=97 StartY=29.6 StartZ=0 EndX=108 EndY=29.6 EndZ=0
    g11: LineSegment StartX=108 StartY=29.6 StartZ=0 EndX=108 EndY=30.4 EndZ=0
    g12: LineSegment StartX=108 StartY=30.4 StartZ=0 EndX=97 EndY=30.4 EndZ=0
    g13: LineSegment StartX=97 StartY=34 StartZ=0 EndX=97 EndY=33.2 EndZ=0
    g14: LineSegment StartX=97 StartY=33.2 StartZ=0 EndX=108 EndY=33.2 EndZ=0
    g15: LineSegment StartX=108 StartY=33.2 StartZ=0 EndX=108 EndY=34 EndZ=0
    g16: LineSegment StartX=108 StartY=34 StartZ=0 EndX=97 EndY=34 EndZ=0
    g17: LineSegment StartX=97 StartY=32.2 StartZ=0 EndX=97 EndY=31.4 EndZ=0
    g18: LineSegment StartX=97 StartY=31.4 StartZ=0 EndX=108 EndY=31.4 EndZ=0
    g19: LineSegment StartX=108 StartY=31.4 StartZ=0 EndX=108 EndY=32.2 EndZ=0
    g20: LineSegment StartX=108 StartY=32.2 StartZ=0 EndX=97 EndY=32.2 EndZ=0
  constraints (54):
    c: Vertical(g0)
    c: PointOnObject(g0,g-3)
    c: PointOnObject(g0,g-4)
    c: DistanceX(g0,g-5) = 11
    c: Coincident(g1,g2)
    c: Coincident(g2,g3)
    c: Coincident(g3,g4)
    c: Coincident(g4,g1)
    c: Horizontal(g2)
    c: Horizontal(g4)
    c: Tangent(g1,g0)
    c: Tangent(g3,g-5)
    c: DistanceY(g2,g3) = 0.8
    c: Coincident(g5,g6)
    c: Coincident(g6,g7)
    c: Coincident(g7,g8)
    c: Coincident(g8,g5)
    c: Horizontal(g6)
    c: Horizontal(g8)
    c: DistanceY(g6,g7) = 0.8
    c: Coincident(g9,g10)
    c: Coincident(g10,g11)
    c: Coincident(g11,g12)
    c: Coincident(g12,g9)
    c: Horizontal(g10)
    c: Horizontal(g12)
    c: DistanceY(g10,g11) = 0.8
    c: Tangent(g5,g0)
    c: Tangent(g7,g-5)
    c: Tangent(g9,g0)
    c: Tangent(g11,g-5)
    c: Coincident(g13,g14)
    c: Coincident(g14,g15)
    c: Coincident(g15,g16)
    c: Coincident(g16,g13)
    c: Horizontal(g14)
    c: Horizontal(g16)
    c: DistanceY(g14,g15) = 0.8
    c: Tangent(g13,g0)
    c: Tangent(g15,g-5)
    c: Coincident(g17,g18)
    c: Coincident(g18,g19)
    c: Coincident(g19,g20)
    c: Coincident(g20,g17)
    c: Horizontal(g18)
    c: Horizontal(g20)
    c: DistanceY(g18,g19) = 0.8
    c: Tangent(g17,g0)
    c: Tangent(g19,g-5)
    c: DistanceY(g1,g9) = 1
    c: DistanceY(g9,g17) = 1
    c: DistanceY(g17,g13) = 1
    c: DistanceY(g13,g5) = 1
    c: DistanceY(g0,g1) = 1
FEATURE [PartDesign::Pocket] Pocket004
  BaseFeature = -> Chamfer005
  Direction = (0,-1,2e-16)
  Length = 1
  Length2 = 5
  Profile = -> Sketch111
  ReferenceAxis = -> Sketch111 [N_Axis]
  Refine = true
  Suppressed = false
  Type = 0
FEATURE [PartDesign::Pad] Pad010
  BaseFeature = -> Pocket004
  Direction = (0,1,-2e-16)
  Length = 1.2
  Length2 = 10
  Profile = -> Sketch098
  ReferenceAxis = -> Sketch098 [N_Axis]
  Refine = true
  Suppressed = false
  Type = 0
FEATURE [PartDesign::Chamfer] Chamfer006
  Angle = 45
  Base = -> Pad010 [Edge291]
  BaseFeature = -> Pad010
  ChamferType = 1
  FlipDirection = false
  Refine = true
  Size = 1
  Size2 = 6
  SupportTransform = false
  Suppressed = false
  UseAllEdges = false
FEATURE [Sketcher::SketchObject] Sketch110
  ArcFitTolerance = 1e-06
  AttachmentSupport = -> [Pad010]
  ExternalGeometry = -> [Sketch098]
  FullyConstrained = true
  MakeInternals = false
  MapMode = 5
  Placement = pos=(0,4,-9e-16) rot=(0,0.707107,0.707107;3.14159rad)
  sketch-geometry (8):
    g0: LineSegment StartX=119.69 StartY=34 StartZ=0 EndX=130.69 EndY=34 EndZ=0
    g1: LineSegment StartX=119.95 StartY=33.2 StartZ=0 EndX=130.95 EndY=33.2 EndZ=0
    g2: LineSegment StartX=119.137 StartY=35.7 StartZ=0 EndX=130.137 EndY=35.7 EndZ=0
    g3: LineSegment StartX=118.877 StartY=36.5 StartZ=0 EndX=129.877 EndY=36.5 EndZ=0
    g4: LineSegment StartX=118.877 StartY=36.5 StartZ=0 EndX=119.137 EndY=35.7 EndZ=0
    g5: LineSegment StartX=129.877 StartY=36.5 StartZ=0 EndX=130.137 EndY=35.7 EndZ=0
    g6: LineSegment StartX=119.69 StartY=34 StartZ=0 EndX=119.95 EndY=33.2 EndZ=0
    g7: LineSegment StartX=130.69 StartY=34 StartZ=0 EndX=130.95 EndY=33.2 EndZ=0
  constraints (24):
    c: Horizontal(g0)
    c: Horizontal(g1)
    c: Horizontal(g2)
    c: Horizontal(g3)
    c: Equal(g1,g-5)
    c: Equal(g0,g-5)
    c: Equal(g2,g-5)
    c: Equal(g3,g-5)
    c: PointOnObject(g0,g-3)
    c: PointOnObject(g1,g-3)
    c: PointOnObject(g2,g-3)
    c: PointOnObject(g3,g-3)
    c: Coincident(g4,g3)
    c: Coincident(g4,g2)
    c: Coincident(g5,g3)
    c: Coincident(g5,g2)
    c: Coincident(g6,g0)
    c: Coincident(g6,g1)
    c: Coincident(g7,g0)
    c: Coincident(g7,g1)
    c: DistanceY(g1,g0) = 0.8
    c: DistanceY(g2,g3) = 0.8
    c: DistanceY(g-5,g1) = 2
    c: DistanceY(g-5,g2) = 4.5
FEATURE [PartDesign::Pocket] Pocket003
  BaseFeature = -> Chamfer006
  Direction = (0,-1,2e-16)
  Length = 1
  Length2 = 5
  Profile = -> Sketch110
  ReferenceAxis = -> Sketch110 [N_Axis]
  Refine = true
  Suppressed = false
  Type = 0
FEATURE [PartDesign::SubtractivePipe] SubtractivePipe
  AuxilleryCurvelinear = true
  AuxillerySpineTangent = false
  BaseFeature = -> Pocket003
  Binormal = (0,0,0)
  Mode = 0
  Profile = -> Sketch106
  Refine = true
  Spine = -> Pad008 [Edge215]
  SpineTangent = false
  Suppressed = false
  Transformation = 0
  Transition = 0
FEATURE [PartDesign::SubtractivePipe] SubtractivePipe001
  AuxilleryCurvelinear = true
  AuxillerySpineTangent = false
  BaseFeature = -> SubtractivePipe
  Binormal = (0,0,0)
  Mode = 0
  Profile = -> Sketch107
  Refine = true
  Spine = -> Pad008 [Edge213,Edge216,Edge210]
  SpineTangent = false
  Suppressed = false
  Transformation = 0
  Transition = 0
FEATURE [PartDesign::SubtractiveLoft] SubtractiveLoft
  BaseFeature = -> SubtractivePipe001
  Closed = false
  Profile = -> Sketch099
  Refine = true
  Ruled = false
  Sections = -> [Sketch108]
  Suppressed = false
FEATURE [PartDesign::SubtractiveLoft] SubtractiveLoft001
  BaseFeature = -> SubtractiveLoft
  Closed = false
  Profile = -> Clone2D
  Refine = true
  Ruled = false
  Sections = -> [Sketch109]
  Suppressed = false
FEATURE [Sketcher::SketchObject] Sketch112
  ArcFitTolerance = 1e-06
  AttachmentSupport = -> [Pad008]
  ExternalGeometry = -> [Binder]
  FullyConstrained = true
  MakeInternals = false
  MapMode = 5
  Placement = pos=(0,3.6,0) rot=(0,0.707107,0.707107;3.14159rad)
  sketch-geometry (4):
    g0: LineSegment [constr] StartX=167.782 StartY=-53.0314 StartZ=0 EndX=215.42 EndY=-53.0314 EndZ=0
    g1: GeomPoint [constr] X=191.282 Y=-53.0314 Z=0
    g2: Circle CenterX=191.282 CenterY=-53.0314 CenterZ=0 NormalX=0 NormalY=0 NormalZ=1 AngleXU=0 Radius=11.5
    g3: Circle CenterX=191.282 CenterY=-53.0314 CenterZ=0 NormalX=0 NormalY=0 NormalZ=1 AngleXU=0 Radius=10.7
  constraints (9):
    c: Horizontal(g0)
    c: PointOnObject(g0,g-3)
    c: Diameter(g2) = 23
    c: Coincident(g2,g1)
    c: Diameter(g3) = 21.4
    c: Coincident(g3,g1)
    c: DistanceX(g0,g1) = 23.5
    c: PointOnObject(g1,g0)
    c: Coincident(g0,g-4)
FEATURE [PartDesign::Chamfer] Chamfer016
  Angle = 45
  Base = -> SubtractiveLoft001 [Edge118,Edge117,Edge119,Edge120,Edge109]
  BaseFeature = -> SubtractiveLoft001
  ChamferType = 0
  FlipDirection = false
  Refine = true
  Size = 1.5
  Size2 = 1
  SupportTransform = false
  Suppressed = false
  UseAllEdges = false
FEATURE [PartDesign::Chamfer] Chamfer017
  Angle = 45
  Base = -> Chamfer016 [Edge15]
  BaseFeature = -> Chamfer016
  ChamferType = 0
  FlipDirection = false
  Refine = true
  Size = 3.5
  Size2 = 1
  SupportTransform = false
  Suppressed = false
  UseAllEdges = false
FEATURE [PartDesign::Chamfer] Chamfer018
  Angle = 45
  Base = -> Chamfer017 [Edge10]
  BaseFeature = -> Chamfer017
  ChamferType = 0
  FlipDirection = false
  Refine = true
  Size = 3.5
  Size2 = 1
  SupportTransform = false
  Suppressed = false
  UseAllEdges = false
FEATURE [PartDesign::Chamfer] Chamfer019
  Angle = 45
  Base = -> Chamfer018 [Edge93,Edge140]
  BaseFeature = -> Chamfer018
  ChamferType = 0
  FlipDirection = false
  Refine = true
  Size = 1.9
  Size2 = 1
  SupportTransform = false
  Suppressed = false
  UseAllEdges = false
FEATURE [PartDesign::Fillet] Fillet009
  Base = -> Chamfer019 [Edge84]
  BaseFeature = -> Chamfer019
  Radius = 1.1
  Refine = true
  SupportTransform = false
  Suppressed = false
  UseAllEdges = false
FEATURE [PartDesign::Fillet] Fillet010
  Base = -> Fillet009 [Edge78]
  BaseFeature = -> Fillet009
  Radius = 1.9
  Refine = true
  SupportTransform = false
  Suppressed = false
  UseAllEdges = false
FEATURE [PartDesign::Pocket] Pocket005
  BaseFeature = -> Fillet010
  Direction = (0,-1,2e-16)
  Length = 0.8
  Length2 = 5
  Profile = -> Sketch112
  ReferenceAxis = -> Sketch112 [N_Axis]
  Refine = true
  Suppressed = false
  Type = 0
FEATURE [Part::Part2DObjectPython] ShapeString001  # Draft 2D object (typed FeaturePython)
  FontFile = <path>
  Fuse = false
  Justification = 6
  JustificationReference = 0
  KeepLeftMargin = false
  MakeFace = true
  ObliqueAngle = 0
  Placement = pos=(-183.5,3.6,-57.5) rot=(0,0.707107,0.707107;3.14159rad)
  ScaleToSize = true
  Size = 10
  String = AS
  Tracking = 0
FEATURE [PartDesign::Pocket] Pocket013
  BaseFeature = -> Pocket005
  Direction = (-1e-16,-1,2e-16)
  Length = 1
  Length2 = 5
  Profile = -> ShapeString001
  ReferenceAxis = -> ShapeString001 [N_Axis]
  Refine = true
  Suppressed = false
  Type = 0
FEATURE [PartDesign::Body] Body006  label="lato SX"
  AllowCompound = false
  Group = -> [Binder,Pad019,Chamfer015,Pocket002,Sketch133,Sketch091,Pad005,Sketch092,Pocket001,Sketch093,Sketch094,Pad006,Sketch095,Pad007,Sketch096,Pad008,Sketch097,Pad009,Chamfer005,Pocket004,Sketch098,Pad010,Chamfer006,Pocket003,SubtractivePipe,SubtractivePipe001,Sketch099,Sketch106,Sketch107,Sketch108,Clone2D,Sketch109,SubtractiveLoft,SubtractiveLoft001,Sketch110,Sketch111,Sketch112,Chamfer016,Chamfer017,+7 more]
  Origin = -> Origin006
  Tip = -> Pocket013
FEATURE [PartDesign::Pad] Pad020
  Direction = (0,-1,2e-16)
  Length = 25.2
  Length2 = 10
  Midplane = true
  Placement = pos=(0,0,0) rot=(1,0,0;1.5708rad)
  Profile = -> Sketch021
  ReferenceAxis = -> Sketch021 [N_Axis]
  Refine = true
  Suppressed = false
  Type = 0
FEATURE [PartDesign::Body] Body001  label="perno fermo rumble e driver solenoide"
  AllowCompound = false
  Group = -> [Sketch021,Pad020]
  Origin = -> Origin001
  Tip = -> Pad020
FEATURE [PartDesign::Pad] Pad021
  Direction = (0,-1,2e-16)
  Length = 16.8
  Length2 = 10
  Midplane = true
  Placement = pos=(0,0,0) rot=(1,0,0;1.5708rad)
  Profile = -> Sketch061
  ReferenceAxis = -> Sketch061 [N_Axis]
  Refine = true
  Suppressed = false
  Type = 0
FEATURE [PartDesign::Pocket] Pocket014
  BaseFeature = -> Pad021
  Direction = (0,1,-2e-16)
  Length = 12.8
  Length2 = 5
  Midplane = true
  Placement = pos=(0,0,0) rot=(1,0,0;1.5708rad)
  Profile = -> Sketch062
  ReferenceAxis = -> Sketch062 [N_Axis]
  Refine = true
  Suppressed = false
  Type = 0
FEATURE [PartDesign::Pad] Pad022
  BaseFeature = -> Pocket014
  Direction = (0,-1,2e-16)
  Length = 7.6
  Length2 = 10
  Midplane = true
  Placement = pos=(0,0,0) rot=(1,0,0;1.5708rad)
  Profile = -> Sketch063
  ReferenceAxis = -> Sketch063 [N_Axis]
  Refine = true
  Suppressed = false
  Type = 0
FEATURE [PartDesign::Body] Body003  label="blocco switch"
  AllowCompound = false
  Group = -> [Sketch061,Sketch062,Sketch063,Pad021,Pocket014,Pad022]
  Origin = -> Origin003
  Tip = -> Pad022
FEATURE [PartDesign::Pad] Pad024
  Direction = (0,-1,2e-16)
  Length = 17
  Length2 = 10
  Midplane = true
  Placement = pos=(0,0,0) rot=(1,0,0;1.5708rad)
  Profile = -> Sketch045
  ReferenceAxis = -> Sketch045 [N_Axis]
  Refine = true
  Suppressed = false
  Type = 0
FEATURE [PartDesign::Pocket] Pocket015
  BaseFeature = -> Pad024
  Direction = (-1,0,0)
  Length = 8
  Length2 = 5
  Placement = pos=(0,0,0) rot=(1,0,0;1.5708rad)
  Profile = -> Sketch047
  ReferenceAxis = -> Sketch047 [N_Axis]
  Refine = true
  Reversed = true
  Suppressed = false
  Type = 0
FEATURE [PartDesign::Pocket] Pocket016
  BaseFeature = -> Pocket015
  Direction = (-1,0,0)
  Length = 1
  Length2 = 5
  Placement = pos=(0,0,0) rot=(1,0,0;1.5708rad)
  Profile = -> Sketch046
  ReferenceAxis = -> Sketch046 [N_Axis]
  Refine = true
  Reversed = true
  Suppressed = false
  Type = 0
FEATURE [PartDesign::Pocket] Pocket017
  BaseFeature = -> Pocket016
  Direction = (0,1,-2e-16)
  Length = 17
  Length2 = 5
  Midplane = true
  Placement = pos=(0,0,0) rot=(1,0,0;1.5708rad)
  Profile = -> Sketch048
  ReferenceAxis = -> Sketch048 [N_Axis]
  Refine = true
  Suppressed = false
  Type = 0
FEATURE [PartDesign::Pad] Pad025
  BaseFeature = -> Pocket017
  Direction = (0,-1,2e-16)
  Length = 17
  Length2 = 10
  Midplane = true
  Placement = pos=(0,0,0) rot=(1,0,0;1.5708rad)
  Profile = -> Sketch049
  ReferenceAxis = -> Sketch049 [N_Axis]
  Refine = true
  Suppressed = false
  Type = 0
FEATURE [PartDesign::Pad] Pad026
  BaseFeature = -> Pad025
  Direction = (0,-1,2e-16)
  Length = 17
  Length2 = 10
  Midplane = true
  Placement = pos=(0,0,0) rot=(1,0,0;1.5708rad)
  Profile = -> Sketch066
  ReferenceAxis = -> Sketch066 [N_Axis]
  Refine = true
  Suppressed = false
  Type = 0
FEATURE [PartDesign::Pad] Pad027
  BaseFeature = -> Pad026
  Direction = (0,-1,2e-16)
  Length = 5
  Length2 = 10
  Midplane = true
  Placement = pos=(0,0,0) rot=(1,0,0;1.5708rad)
  Profile = -> Sketch064
  ReferenceAxis = -> Sketch064 [N_Axis]
  Refine = true
  Suppressed = false
  Type = 0
FEATURE [PartDesign::Pad] Pad028
  BaseFeature = -> Pad027
  Direction = (1,0,0)
  Length = 1
  Length2 = 10
  Placement = pos=(0,0,0) rot=(1,0,0;1.5708rad)
  Profile = -> Sketch068
  ReferenceAxis = -> Sketch068 [N_Axis]
  Refine = true
  Reversed = true
  Suppressed = false
  Type = 0
FEATURE [PartDesign::Chamfer] Chamfer020
  Angle = 45
  Base = -> Pad028 [Edge73,Edge75,Edge78,Edge77]
  BaseFeature = -> Pad028
  ChamferType = 0
  FlipDirection = false
  Placement = pos=(0,0,0) rot=(1,0,0;1.5708rad)
  Refine = true
  Size = 0.5
  Size2 = 1
  SupportTransform = false
  Suppressed = false
  UseAllEdges = false
FEATURE [PartDesign::Body] Body002  label="supporto per neopixel"
  AllowCompound = false
  Group = -> [Sketch045,Sketch047,Sketch046,Sketch048,Sketch049,Sketch066,Sketch064,Sketch068,Pad024,Pocket015,Pocket016,Pocket017,Pad025,Pad026,Pad027,Pad028,Chamfer020]
  Origin = -> Origin002
  Tip = -> Chamfer020
FEATURE [Sketcher::SketchObject] Sketch134  label="perno fermo rumble002"
  ArcFitTolerance = 1e-06
  AttachmentSupport = -> [XZ_Plane008]
  FullyConstrained = true
  MakeInternals = false
  MapMode = 5
  Placement = pos=(0,0,0) rot=(1,0,0;1.5708rad)
  sketch-geometry (16):
    g0: LineSegment StartX=0 StartY=0.45 StartZ=0 EndX=0 EndY=1.55 EndZ=0
    g1: LineSegment StartX=0.45 StartY=2 StartZ=0 EndX=1.55 EndY=2 EndZ=0
    g2: LineSegment StartX=2 StartY=1.55 StartZ=0 EndX=2 EndY=0.45 EndZ=0
    g3: LineSegment StartX=1.55 StartY=0 StartZ=0 EndX=0.45 EndY=0 EndZ=0
    g4: ArcOfCircle [constr] CenterX=0.45 CenterY=1.55 CenterZ=0 NormalX=0 NormalY=0 NormalZ=1 AngleXU=0 Radius=0.45 StartAngle=1.5708 EndAngle=3.14159
    g5: GeomPoint [constr] X=0 Y=2 Z=0
    g6: LineSegment StartX=0.45 StartY=2 StartZ=0 EndX=0 EndY=1.55 EndZ=0
    g7: ArcOfCircle [constr] CenterX=1.55 CenterY=1.55 CenterZ=0 NormalX=0 NormalY=0 NormalZ=1 AngleXU=0 Radius=0.45 StartAngle=0 EndAngle=1.5708
    g8: GeomPoint [constr] X=2 Y=2 Z=0
    g9: LineSegment StartX=2 StartY=1.55 StartZ=0 EndX=1.55 EndY=2 EndZ=0
    g10: ArcOfCircle [constr] CenterX=1.55 CenterY=0.45 CenterZ=0 NormalX=0 NormalY=0 NormalZ=1 AngleXU=0 Radius=0.45 StartAngle=4.71239 EndAngle=6.28319
    g11: GeomPoint [constr] X=2 Y=0 Z=0
    g12: LineSegment StartX=1.55 StartY=0 StartZ=0 EndX=2 EndY=0.45 EndZ=0
    g13: ArcOfCircle [constr] CenterX=0.45 CenterY=0.45 CenterZ=0 NormalX=0 NormalY=0 NormalZ=1 AngleXU=0 Radius=0.45 StartAngle=3.14159 EndAngle=4.71239
    g14: GeomPoint [constr] X=0 Y=0 Z=0
    g15: LineSegment StartX=0 StartY=0.45 StartZ=0 EndX=0.45 EndY=0 EndZ=0
  constraints (35):
    c: Coincident(g14,g-1)
    c: PointOnObject(g5,g-2)
    c: Horizontal(g1)
    c: Vertical(g2)
    c: Horizontal(g3)
    c: DistanceX(g5,g8) = 2
    c: DistanceY(g11,g8) = 2
    c: PointOnObject(g5,g0)
    c: PointOnObject(g5,g1)
    c: Tangent(g0,g4) = 1.5708
    c: Tangent(g1,g4) = 1.5708
    c: Coincident(g6,g0)
    c: Coincident(g6,g1)
    c: PointOnObject(g8,g2)
    c: PointOnObject(g8,g1)
    c: Tangent(g2,g7) = 1.5708
    c: Tangent(g1,g7) = 1.5708
    c: Coincident(g9,g2)
    c: Coincident(g9,g1)
    c: PointOnObject(g11,g2)
    c: PointOnObject(g11,g3)
    c: Tangent(g2,g10) = 1.5708
    c: Tangent(g3,g10) = 1.5708
    c: Coincident(g12,g2)
    c: Coincident(g12,g3)
    c: PointOnObject(g14,g0)
    c: PointOnObject(g14,g3)
    c: Tangent(g0,g13) = 1.5708
    c: Tangent(g3,g13) = 1.5708
    c: Coincident(g15,g0)
    c: Coincident(g15,g3)
    c: Equal(g6,g9)
    c: Equal(g9,g12)
    c: Equal(g12,g15)
    c: DistanceX(g14,g3) = 0.45
FEATURE [PartDesign::Pad] Pad029
  Direction = (0,-1,2e-16)
  Length = 17
  Length2 = 10
  Midplane = true
  Placement = pos=(0,0,0) rot=(1,0,0;1.5708rad)
  Profile = -> Sketch134
  ReferenceAxis = -> Sketch134 [N_Axis]
  Refine = true
  Suppressed = false
  Type = 0
FEATURE [PartDesign::Body] Body008  label="perno fermo neopixel"
  AllowCompound = false
  Group = -> [Sketch134,Pad029]
  Origin = -> Origin008
  Tip = -> Pad029
note: 2 file-system paths scrubbed to <path> (originals preserved in the JSON sidecar)
